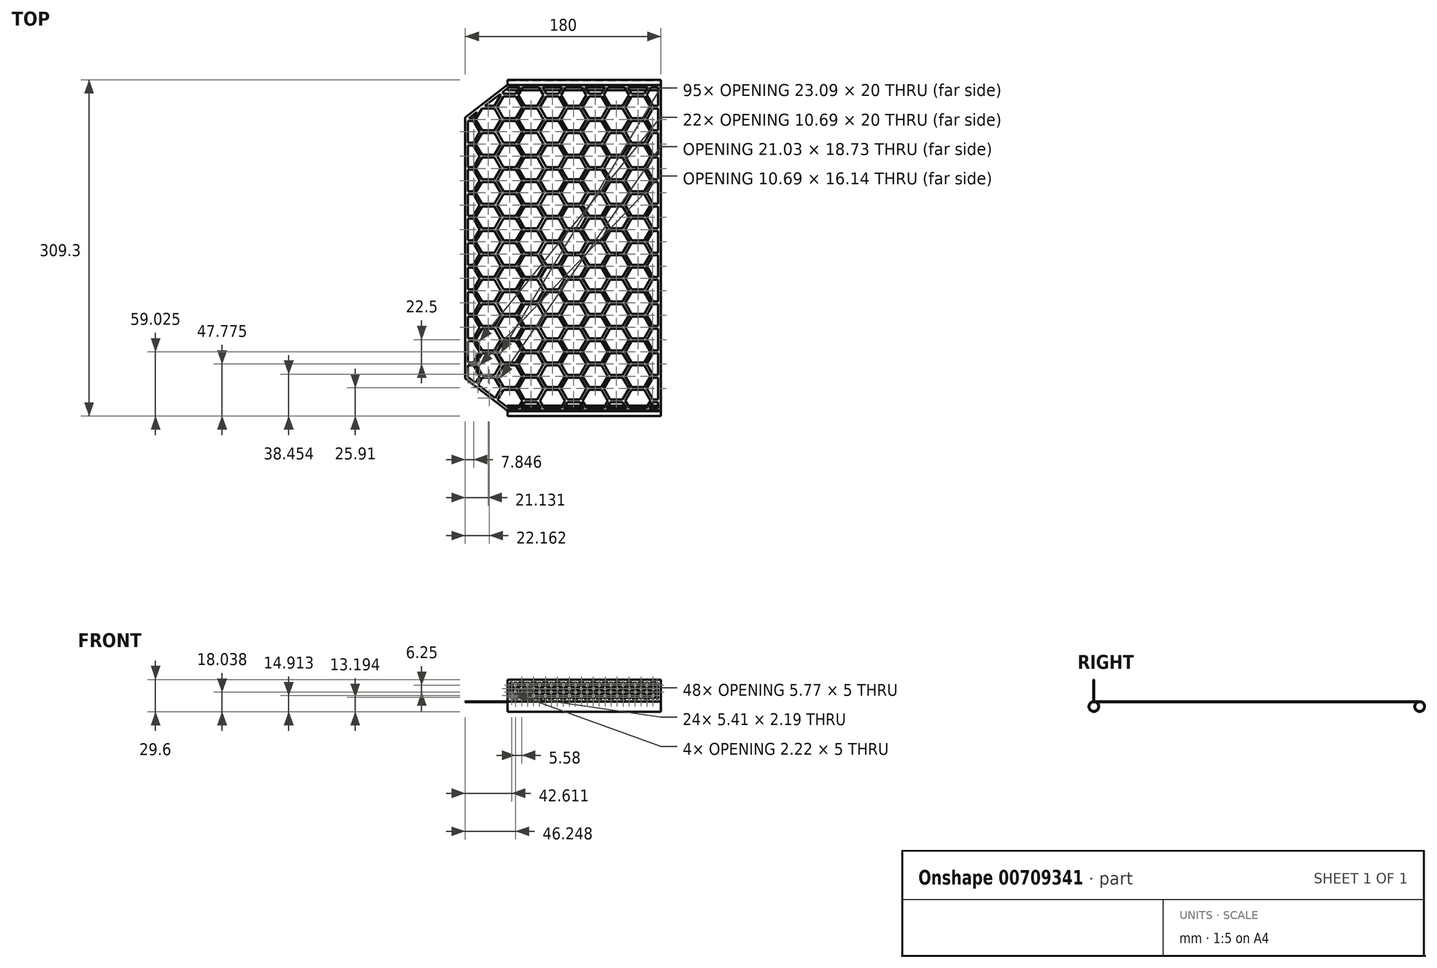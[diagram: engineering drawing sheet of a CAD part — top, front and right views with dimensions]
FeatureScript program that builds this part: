
annotation { "Feature Type Name" : "Feature", "Feature Type Description" : "" }
export const myFeature = defineFeature(function(context is Context, id is Id, definition is map)
    precondition{}
    {
        {
            var Q0;
            Q0=qCreatedBy(makeId("Top.planeOp"),FACE);
            var sketch = newSketch(context, id + "F0", { "sketchPlane" : qUnion([Q0])});
            skLineSegment(sketch, "E0.bottom", {"start": v(90, -150) * mm, "end": v(-90, -150) * mm});
            skLineSegment(sketch, "E0.top", {"start": v(90, 150) * mm, "end": v(-90, 150) * mm});
            skLineSegment(sketch, "E0.left", {"start": v(90, -150) * mm, "end": v(90, 150) * mm});
            skLineSegment(sketch, "E0.right", {"start": v(-90, -150) * mm, "end": v(-90, 150) * mm});
            skPoint(sketch, "E0.middle", {"position": v(0, 0) * mm});
            skLineSegment(sketch, "E1", {"start": v(-51, 150) * mm, "end": v(-90, 120) * mm});
            skLineSegment(sketch, "E2", {"start": v(-90, -120) * mm, "end": v(-51, -150) * mm});
            skSolve(sketch);
        }
        {
            var Q0;
            {var subQ3=sQuery(id+"F0.wireOp",EDGE,"E0.left");Q0=makeQuery(id+"F0.imprint","IMPRINT",FACE,{"disambiguationData":[TD([[makeQuery(id+"F0.imprint","IMPRINT",EDGE,{"derivedFrom":subQ3}),1.0]])]});}
            extrude(context, id + "F1", {"entities" : qUnion([Q0]), "endBound" : BoundingType.SYMMETRIC, "depth" : 0.6 * mm, "offsetDistance" : 25 * mm});
        }
        {
            var Q0;
            Q0=qCreatedBy(makeId("Right.planeOp"),FACE);
            var sketch = newSketch(context, id + "F2", { "sketchPlane" : qUnion([Q0])});
            skCircle(sketch, "E3", {"center": v(-149.85, -4.5) * mm, "radius": 4.2 * mm});
            skCircle(sketch, "E4", {"center": v(-149.85, -4.5) * mm, "radius": 4.8 * mm});
            skCircle(sketch, "E5.MirrorC", {"center": v(149.85, -4.5) * mm, "radius": 4.8 * mm});
            skCircle(sketch, "E6.MirrorC", {"center": v(149.85, -4.5) * mm, "radius": 4.2 * mm});
            skLineSegment(sketch, "E7.bottom", {"start": v(-150.3, 0.3) * mm, "end": v(-149.7, 0.3) * mm});
            skLineSegment(sketch, "E7.top", {"start": v(-150.3, 20.3) * mm, "end": v(-149.7, 20.3) * mm});
            skLineSegment(sketch, "E7.left", {"start": v(-150.3, 0.3) * mm, "end": v(-150.3, 20.3) * mm});
            skLineSegment(sketch, "E7.right", {"start": v(-149.7, 0.3) * mm, "end": v(-149.7, 20.3) * mm});
            skPoint(sketch, "E8", {"position": v(-150, 0.3) * mm});
            skLineSegment(sketch, "E9.0.1", {"start": v(-150, -0.3) * mm, "end": v(-150, 0.3) * mm});
            skLineSegment(sketch, "E9.0.3", {"start": v(-150, 0.3) * mm, "end": v(-150, -0.3) * mm, "construction": true});
            skSolve(sketch);
        }
        {
            var Q0;
            Q0=qSketchRegion(id+"F2",true);
            var Q1;
            Q1=makeQuery(id+"F1.opExtrude","CAP_EDGE",EDGE,{"disambiguationData":[OSD([sQuery(id+"F0.wireOp",EDGE,"E0.bottom")])],"isStart":false});
            sweep(context, id + "F3", {"operationType" : NewBodyOperationType.ADD, "profiles" : qUnion([Q0]), "path" : qUnion([Q1])});
        }
        {
            var Q0;
            Q0=makeQuery(id+"F1.opExtrude","CAP_FACE",FACE,{"disambiguationData":[OSD([sQuery(id+"F0.wireOp",EDGE,"E0.bottom"),sQuery(id+"F0.wireOp",EDGE,"E0.top"),sQuery(id+"F0.wireOp",EDGE,"E0.left"),sQuery(id+"F0.wireOp",EDGE,"E0.right")])],"isStart":false});
            var sketch = newSketch(context, id + "F4", { "sketchPlane" : qUnion([Q0])});
            skCircle(sketch, "E10.cCircle", {"center": v(-68.87, 163.12) * mm, "radius": 10 * mm, "construction": true});
            skLineSegment(sketch, "E10.0", {"start": v(-63.1, 153.12) * mm, "end": v(-74.64, 153.12) * mm});
            skLineSegment(sketch, "E10.1", {"start": v(-74.64, 153.12) * mm, "end": v(-80.42, 163.12) * mm});
            skLineSegment(sketch, "E10.2", {"start": v(-80.42, 163.12) * mm, "end": v(-74.64, 173.12) * mm});
            skLineSegment(sketch, "E10.3", {"start": v(-74.64, 173.12) * mm, "end": v(-63.1, 173.12) * mm});
            skLineSegment(sketch, "E10.4", {"start": v(-63.1, 173.12) * mm, "end": v(-57.32, 163.12) * mm});
            skLineSegment(sketch, "E10.5", {"start": v(-57.32, 163.12) * mm, "end": v(-63.1, 153.12) * mm});
            skPoint(sketch, "E10.0.midPoint", {"position": v(-68.87, 153.12) * mm});
            skCircle(sketch, "E11.cCircle", {"center": v(-88.35, 151.87) * mm, "radius": 10 * mm, "construction": true});
            skLineSegment(sketch, "E11.0", {"start": v(-82.58, 141.87) * mm, "end": v(-94.13, 141.87) * mm});
            skLineSegment(sketch, "E11.1", {"start": v(-94.13, 141.87) * mm, "end": v(-99.9, 151.87) * mm});
            skLineSegment(sketch, "E11.2", {"start": v(-99.9, 151.87) * mm, "end": v(-94.13, 161.87) * mm});
            skLineSegment(sketch, "E11.3", {"start": v(-94.13, 161.87) * mm, "end": v(-82.58, 161.87) * mm});
            skLineSegment(sketch, "E11.4", {"start": v(-82.58, 161.87) * mm, "end": v(-76.8, 151.87) * mm});
            skLineSegment(sketch, "E11.5", {"start": v(-76.8, 151.87) * mm, "end": v(-82.58, 141.87) * mm});
            skPoint(sketch, "E11.0.midPoint", {"position": v(-88.35, 141.87) * mm});
            skLineSegment(sketch, "E12", {"start": v(0, 147.52) * mm, "end": v(0, -147.52) * mm, "construction": true});
            skLineSegment(sketch, "E13", {"start": v(-85.17, 0) * mm, "end": v(85.17, 0) * mm, "construction": true});
            skLineSegment(sketch, "E14.0.1.0", {"start": v(-94.13, 139.37) * mm, "end": v(-82.58, 139.37) * mm});
            skLineSegment(sketch, "E14.0.1.1", {"start": v(-99.9, 129.37) * mm, "end": v(-94.13, 139.37) * mm});
            skLineSegment(sketch, "E14.0.1.2", {"start": v(-94.13, 119.37) * mm, "end": v(-99.9, 129.37) * mm});
            skLineSegment(sketch, "E14.0.1.3", {"start": v(-82.58, 119.37) * mm, "end": v(-94.13, 119.37) * mm});
            skLineSegment(sketch, "E14.0.1.4", {"start": v(-76.8, 129.37) * mm, "end": v(-82.58, 119.37) * mm});
            skLineSegment(sketch, "E14.0.1.5", {"start": v(-82.58, 139.37) * mm, "end": v(-76.8, 129.37) * mm});
            skLineSegment(sketch, "E14.0.1.6", {"start": v(-80.42, 140.62) * mm, "end": v(-74.64, 150.62) * mm});
            skLineSegment(sketch, "E14.0.1.7", {"start": v(-74.64, 130.62) * mm, "end": v(-80.42, 140.62) * mm});
            skLineSegment(sketch, "E14.0.1.8", {"start": v(-74.64, 150.62) * mm, "end": v(-63.1, 150.62) * mm});
            skLineSegment(sketch, "E14.0.1.9", {"start": v(-63.1, 150.62) * mm, "end": v(-57.32, 140.62) * mm});
            skLineSegment(sketch, "E14.0.1.10", {"start": v(-57.32, 140.62) * mm, "end": v(-63.1, 130.62) * mm});
            skLineSegment(sketch, "E14.0.1.11", {"start": v(-63.1, 130.62) * mm, "end": v(-74.64, 130.62) * mm});
            skLineSegment(sketch, "E14.1.0.0", {"start": v(-54.82, 161.87) * mm, "end": v(-43.28, 161.87) * mm});
            skLineSegment(sketch, "E14.1.0.1", {"start": v(-60.6, 151.87) * mm, "end": v(-54.82, 161.87) * mm});
            skLineSegment(sketch, "E14.1.0.2", {"start": v(-54.82, 141.87) * mm, "end": v(-60.6, 151.87) * mm});
            skLineSegment(sketch, "E14.1.0.3", {"start": v(-43.28, 141.87) * mm, "end": v(-54.82, 141.87) * mm});
            skLineSegment(sketch, "E14.1.0.4", {"start": v(-37.5, 151.87) * mm, "end": v(-43.28, 141.87) * mm});
            skLineSegment(sketch, "E14.1.0.5", {"start": v(-43.28, 161.87) * mm, "end": v(-37.5, 151.87) * mm});
            skLineSegment(sketch, "E14.1.0.6", {"start": v(-41.11, 163.12) * mm, "end": v(-35.34, 173.12) * mm});
            skLineSegment(sketch, "E14.1.0.7", {"start": v(-35.34, 153.12) * mm, "end": v(-41.11, 163.12) * mm});
            skLineSegment(sketch, "E14.1.0.8", {"start": v(-35.34, 173.12) * mm, "end": v(-23.79, 173.12) * mm});
            skLineSegment(sketch, "E14.1.0.9", {"start": v(-23.79, 173.12) * mm, "end": v(-18.02, 163.12) * mm});
            skLineSegment(sketch, "E14.1.0.10", {"start": v(-18.02, 163.12) * mm, "end": v(-23.79, 153.12) * mm});
            skLineSegment(sketch, "E14.1.0.11", {"start": v(-23.79, 153.12) * mm, "end": v(-35.34, 153.12) * mm});
            skLineSegment(sketch, "E14.1.1.0", {"start": v(-54.82, 139.37) * mm, "end": v(-43.28, 139.37) * mm});
            skLineSegment(sketch, "E14.1.1.1", {"start": v(-60.6, 129.37) * mm, "end": v(-54.82, 139.37) * mm});
            skLineSegment(sketch, "E14.1.1.2", {"start": v(-54.82, 119.37) * mm, "end": v(-60.6, 129.37) * mm});
            skLineSegment(sketch, "E14.1.1.3", {"start": v(-43.28, 119.37) * mm, "end": v(-54.82, 119.37) * mm});
            skLineSegment(sketch, "E14.1.1.4", {"start": v(-37.5, 129.37) * mm, "end": v(-43.28, 119.37) * mm});
            skLineSegment(sketch, "E14.1.1.5", {"start": v(-43.28, 139.37) * mm, "end": v(-37.5, 129.37) * mm});
            skLineSegment(sketch, "E14.1.1.6", {"start": v(-41.11, 140.62) * mm, "end": v(-35.34, 150.62) * mm});
            skLineSegment(sketch, "E14.1.1.7", {"start": v(-35.34, 130.62) * mm, "end": v(-41.11, 140.62) * mm});
            skLineSegment(sketch, "E14.1.1.8", {"start": v(-35.34, 150.62) * mm, "end": v(-23.79, 150.62) * mm});
            skLineSegment(sketch, "E14.1.1.9", {"start": v(-23.79, 150.62) * mm, "end": v(-18.02, 140.62) * mm});
            skLineSegment(sketch, "E14.1.1.10", {"start": v(-18.02, 140.62) * mm, "end": v(-23.79, 130.62) * mm});
            skLineSegment(sketch, "E14.1.1.11", {"start": v(-23.79, 130.62) * mm, "end": v(-35.34, 130.62) * mm});
            skLineSegment(sketch, "E14.2.0.0", {"start": v(-15.52, 161.87) * mm, "end": v(-3.97, 161.87) * mm});
            skLineSegment(sketch, "E14.2.0.1", {"start": v(-21.29, 151.87) * mm, "end": v(-15.52, 161.87) * mm});
            skLineSegment(sketch, "E14.2.0.2", {"start": v(-15.52, 141.87) * mm, "end": v(-21.29, 151.87) * mm});
            skLineSegment(sketch, "E14.2.0.3", {"start": v(-3.97, 141.87) * mm, "end": v(-15.52, 141.87) * mm});
            skLineSegment(sketch, "E14.2.0.4", {"start": v(1.8, 151.87) * mm, "end": v(-3.97, 141.87) * mm});
            skLineSegment(sketch, "E14.2.0.5", {"start": v(-3.97, 161.87) * mm, "end": v(1.8, 151.87) * mm});
            skLineSegment(sketch, "E14.2.0.6", {"start": v(-1.8, 163.12) * mm, "end": v(3.97, 173.12) * mm});
            skLineSegment(sketch, "E14.2.0.7", {"start": v(3.97, 153.12) * mm, "end": v(-1.8, 163.12) * mm});
            skLineSegment(sketch, "E14.2.0.8", {"start": v(3.97, 173.12) * mm, "end": v(15.52, 173.12) * mm});
            skLineSegment(sketch, "E14.2.0.9", {"start": v(15.52, 173.12) * mm, "end": v(21.29, 163.12) * mm});
            skLineSegment(sketch, "E14.2.0.10", {"start": v(21.29, 163.12) * mm, "end": v(15.52, 153.12) * mm});
            skLineSegment(sketch, "E14.2.0.11", {"start": v(15.52, 153.12) * mm, "end": v(3.97, 153.12) * mm});
            skLineSegment(sketch, "E14.2.1.0", {"start": v(-15.52, 139.37) * mm, "end": v(-3.97, 139.37) * mm});
            skLineSegment(sketch, "E14.2.1.1", {"start": v(-21.29, 129.37) * mm, "end": v(-15.52, 139.37) * mm});
            skLineSegment(sketch, "E14.2.1.2", {"start": v(-15.52, 119.37) * mm, "end": v(-21.29, 129.37) * mm});
            skLineSegment(sketch, "E14.2.1.3", {"start": v(-3.97, 119.37) * mm, "end": v(-15.52, 119.37) * mm});
            skLineSegment(sketch, "E14.2.1.4", {"start": v(1.8, 129.37) * mm, "end": v(-3.97, 119.37) * mm});
            skLineSegment(sketch, "E14.2.1.5", {"start": v(-3.97, 139.37) * mm, "end": v(1.8, 129.37) * mm});
            skLineSegment(sketch, "E14.2.1.6", {"start": v(-1.8, 140.62) * mm, "end": v(3.97, 150.62) * mm});
            skLineSegment(sketch, "E14.2.1.7", {"start": v(3.97, 130.62) * mm, "end": v(-1.8, 140.62) * mm});
            skLineSegment(sketch, "E14.2.1.8", {"start": v(3.97, 150.62) * mm, "end": v(15.52, 150.62) * mm});
            skLineSegment(sketch, "E14.2.1.9", {"start": v(15.52, 150.62) * mm, "end": v(21.29, 140.62) * mm});
            skLineSegment(sketch, "E14.2.1.10", {"start": v(21.29, 140.62) * mm, "end": v(15.52, 130.62) * mm});
            skLineSegment(sketch, "E14.2.1.11", {"start": v(15.52, 130.62) * mm, "end": v(3.97, 130.62) * mm});
            skLineSegment(sketch, "E14.direction1", {"start": v(-94.13, 161.87) * mm, "end": v(-54.82, 161.87) * mm, "construction": true});
            skLineSegment(sketch, "E14.direction2", {"start": v(-94.13, 161.87) * mm, "end": v(-94.13, 139.37) * mm, "construction": true});
            skLineSegment(sketch, "E15.0.3.0", {"start": v(23.79, 161.87) * mm, "end": v(35.34, 161.87) * mm});
            skLineSegment(sketch, "E15.3.3.0", {"start": v(18.02, 151.87) * mm, "end": v(23.79, 161.87) * mm});
            skLineSegment(sketch, "E15.6.3.0", {"start": v(23.79, 141.87) * mm, "end": v(18.02, 151.87) * mm});
            skLineSegment(sketch, "E15.9.3.0", {"start": v(35.34, 141.87) * mm, "end": v(23.79, 141.87) * mm});
            skLineSegment(sketch, "E15.12.3.0", {"start": v(41.11, 151.87) * mm, "end": v(35.34, 141.87) * mm});
            skLineSegment(sketch, "E15.15.3.0", {"start": v(35.34, 161.87) * mm, "end": v(41.11, 151.87) * mm});
            skLineSegment(sketch, "E15.18.3.0", {"start": v(37.5, 163.12) * mm, "end": v(43.28, 173.12) * mm});
            skLineSegment(sketch, "E15.21.3.0", {"start": v(43.28, 153.12) * mm, "end": v(37.5, 163.12) * mm});
            skLineSegment(sketch, "E15.24.3.0", {"start": v(43.28, 173.12) * mm, "end": v(54.82, 173.12) * mm});
            skLineSegment(sketch, "E15.27.3.0", {"start": v(54.82, 173.12) * mm, "end": v(60.6, 163.12) * mm});
            skLineSegment(sketch, "E15.30.3.0", {"start": v(60.6, 163.12) * mm, "end": v(54.82, 153.12) * mm});
            skLineSegment(sketch, "E15.33.3.0", {"start": v(54.82, 153.12) * mm, "end": v(43.28, 153.12) * mm});
            skLineSegment(sketch, "E15.0.3.1", {"start": v(23.79, 139.37) * mm, "end": v(35.34, 139.37) * mm});
            skLineSegment(sketch, "E15.3.3.1", {"start": v(18.02, 129.37) * mm, "end": v(23.79, 139.37) * mm});
            skLineSegment(sketch, "E15.6.3.1", {"start": v(23.79, 119.37) * mm, "end": v(18.02, 129.37) * mm});
            skLineSegment(sketch, "E15.9.3.1", {"start": v(35.34, 119.37) * mm, "end": v(23.79, 119.37) * mm});
            skLineSegment(sketch, "E15.12.3.1", {"start": v(41.11, 129.37) * mm, "end": v(35.34, 119.37) * mm});
            skLineSegment(sketch, "E15.15.3.1", {"start": v(35.34, 139.37) * mm, "end": v(41.11, 129.37) * mm});
            skLineSegment(sketch, "E15.18.3.1", {"start": v(37.5, 140.62) * mm, "end": v(43.28, 150.62) * mm});
            skLineSegment(sketch, "E15.21.3.1", {"start": v(43.28, 130.62) * mm, "end": v(37.5, 140.62) * mm});
            skLineSegment(sketch, "E15.24.3.1", {"start": v(43.28, 150.62) * mm, "end": v(54.82, 150.62) * mm});
            skLineSegment(sketch, "E15.27.3.1", {"start": v(54.82, 150.62) * mm, "end": v(60.6, 140.62) * mm});
            skLineSegment(sketch, "E15.30.3.1", {"start": v(60.6, 140.62) * mm, "end": v(54.82, 130.62) * mm});
            skLineSegment(sketch, "E15.33.3.1", {"start": v(54.82, 130.62) * mm, "end": v(43.28, 130.62) * mm});
            skLineSegment(sketch, "E15.0.4.0", {"start": v(63.1, 161.87) * mm, "end": v(74.64, 161.87) * mm});
            skLineSegment(sketch, "E15.3.4.0", {"start": v(57.32, 151.87) * mm, "end": v(63.1, 161.87) * mm});
            skLineSegment(sketch, "E15.6.4.0", {"start": v(63.1, 141.87) * mm, "end": v(57.32, 151.87) * mm});
            skLineSegment(sketch, "E15.9.4.0", {"start": v(74.64, 141.87) * mm, "end": v(63.1, 141.87) * mm});
            skLineSegment(sketch, "E15.12.4.0", {"start": v(80.42, 151.87) * mm, "end": v(74.64, 141.87) * mm});
            skLineSegment(sketch, "E15.15.4.0", {"start": v(74.64, 161.87) * mm, "end": v(80.42, 151.87) * mm});
            skLineSegment(sketch, "E15.18.4.0", {"start": v(76.8, 163.12) * mm, "end": v(82.58, 173.12) * mm});
            skLineSegment(sketch, "E15.21.4.0", {"start": v(82.58, 153.12) * mm, "end": v(76.8, 163.12) * mm});
            skLineSegment(sketch, "E15.24.4.0", {"start": v(82.58, 173.12) * mm, "end": v(94.13, 173.12) * mm});
            skLineSegment(sketch, "E15.27.4.0", {"start": v(94.13, 173.12) * mm, "end": v(99.9, 163.12) * mm});
            skLineSegment(sketch, "E15.30.4.0", {"start": v(99.9, 163.12) * mm, "end": v(94.13, 153.12) * mm});
            skLineSegment(sketch, "E15.33.4.0", {"start": v(94.13, 153.12) * mm, "end": v(82.58, 153.12) * mm});
            skLineSegment(sketch, "E15.0.4.1", {"start": v(63.1, 139.37) * mm, "end": v(74.64, 139.37) * mm});
            skLineSegment(sketch, "E15.3.4.1", {"start": v(57.32, 129.37) * mm, "end": v(63.1, 139.37) * mm});
            skLineSegment(sketch, "E15.6.4.1", {"start": v(63.1, 119.37) * mm, "end": v(57.32, 129.37) * mm});
            skLineSegment(sketch, "E15.9.4.1", {"start": v(74.64, 119.37) * mm, "end": v(63.1, 119.37) * mm});
            skLineSegment(sketch, "E15.12.4.1", {"start": v(80.42, 129.37) * mm, "end": v(74.64, 119.37) * mm});
            skLineSegment(sketch, "E15.15.4.1", {"start": v(74.64, 139.37) * mm, "end": v(80.42, 129.37) * mm});
            skLineSegment(sketch, "E15.18.4.1", {"start": v(76.8, 140.62) * mm, "end": v(82.58, 150.62) * mm});
            skLineSegment(sketch, "E15.21.4.1", {"start": v(82.58, 130.62) * mm, "end": v(76.8, 140.62) * mm});
            skLineSegment(sketch, "E15.24.4.1", {"start": v(82.58, 150.62) * mm, "end": v(94.13, 150.62) * mm});
            skLineSegment(sketch, "E15.27.4.1", {"start": v(94.13, 150.62) * mm, "end": v(99.9, 140.62) * mm});
            skLineSegment(sketch, "E15.30.4.1", {"start": v(99.9, 140.62) * mm, "end": v(94.13, 130.62) * mm});
            skLineSegment(sketch, "E15.33.4.1", {"start": v(94.13, 130.62) * mm, "end": v(82.58, 130.62) * mm});
            skLineSegment(sketch, "E16.0.0.2", {"start": v(-94.13, 116.87) * mm, "end": v(-82.58, 116.87) * mm});
            skLineSegment(sketch, "E16.3.0.2", {"start": v(-99.9, 106.87) * mm, "end": v(-94.13, 116.87) * mm});
            skLineSegment(sketch, "E16.6.0.2", {"start": v(-94.13, 96.87) * mm, "end": v(-99.9, 106.87) * mm});
            skLineSegment(sketch, "E16.9.0.2", {"start": v(-82.58, 96.87) * mm, "end": v(-94.13, 96.87) * mm});
            skLineSegment(sketch, "E16.12.0.2", {"start": v(-76.8, 106.87) * mm, "end": v(-82.58, 96.87) * mm});
            skLineSegment(sketch, "E16.15.0.2", {"start": v(-82.58, 116.87) * mm, "end": v(-76.8, 106.87) * mm});
            skLineSegment(sketch, "E16.18.0.2", {"start": v(-80.42, 118.12) * mm, "end": v(-74.64, 128.12) * mm});
            skLineSegment(sketch, "E16.21.0.2", {"start": v(-74.64, 108.12) * mm, "end": v(-80.42, 118.12) * mm});
            skLineSegment(sketch, "E16.24.0.2", {"start": v(-74.64, 128.12) * mm, "end": v(-63.1, 128.12) * mm});
            skLineSegment(sketch, "E16.27.0.2", {"start": v(-63.1, 128.12) * mm, "end": v(-57.32, 118.12) * mm});
            skLineSegment(sketch, "E16.30.0.2", {"start": v(-57.32, 118.12) * mm, "end": v(-63.1, 108.12) * mm});
            skLineSegment(sketch, "E16.33.0.2", {"start": v(-63.1, 108.12) * mm, "end": v(-74.64, 108.12) * mm});
            skLineSegment(sketch, "E16.0.0.3", {"start": v(-94.13, 94.37) * mm, "end": v(-82.58, 94.37) * mm});
            skLineSegment(sketch, "E16.3.0.3", {"start": v(-99.9, 84.37) * mm, "end": v(-94.13, 94.37) * mm});
            skLineSegment(sketch, "E16.6.0.3", {"start": v(-94.13, 74.37) * mm, "end": v(-99.9, 84.37) * mm});
            skLineSegment(sketch, "E16.9.0.3", {"start": v(-82.58, 74.37) * mm, "end": v(-94.13, 74.37) * mm});
            skLineSegment(sketch, "E16.12.0.3", {"start": v(-76.8, 84.37) * mm, "end": v(-82.58, 74.37) * mm});
            skLineSegment(sketch, "E16.15.0.3", {"start": v(-82.58, 94.37) * mm, "end": v(-76.8, 84.37) * mm});
            skLineSegment(sketch, "E16.18.0.3", {"start": v(-80.42, 95.62) * mm, "end": v(-74.64, 105.62) * mm});
            skLineSegment(sketch, "E16.21.0.3", {"start": v(-74.64, 85.62) * mm, "end": v(-80.42, 95.62) * mm});
            skLineSegment(sketch, "E16.24.0.3", {"start": v(-74.64, 105.62) * mm, "end": v(-63.1, 105.62) * mm});
            skLineSegment(sketch, "E16.27.0.3", {"start": v(-63.1, 105.62) * mm, "end": v(-57.32, 95.62) * mm});
            skLineSegment(sketch, "E16.30.0.3", {"start": v(-57.32, 95.62) * mm, "end": v(-63.1, 85.62) * mm});
            skLineSegment(sketch, "E16.33.0.3", {"start": v(-63.1, 85.62) * mm, "end": v(-74.64, 85.62) * mm});
            skLineSegment(sketch, "E16.0.0.4", {"start": v(-94.13, 71.87) * mm, "end": v(-82.58, 71.87) * mm});
            skLineSegment(sketch, "E16.3.0.4", {"start": v(-99.9, 61.87) * mm, "end": v(-94.13, 71.87) * mm});
            skLineSegment(sketch, "E16.6.0.4", {"start": v(-94.13, 51.87) * mm, "end": v(-99.9, 61.87) * mm});
            skLineSegment(sketch, "E16.9.0.4", {"start": v(-82.58, 51.87) * mm, "end": v(-94.13, 51.87) * mm});
            skLineSegment(sketch, "E16.12.0.4", {"start": v(-76.8, 61.87) * mm, "end": v(-82.58, 51.87) * mm});
            skLineSegment(sketch, "E16.15.0.4", {"start": v(-82.58, 71.87) * mm, "end": v(-76.8, 61.87) * mm});
            skLineSegment(sketch, "E16.18.0.4", {"start": v(-80.42, 73.12) * mm, "end": v(-74.64, 83.12) * mm});
            skLineSegment(sketch, "E16.21.0.4", {"start": v(-74.64, 63.12) * mm, "end": v(-80.42, 73.12) * mm});
            skLineSegment(sketch, "E16.24.0.4", {"start": v(-74.64, 83.12) * mm, "end": v(-63.1, 83.12) * mm});
            skLineSegment(sketch, "E16.27.0.4", {"start": v(-63.1, 83.12) * mm, "end": v(-57.32, 73.12) * mm});
            skLineSegment(sketch, "E16.30.0.4", {"start": v(-57.32, 73.12) * mm, "end": v(-63.1, 63.12) * mm});
            skLineSegment(sketch, "E16.33.0.4", {"start": v(-63.1, 63.12) * mm, "end": v(-74.64, 63.12) * mm});
            skLineSegment(sketch, "E16.0.0.5", {"start": v(-94.13, 49.37) * mm, "end": v(-82.58, 49.37) * mm});
            skLineSegment(sketch, "E16.3.0.5", {"start": v(-99.9, 39.37) * mm, "end": v(-94.13, 49.37) * mm});
            skLineSegment(sketch, "E16.6.0.5", {"start": v(-94.13, 29.37) * mm, "end": v(-99.9, 39.37) * mm});
            skLineSegment(sketch, "E16.9.0.5", {"start": v(-82.58, 29.37) * mm, "end": v(-94.13, 29.37) * mm});
            skLineSegment(sketch, "E16.12.0.5", {"start": v(-76.8, 39.37) * mm, "end": v(-82.58, 29.37) * mm});
            skLineSegment(sketch, "E16.15.0.5", {"start": v(-82.58, 49.37) * mm, "end": v(-76.8, 39.37) * mm});
            skLineSegment(sketch, "E16.18.0.5", {"start": v(-80.42, 50.62) * mm, "end": v(-74.64, 60.62) * mm});
            skLineSegment(sketch, "E16.21.0.5", {"start": v(-74.64, 40.62) * mm, "end": v(-80.42, 50.62) * mm});
            skLineSegment(sketch, "E16.24.0.5", {"start": v(-74.64, 60.62) * mm, "end": v(-63.1, 60.62) * mm});
            skLineSegment(sketch, "E16.27.0.5", {"start": v(-63.1, 60.62) * mm, "end": v(-57.32, 50.62) * mm});
            skLineSegment(sketch, "E16.30.0.5", {"start": v(-57.32, 50.62) * mm, "end": v(-63.1, 40.62) * mm});
            skLineSegment(sketch, "E16.33.0.5", {"start": v(-63.1, 40.62) * mm, "end": v(-74.64, 40.62) * mm});
            skLineSegment(sketch, "E16.0.0.6", {"start": v(-94.13, 26.87) * mm, "end": v(-82.58, 26.87) * mm});
            skLineSegment(sketch, "E16.3.0.6", {"start": v(-99.9, 16.87) * mm, "end": v(-94.13, 26.87) * mm});
            skLineSegment(sketch, "E16.6.0.6", {"start": v(-94.13, 6.87) * mm, "end": v(-99.9, 16.87) * mm});
            skLineSegment(sketch, "E16.9.0.6", {"start": v(-82.58, 6.87) * mm, "end": v(-94.13, 6.87) * mm});
            skLineSegment(sketch, "E16.12.0.6", {"start": v(-76.8, 16.87) * mm, "end": v(-82.58, 6.87) * mm});
            skLineSegment(sketch, "E16.15.0.6", {"start": v(-82.58, 26.87) * mm, "end": v(-76.8, 16.87) * mm});
            skLineSegment(sketch, "E16.18.0.6", {"start": v(-80.42, 28.12) * mm, "end": v(-74.64, 38.12) * mm});
            skLineSegment(sketch, "E16.21.0.6", {"start": v(-74.64, 18.12) * mm, "end": v(-80.42, 28.12) * mm});
            skLineSegment(sketch, "E16.24.0.6", {"start": v(-74.64, 38.12) * mm, "end": v(-63.1, 38.12) * mm});
            skLineSegment(sketch, "E16.27.0.6", {"start": v(-63.1, 38.12) * mm, "end": v(-57.32, 28.12) * mm});
            skLineSegment(sketch, "E16.30.0.6", {"start": v(-57.32, 28.12) * mm, "end": v(-63.1, 18.12) * mm});
            skLineSegment(sketch, "E16.33.0.6", {"start": v(-63.1, 18.12) * mm, "end": v(-74.64, 18.12) * mm});
            skLineSegment(sketch, "E16.0.0.7", {"start": v(-94.13, 4.37) * mm, "end": v(-82.58, 4.37) * mm});
            skLineSegment(sketch, "E16.3.0.7", {"start": v(-99.9, -5.63) * mm, "end": v(-94.13, 4.37) * mm});
            skLineSegment(sketch, "E16.6.0.7", {"start": v(-94.13, -15.63) * mm, "end": v(-99.9, -5.63) * mm});
            skLineSegment(sketch, "E16.9.0.7", {"start": v(-82.58, -15.63) * mm, "end": v(-94.13, -15.63) * mm});
            skLineSegment(sketch, "E16.12.0.7", {"start": v(-76.8, -5.63) * mm, "end": v(-82.58, -15.63) * mm});
            skLineSegment(sketch, "E16.15.0.7", {"start": v(-82.58, 4.37) * mm, "end": v(-76.8, -5.63) * mm});
            skLineSegment(sketch, "E16.18.0.7", {"start": v(-80.42, 5.62) * mm, "end": v(-74.64, 15.62) * mm});
            skLineSegment(sketch, "E16.21.0.7", {"start": v(-74.64, -4.38) * mm, "end": v(-80.42, 5.62) * mm});
            skLineSegment(sketch, "E16.24.0.7", {"start": v(-74.64, 15.62) * mm, "end": v(-63.1, 15.62) * mm});
            skLineSegment(sketch, "E16.27.0.7", {"start": v(-63.1, 15.62) * mm, "end": v(-57.32, 5.62) * mm});
            skLineSegment(sketch, "E16.30.0.7", {"start": v(-57.32, 5.62) * mm, "end": v(-63.1, -4.38) * mm});
            skLineSegment(sketch, "E16.33.0.7", {"start": v(-63.1, -4.38) * mm, "end": v(-74.64, -4.38) * mm});
            skLineSegment(sketch, "E16.0.0.8", {"start": v(-94.13, -18.13) * mm, "end": v(-82.58, -18.13) * mm});
            skLineSegment(sketch, "E16.3.0.8", {"start": v(-99.9, -28.13) * mm, "end": v(-94.13, -18.13) * mm});
            skLineSegment(sketch, "E16.6.0.8", {"start": v(-94.13, -38.13) * mm, "end": v(-99.9, -28.13) * mm});
            skLineSegment(sketch, "E16.9.0.8", {"start": v(-82.58, -38.13) * mm, "end": v(-94.13, -38.13) * mm});
            skLineSegment(sketch, "E16.12.0.8", {"start": v(-76.8, -28.13) * mm, "end": v(-82.58, -38.13) * mm});
            skLineSegment(sketch, "E16.15.0.8", {"start": v(-82.58, -18.13) * mm, "end": v(-76.8, -28.13) * mm});
            skLineSegment(sketch, "E16.18.0.8", {"start": v(-80.42, -16.88) * mm, "end": v(-74.64, -6.88) * mm});
            skLineSegment(sketch, "E16.21.0.8", {"start": v(-74.64, -26.88) * mm, "end": v(-80.42, -16.88) * mm});
            skLineSegment(sketch, "E16.24.0.8", {"start": v(-74.64, -6.88) * mm, "end": v(-63.1, -6.88) * mm});
            skLineSegment(sketch, "E16.27.0.8", {"start": v(-63.1, -6.88) * mm, "end": v(-57.32, -16.88) * mm});
            skLineSegment(sketch, "E16.30.0.8", {"start": v(-57.32, -16.88) * mm, "end": v(-63.1, -26.88) * mm});
            skLineSegment(sketch, "E16.33.0.8", {"start": v(-63.1, -26.88) * mm, "end": v(-74.64, -26.88) * mm});
            skLineSegment(sketch, "E16.0.0.9", {"start": v(-94.13, -40.63) * mm, "end": v(-82.58, -40.63) * mm});
            skLineSegment(sketch, "E16.3.0.9", {"start": v(-99.9, -50.63) * mm, "end": v(-94.13, -40.63) * mm});
            skLineSegment(sketch, "E16.6.0.9", {"start": v(-94.13, -60.63) * mm, "end": v(-99.9, -50.63) * mm});
            skLineSegment(sketch, "E16.9.0.9", {"start": v(-82.58, -60.63) * mm, "end": v(-94.13, -60.63) * mm});
            skLineSegment(sketch, "E16.12.0.9", {"start": v(-76.8, -50.63) * mm, "end": v(-82.58, -60.63) * mm});
            skLineSegment(sketch, "E16.15.0.9", {"start": v(-82.58, -40.63) * mm, "end": v(-76.8, -50.63) * mm});
            skLineSegment(sketch, "E16.18.0.9", {"start": v(-80.42, -39.38) * mm, "end": v(-74.64, -29.38) * mm});
            skLineSegment(sketch, "E16.21.0.9", {"start": v(-74.64, -49.38) * mm, "end": v(-80.42, -39.38) * mm});
            skLineSegment(sketch, "E16.24.0.9", {"start": v(-74.64, -29.38) * mm, "end": v(-63.1, -29.38) * mm});
            skLineSegment(sketch, "E16.27.0.9", {"start": v(-63.1, -29.38) * mm, "end": v(-57.32, -39.38) * mm});
            skLineSegment(sketch, "E16.30.0.9", {"start": v(-57.32, -39.38) * mm, "end": v(-63.1, -49.38) * mm});
            skLineSegment(sketch, "E16.33.0.9", {"start": v(-63.1, -49.38) * mm, "end": v(-74.64, -49.38) * mm});
            skLineSegment(sketch, "E16.0.0.10", {"start": v(-94.13, -63.13) * mm, "end": v(-82.58, -63.13) * mm});
            skLineSegment(sketch, "E16.3.0.10", {"start": v(-99.9, -73.13) * mm, "end": v(-94.13, -63.13) * mm});
            skLineSegment(sketch, "E16.6.0.10", {"start": v(-94.13, -83.13) * mm, "end": v(-99.9, -73.13) * mm});
            skLineSegment(sketch, "E16.9.0.10", {"start": v(-82.58, -83.13) * mm, "end": v(-94.13, -83.13) * mm});
            skLineSegment(sketch, "E16.12.0.10", {"start": v(-76.8, -73.13) * mm, "end": v(-82.58, -83.13) * mm});
            skLineSegment(sketch, "E16.15.0.10", {"start": v(-82.58, -63.13) * mm, "end": v(-76.8, -73.13) * mm});
            skLineSegment(sketch, "E16.18.0.10", {"start": v(-80.42, -61.88) * mm, "end": v(-74.64, -51.88) * mm});
            skLineSegment(sketch, "E16.21.0.10", {"start": v(-74.64, -71.88) * mm, "end": v(-80.42, -61.88) * mm});
            skLineSegment(sketch, "E16.24.0.10", {"start": v(-74.64, -51.88) * mm, "end": v(-63.1, -51.88) * mm});
            skLineSegment(sketch, "E16.27.0.10", {"start": v(-63.1, -51.88) * mm, "end": v(-57.32, -61.88) * mm});
            skLineSegment(sketch, "E16.30.0.10", {"start": v(-57.32, -61.88) * mm, "end": v(-63.1, -71.88) * mm});
            skLineSegment(sketch, "E16.33.0.10", {"start": v(-63.1, -71.88) * mm, "end": v(-74.64, -71.88) * mm});
            skLineSegment(sketch, "E16.0.0.11", {"start": v(-94.13, -85.63) * mm, "end": v(-82.58, -85.63) * mm});
            skLineSegment(sketch, "E16.3.0.11", {"start": v(-99.9, -95.63) * mm, "end": v(-94.13, -85.63) * mm});
            skLineSegment(sketch, "E16.6.0.11", {"start": v(-94.13, -105.63) * mm, "end": v(-99.9, -95.63) * mm});
            skLineSegment(sketch, "E16.9.0.11", {"start": v(-82.58, -105.63) * mm, "end": v(-94.13, -105.63) * mm});
            skLineSegment(sketch, "E16.12.0.11", {"start": v(-76.8, -95.63) * mm, "end": v(-82.58, -105.63) * mm});
            skLineSegment(sketch, "E16.15.0.11", {"start": v(-82.58, -85.62) * mm, "end": v(-76.8, -95.63) * mm});
            skLineSegment(sketch, "E16.18.0.11", {"start": v(-80.42, -84.38) * mm, "end": v(-74.64, -74.38) * mm});
            skLineSegment(sketch, "E16.21.0.11", {"start": v(-74.64, -94.38) * mm, "end": v(-80.42, -84.38) * mm});
            skLineSegment(sketch, "E16.24.0.11", {"start": v(-74.64, -74.38) * mm, "end": v(-63.1, -74.38) * mm});
            skLineSegment(sketch, "E16.27.0.11", {"start": v(-63.1, -74.38) * mm, "end": v(-57.32, -84.38) * mm});
            skLineSegment(sketch, "E16.30.0.11", {"start": v(-57.32, -84.38) * mm, "end": v(-63.1, -94.38) * mm});
            skLineSegment(sketch, "E16.33.0.11", {"start": v(-63.1, -94.38) * mm, "end": v(-74.64, -94.38) * mm});
            skLineSegment(sketch, "E16.0.0.12", {"start": v(-94.13, -108.13) * mm, "end": v(-82.58, -108.13) * mm});
            skLineSegment(sketch, "E16.3.0.12", {"start": v(-99.9, -118.13) * mm, "end": v(-94.13, -108.13) * mm});
            skLineSegment(sketch, "E16.6.0.12", {"start": v(-94.13, -128.13) * mm, "end": v(-99.9, -118.13) * mm});
            skLineSegment(sketch, "E16.9.0.12", {"start": v(-82.58, -128.13) * mm, "end": v(-94.13, -128.13) * mm});
            skLineSegment(sketch, "E16.12.0.12", {"start": v(-76.8, -118.13) * mm, "end": v(-82.58, -128.13) * mm});
            skLineSegment(sketch, "E16.15.0.12", {"start": v(-82.58, -108.13) * mm, "end": v(-76.8, -118.13) * mm});
            skLineSegment(sketch, "E16.18.0.12", {"start": v(-80.42, -106.88) * mm, "end": v(-74.64, -96.88) * mm});
            skLineSegment(sketch, "E16.21.0.12", {"start": v(-74.64, -116.87) * mm, "end": v(-80.42, -106.88) * mm});
            skLineSegment(sketch, "E16.24.0.12", {"start": v(-74.64, -96.88) * mm, "end": v(-63.1, -96.88) * mm});
            skLineSegment(sketch, "E16.27.0.12", {"start": v(-63.1, -96.88) * mm, "end": v(-57.32, -106.88) * mm});
            skLineSegment(sketch, "E16.30.0.12", {"start": v(-57.32, -106.88) * mm, "end": v(-63.1, -116.88) * mm});
            skLineSegment(sketch, "E16.33.0.12", {"start": v(-63.1, -116.88) * mm, "end": v(-74.64, -116.88) * mm});
            skLineSegment(sketch, "E16.0.0.13", {"start": v(-94.13, -130.62) * mm, "end": v(-82.58, -130.62) * mm});
            skLineSegment(sketch, "E16.3.0.13", {"start": v(-99.9, -140.63) * mm, "end": v(-94.13, -130.63) * mm});
            skLineSegment(sketch, "E16.6.0.13", {"start": v(-94.13, -150.63) * mm, "end": v(-99.9, -140.63) * mm});
            skLineSegment(sketch, "E16.9.0.13", {"start": v(-82.58, -150.62) * mm, "end": v(-94.13, -150.62) * mm});
            skLineSegment(sketch, "E16.12.0.13", {"start": v(-76.8, -140.62) * mm, "end": v(-82.58, -150.62) * mm});
            skLineSegment(sketch, "E16.15.0.13", {"start": v(-82.58, -130.62) * mm, "end": v(-76.8, -140.62) * mm});
            skLineSegment(sketch, "E16.18.0.13", {"start": v(-80.42, -129.38) * mm, "end": v(-74.64, -119.38) * mm});
            skLineSegment(sketch, "E16.21.0.13", {"start": v(-74.64, -139.37) * mm, "end": v(-80.42, -129.38) * mm});
            skLineSegment(sketch, "E16.24.0.13", {"start": v(-74.64, -119.37) * mm, "end": v(-63.1, -119.37) * mm});
            skLineSegment(sketch, "E16.27.0.13", {"start": v(-63.1, -119.38) * mm, "end": v(-57.32, -129.37) * mm});
            skLineSegment(sketch, "E16.30.0.13", {"start": v(-57.32, -129.38) * mm, "end": v(-63.1, -139.38) * mm});
            skLineSegment(sketch, "E16.33.0.13", {"start": v(-63.1, -139.38) * mm, "end": v(-74.64, -139.38) * mm});
            skLineSegment(sketch, "E16.0.0.14", {"start": v(-94.13, -153.12) * mm, "end": v(-82.58, -153.12) * mm});
            skLineSegment(sketch, "E16.3.0.14", {"start": v(-99.9, -163.13) * mm, "end": v(-94.13, -153.13) * mm});
            skLineSegment(sketch, "E16.6.0.14", {"start": v(-94.13, -173.13) * mm, "end": v(-99.9, -163.13) * mm});
            skLineSegment(sketch, "E16.9.0.14", {"start": v(-82.58, -173.12) * mm, "end": v(-94.13, -173.12) * mm});
            skLineSegment(sketch, "E16.12.0.14", {"start": v(-76.8, -163.13) * mm, "end": v(-82.58, -173.12) * mm});
            skLineSegment(sketch, "E16.15.0.14", {"start": v(-82.58, -153.12) * mm, "end": v(-76.8, -163.12) * mm});
            skLineSegment(sketch, "E16.18.0.14", {"start": v(-80.42, -151.88) * mm, "end": v(-74.64, -141.88) * mm});
            skLineSegment(sketch, "E16.21.0.14", {"start": v(-74.64, -161.87) * mm, "end": v(-80.42, -151.88) * mm});
            skLineSegment(sketch, "E16.24.0.14", {"start": v(-74.64, -141.88) * mm, "end": v(-63.1, -141.88) * mm});
            skLineSegment(sketch, "E16.27.0.14", {"start": v(-63.1, -141.88) * mm, "end": v(-57.32, -151.87) * mm});
            skLineSegment(sketch, "E16.30.0.14", {"start": v(-57.32, -151.88) * mm, "end": v(-63.1, -161.88) * mm});
            skLineSegment(sketch, "E16.33.0.14", {"start": v(-63.1, -161.88) * mm, "end": v(-74.64, -161.88) * mm});
            skLineSegment(sketch, "E16.0.1.2", {"start": v(-54.82, 116.87) * mm, "end": v(-43.28, 116.87) * mm});
            skLineSegment(sketch, "E16.3.1.2", {"start": v(-60.6, 106.87) * mm, "end": v(-54.82, 116.87) * mm});
            skLineSegment(sketch, "E16.6.1.2", {"start": v(-54.82, 96.87) * mm, "end": v(-60.6, 106.87) * mm});
            skLineSegment(sketch, "E16.9.1.2", {"start": v(-43.28, 96.87) * mm, "end": v(-54.82, 96.87) * mm});
            skLineSegment(sketch, "E16.12.1.2", {"start": v(-37.5, 106.87) * mm, "end": v(-43.28, 96.87) * mm});
            skLineSegment(sketch, "E16.15.1.2", {"start": v(-43.28, 116.87) * mm, "end": v(-37.5, 106.87) * mm});
            skLineSegment(sketch, "E16.18.1.2", {"start": v(-41.11, 118.12) * mm, "end": v(-35.34, 128.12) * mm});
            skLineSegment(sketch, "E16.21.1.2", {"start": v(-35.34, 108.12) * mm, "end": v(-41.11, 118.12) * mm});
            skLineSegment(sketch, "E16.24.1.2", {"start": v(-35.34, 128.12) * mm, "end": v(-23.79, 128.12) * mm});
            skLineSegment(sketch, "E16.27.1.2", {"start": v(-23.79, 128.12) * mm, "end": v(-18.02, 118.12) * mm});
            skLineSegment(sketch, "E16.30.1.2", {"start": v(-18.02, 118.12) * mm, "end": v(-23.79, 108.12) * mm});
            skLineSegment(sketch, "E16.33.1.2", {"start": v(-23.79, 108.12) * mm, "end": v(-35.34, 108.12) * mm});
            skLineSegment(sketch, "E16.0.1.3", {"start": v(-54.82, 94.37) * mm, "end": v(-43.28, 94.37) * mm});
            skLineSegment(sketch, "E16.3.1.3", {"start": v(-60.6, 84.37) * mm, "end": v(-54.82, 94.37) * mm});
            skLineSegment(sketch, "E16.6.1.3", {"start": v(-54.82, 74.37) * mm, "end": v(-60.6, 84.37) * mm});
            skLineSegment(sketch, "E16.9.1.3", {"start": v(-43.28, 74.37) * mm, "end": v(-54.82, 74.37) * mm});
            skLineSegment(sketch, "E16.12.1.3", {"start": v(-37.5, 84.37) * mm, "end": v(-43.28, 74.37) * mm});
            skLineSegment(sketch, "E16.15.1.3", {"start": v(-43.28, 94.37) * mm, "end": v(-37.5, 84.37) * mm});
            skLineSegment(sketch, "E16.18.1.3", {"start": v(-41.11, 95.62) * mm, "end": v(-35.34, 105.62) * mm});
            skLineSegment(sketch, "E16.21.1.3", {"start": v(-35.34, 85.62) * mm, "end": v(-41.11, 95.62) * mm});
            skLineSegment(sketch, "E16.24.1.3", {"start": v(-35.34, 105.62) * mm, "end": v(-23.79, 105.62) * mm});
            skLineSegment(sketch, "E16.27.1.3", {"start": v(-23.79, 105.62) * mm, "end": v(-18.02, 95.62) * mm});
            skLineSegment(sketch, "E16.30.1.3", {"start": v(-18.02, 95.62) * mm, "end": v(-23.79, 85.62) * mm});
            skLineSegment(sketch, "E16.33.1.3", {"start": v(-23.79, 85.62) * mm, "end": v(-35.34, 85.62) * mm});
            skLineSegment(sketch, "E16.0.1.4", {"start": v(-54.82, 71.87) * mm, "end": v(-43.28, 71.87) * mm});
            skLineSegment(sketch, "E16.3.1.4", {"start": v(-60.6, 61.87) * mm, "end": v(-54.82, 71.87) * mm});
            skLineSegment(sketch, "E16.6.1.4", {"start": v(-54.82, 51.87) * mm, "end": v(-60.6, 61.87) * mm});
            skLineSegment(sketch, "E16.9.1.4", {"start": v(-43.28, 51.87) * mm, "end": v(-54.82, 51.87) * mm});
            skLineSegment(sketch, "E16.12.1.4", {"start": v(-37.5, 61.87) * mm, "end": v(-43.28, 51.87) * mm});
            skLineSegment(sketch, "E16.15.1.4", {"start": v(-43.28, 71.87) * mm, "end": v(-37.5, 61.87) * mm});
            skLineSegment(sketch, "E16.18.1.4", {"start": v(-41.11, 73.12) * mm, "end": v(-35.34, 83.12) * mm});
            skLineSegment(sketch, "E16.21.1.4", {"start": v(-35.34, 63.12) * mm, "end": v(-41.11, 73.12) * mm});
            skLineSegment(sketch, "E16.24.1.4", {"start": v(-35.34, 83.12) * mm, "end": v(-23.79, 83.12) * mm});
            skLineSegment(sketch, "E16.27.1.4", {"start": v(-23.79, 83.12) * mm, "end": v(-18.02, 73.12) * mm});
            skLineSegment(sketch, "E16.30.1.4", {"start": v(-18.02, 73.12) * mm, "end": v(-23.79, 63.12) * mm});
            skLineSegment(sketch, "E16.33.1.4", {"start": v(-23.79, 63.12) * mm, "end": v(-35.34, 63.12) * mm});
            skLineSegment(sketch, "E16.0.1.5", {"start": v(-54.82, 49.37) * mm, "end": v(-43.28, 49.37) * mm});
            skLineSegment(sketch, "E16.3.1.5", {"start": v(-60.6, 39.37) * mm, "end": v(-54.82, 49.37) * mm});
            skLineSegment(sketch, "E16.6.1.5", {"start": v(-54.82, 29.37) * mm, "end": v(-60.6, 39.37) * mm});
            skLineSegment(sketch, "E16.9.1.5", {"start": v(-43.28, 29.37) * mm, "end": v(-54.82, 29.37) * mm});
            skLineSegment(sketch, "E16.12.1.5", {"start": v(-37.5, 39.37) * mm, "end": v(-43.28, 29.37) * mm});
            skLineSegment(sketch, "E16.15.1.5", {"start": v(-43.28, 49.37) * mm, "end": v(-37.5, 39.37) * mm});
            skLineSegment(sketch, "E16.18.1.5", {"start": v(-41.11, 50.62) * mm, "end": v(-35.34, 60.62) * mm});
            skLineSegment(sketch, "E16.21.1.5", {"start": v(-35.34, 40.62) * mm, "end": v(-41.11, 50.62) * mm});
            skLineSegment(sketch, "E16.24.1.5", {"start": v(-35.34, 60.62) * mm, "end": v(-23.79, 60.62) * mm});
            skLineSegment(sketch, "E16.27.1.5", {"start": v(-23.79, 60.62) * mm, "end": v(-18.02, 50.62) * mm});
            skLineSegment(sketch, "E16.30.1.5", {"start": v(-18.02, 50.62) * mm, "end": v(-23.79, 40.62) * mm});
            skLineSegment(sketch, "E16.33.1.5", {"start": v(-23.79, 40.62) * mm, "end": v(-35.34, 40.62) * mm});
            skLineSegment(sketch, "E16.0.1.6", {"start": v(-54.82, 26.87) * mm, "end": v(-43.28, 26.87) * mm});
            skLineSegment(sketch, "E16.3.1.6", {"start": v(-60.6, 16.87) * mm, "end": v(-54.82, 26.87) * mm});
            skLineSegment(sketch, "E16.6.1.6", {"start": v(-54.82, 6.87) * mm, "end": v(-60.6, 16.87) * mm});
            skLineSegment(sketch, "E16.9.1.6", {"start": v(-43.28, 6.87) * mm, "end": v(-54.82, 6.87) * mm});
            skLineSegment(sketch, "E16.12.1.6", {"start": v(-37.5, 16.87) * mm, "end": v(-43.28, 6.87) * mm});
            skLineSegment(sketch, "E16.15.1.6", {"start": v(-43.28, 26.87) * mm, "end": v(-37.5, 16.87) * mm});
            skLineSegment(sketch, "E16.18.1.6", {"start": v(-41.11, 28.12) * mm, "end": v(-35.34, 38.12) * mm});
            skLineSegment(sketch, "E16.21.1.6", {"start": v(-35.34, 18.12) * mm, "end": v(-41.11, 28.12) * mm});
            skLineSegment(sketch, "E16.24.1.6", {"start": v(-35.34, 38.12) * mm, "end": v(-23.79, 38.12) * mm});
            skLineSegment(sketch, "E16.27.1.6", {"start": v(-23.79, 38.12) * mm, "end": v(-18.02, 28.12) * mm});
            skLineSegment(sketch, "E16.30.1.6", {"start": v(-18.02, 28.12) * mm, "end": v(-23.79, 18.12) * mm});
            skLineSegment(sketch, "E16.33.1.6", {"start": v(-23.79, 18.12) * mm, "end": v(-35.34, 18.12) * mm});
            skLineSegment(sketch, "E16.0.1.7", {"start": v(-54.82, 4.37) * mm, "end": v(-43.28, 4.37) * mm});
            skLineSegment(sketch, "E16.3.1.7", {"start": v(-60.6, -5.63) * mm, "end": v(-54.82, 4.37) * mm});
            skLineSegment(sketch, "E16.6.1.7", {"start": v(-54.82, -15.63) * mm, "end": v(-60.6, -5.63) * mm});
            skLineSegment(sketch, "E16.9.1.7", {"start": v(-43.28, -15.63) * mm, "end": v(-54.82, -15.63) * mm});
            skLineSegment(sketch, "E16.12.1.7", {"start": v(-37.5, -5.63) * mm, "end": v(-43.28, -15.63) * mm});
            skLineSegment(sketch, "E16.15.1.7", {"start": v(-43.28, 4.37) * mm, "end": v(-37.5, -5.63) * mm});
            skLineSegment(sketch, "E16.18.1.7", {"start": v(-41.11, 5.62) * mm, "end": v(-35.34, 15.62) * mm});
            skLineSegment(sketch, "E16.21.1.7", {"start": v(-35.34, -4.38) * mm, "end": v(-41.11, 5.62) * mm});
            skLineSegment(sketch, "E16.24.1.7", {"start": v(-35.34, 15.62) * mm, "end": v(-23.79, 15.62) * mm});
            skLineSegment(sketch, "E16.27.1.7", {"start": v(-23.79, 15.62) * mm, "end": v(-18.02, 5.62) * mm});
            skLineSegment(sketch, "E16.30.1.7", {"start": v(-18.02, 5.62) * mm, "end": v(-23.79, -4.38) * mm});
            skLineSegment(sketch, "E16.33.1.7", {"start": v(-23.79, -4.38) * mm, "end": v(-35.34, -4.38) * mm});
            skLineSegment(sketch, "E16.0.1.8", {"start": v(-54.82, -18.13) * mm, "end": v(-43.28, -18.13) * mm});
            skLineSegment(sketch, "E16.3.1.8", {"start": v(-60.6, -28.13) * mm, "end": v(-54.82, -18.13) * mm});
            skLineSegment(sketch, "E16.6.1.8", {"start": v(-54.82, -38.13) * mm, "end": v(-60.6, -28.13) * mm});
            skLineSegment(sketch, "E16.9.1.8", {"start": v(-43.28, -38.13) * mm, "end": v(-54.82, -38.13) * mm});
            skLineSegment(sketch, "E16.12.1.8", {"start": v(-37.5, -28.13) * mm, "end": v(-43.28, -38.13) * mm});
            skLineSegment(sketch, "E16.15.1.8", {"start": v(-43.28, -18.13) * mm, "end": v(-37.5, -28.13) * mm});
            skLineSegment(sketch, "E16.18.1.8", {"start": v(-41.11, -16.88) * mm, "end": v(-35.34, -6.88) * mm});
            skLineSegment(sketch, "E16.21.1.8", {"start": v(-35.34, -26.88) * mm, "end": v(-41.11, -16.88) * mm});
            skLineSegment(sketch, "E16.24.1.8", {"start": v(-35.34, -6.88) * mm, "end": v(-23.79, -6.88) * mm});
            skLineSegment(sketch, "E16.27.1.8", {"start": v(-23.79, -6.88) * mm, "end": v(-18.02, -16.88) * mm});
            skLineSegment(sketch, "E16.30.1.8", {"start": v(-18.02, -16.88) * mm, "end": v(-23.79, -26.88) * mm});
            skLineSegment(sketch, "E16.33.1.8", {"start": v(-23.79, -26.88) * mm, "end": v(-35.34, -26.88) * mm});
            skLineSegment(sketch, "E16.0.1.9", {"start": v(-54.82, -40.63) * mm, "end": v(-43.28, -40.63) * mm});
            skLineSegment(sketch, "E16.3.1.9", {"start": v(-60.6, -50.63) * mm, "end": v(-54.82, -40.63) * mm});
            skLineSegment(sketch, "E16.6.1.9", {"start": v(-54.82, -60.63) * mm, "end": v(-60.6, -50.63) * mm});
            skLineSegment(sketch, "E16.9.1.9", {"start": v(-43.28, -60.63) * mm, "end": v(-54.82, -60.63) * mm});
            skLineSegment(sketch, "E16.12.1.9", {"start": v(-37.5, -50.63) * mm, "end": v(-43.28, -60.63) * mm});
            skLineSegment(sketch, "E16.15.1.9", {"start": v(-43.28, -40.63) * mm, "end": v(-37.5, -50.63) * mm});
            skLineSegment(sketch, "E16.18.1.9", {"start": v(-41.11, -39.38) * mm, "end": v(-35.34, -29.38) * mm});
            skLineSegment(sketch, "E16.21.1.9", {"start": v(-35.34, -49.38) * mm, "end": v(-41.11, -39.38) * mm});
            skLineSegment(sketch, "E16.24.1.9", {"start": v(-35.34, -29.38) * mm, "end": v(-23.79, -29.38) * mm});
            skLineSegment(sketch, "E16.27.1.9", {"start": v(-23.79, -29.38) * mm, "end": v(-18.02, -39.38) * mm});
            skLineSegment(sketch, "E16.30.1.9", {"start": v(-18.02, -39.38) * mm, "end": v(-23.79, -49.38) * mm});
            skLineSegment(sketch, "E16.33.1.9", {"start": v(-23.79, -49.38) * mm, "end": v(-35.34, -49.38) * mm});
            skLineSegment(sketch, "E16.0.1.10", {"start": v(-54.82, -63.13) * mm, "end": v(-43.28, -63.13) * mm});
            skLineSegment(sketch, "E16.3.1.10", {"start": v(-60.6, -73.13) * mm, "end": v(-54.82, -63.13) * mm});
            skLineSegment(sketch, "E16.6.1.10", {"start": v(-54.82, -83.13) * mm, "end": v(-60.6, -73.13) * mm});
            skLineSegment(sketch, "E16.9.1.10", {"start": v(-43.28, -83.13) * mm, "end": v(-54.82, -83.13) * mm});
            skLineSegment(sketch, "E16.12.1.10", {"start": v(-37.5, -73.13) * mm, "end": v(-43.28, -83.13) * mm});
            skLineSegment(sketch, "E16.15.1.10", {"start": v(-43.28, -63.13) * mm, "end": v(-37.5, -73.13) * mm});
            skLineSegment(sketch, "E16.18.1.10", {"start": v(-41.11, -61.88) * mm, "end": v(-35.34, -51.88) * mm});
            skLineSegment(sketch, "E16.21.1.10", {"start": v(-35.34, -71.88) * mm, "end": v(-41.11, -61.88) * mm});
            skLineSegment(sketch, "E16.24.1.10", {"start": v(-35.34, -51.88) * mm, "end": v(-23.79, -51.88) * mm});
            skLineSegment(sketch, "E16.27.1.10", {"start": v(-23.79, -51.88) * mm, "end": v(-18.02, -61.88) * mm});
            skLineSegment(sketch, "E16.30.1.10", {"start": v(-18.02, -61.88) * mm, "end": v(-23.79, -71.88) * mm});
            skLineSegment(sketch, "E16.33.1.10", {"start": v(-23.79, -71.88) * mm, "end": v(-35.34, -71.88) * mm});
            skLineSegment(sketch, "E16.0.1.11", {"start": v(-54.82, -85.63) * mm, "end": v(-43.28, -85.63) * mm});
            skLineSegment(sketch, "E16.3.1.11", {"start": v(-60.6, -95.63) * mm, "end": v(-54.82, -85.63) * mm});
            skLineSegment(sketch, "E16.6.1.11", {"start": v(-54.82, -105.63) * mm, "end": v(-60.6, -95.63) * mm});
            skLineSegment(sketch, "E16.9.1.11", {"start": v(-43.28, -105.63) * mm, "end": v(-54.82, -105.63) * mm});
            skLineSegment(sketch, "E16.12.1.11", {"start": v(-37.5, -95.63) * mm, "end": v(-43.28, -105.63) * mm});
            skLineSegment(sketch, "E16.15.1.11", {"start": v(-43.28, -85.62) * mm, "end": v(-37.5, -95.63) * mm});
            skLineSegment(sketch, "E16.18.1.11", {"start": v(-41.11, -84.38) * mm, "end": v(-35.34, -74.38) * mm});
            skLineSegment(sketch, "E16.21.1.11", {"start": v(-35.34, -94.38) * mm, "end": v(-41.11, -84.38) * mm});
            skLineSegment(sketch, "E16.24.1.11", {"start": v(-35.34, -74.38) * mm, "end": v(-23.79, -74.38) * mm});
            skLineSegment(sketch, "E16.27.1.11", {"start": v(-23.79, -74.38) * mm, "end": v(-18.02, -84.38) * mm});
            skLineSegment(sketch, "E16.30.1.11", {"start": v(-18.02, -84.38) * mm, "end": v(-23.79, -94.38) * mm});
            skLineSegment(sketch, "E16.33.1.11", {"start": v(-23.79, -94.38) * mm, "end": v(-35.34, -94.38) * mm});
            skLineSegment(sketch, "E16.0.1.12", {"start": v(-54.82, -108.13) * mm, "end": v(-43.28, -108.13) * mm});
            skLineSegment(sketch, "E16.3.1.12", {"start": v(-60.6, -118.13) * mm, "end": v(-54.82, -108.13) * mm});
            skLineSegment(sketch, "E16.6.1.12", {"start": v(-54.82, -128.13) * mm, "end": v(-60.6, -118.13) * mm});
            skLineSegment(sketch, "E16.9.1.12", {"start": v(-43.28, -128.13) * mm, "end": v(-54.82, -128.13) * mm});
            skLineSegment(sketch, "E16.12.1.12", {"start": v(-37.5, -118.13) * mm, "end": v(-43.28, -128.13) * mm});
            skLineSegment(sketch, "E16.15.1.12", {"start": v(-43.28, -108.12) * mm, "end": v(-37.5, -118.13) * mm});
            skLineSegment(sketch, "E16.18.1.12", {"start": v(-41.11, -106.88) * mm, "end": v(-35.34, -96.88) * mm});
            skLineSegment(sketch, "E16.21.1.12", {"start": v(-35.34, -116.87) * mm, "end": v(-41.11, -106.88) * mm});
            skLineSegment(sketch, "E16.24.1.12", {"start": v(-35.34, -96.88) * mm, "end": v(-23.79, -96.88) * mm});
            skLineSegment(sketch, "E16.27.1.12", {"start": v(-23.79, -96.88) * mm, "end": v(-18.02, -106.88) * mm});
            skLineSegment(sketch, "E16.30.1.12", {"start": v(-18.02, -106.88) * mm, "end": v(-23.79, -116.88) * mm});
            skLineSegment(sketch, "E16.33.1.12", {"start": v(-23.79, -116.88) * mm, "end": v(-35.34, -116.88) * mm});
            skLineSegment(sketch, "E16.0.1.13", {"start": v(-54.82, -130.62) * mm, "end": v(-43.28, -130.62) * mm});
            skLineSegment(sketch, "E16.3.1.13", {"start": v(-60.6, -140.63) * mm, "end": v(-54.82, -130.63) * mm});
            skLineSegment(sketch, "E16.6.1.13", {"start": v(-54.82, -150.63) * mm, "end": v(-60.6, -140.62) * mm});
            skLineSegment(sketch, "E16.9.1.13", {"start": v(-43.28, -150.62) * mm, "end": v(-54.82, -150.62) * mm});
            skLineSegment(sketch, "E16.12.1.13", {"start": v(-37.5, -140.62) * mm, "end": v(-43.28, -150.62) * mm});
            skLineSegment(sketch, "E16.15.1.13", {"start": v(-43.28, -130.62) * mm, "end": v(-37.5, -140.62) * mm});
            skLineSegment(sketch, "E16.18.1.13", {"start": v(-41.11, -129.38) * mm, "end": v(-35.34, -119.38) * mm});
            skLineSegment(sketch, "E16.21.1.13", {"start": v(-35.34, -139.37) * mm, "end": v(-41.11, -129.38) * mm});
            skLineSegment(sketch, "E16.24.1.13", {"start": v(-35.34, -119.37) * mm, "end": v(-23.79, -119.37) * mm});
            skLineSegment(sketch, "E16.27.1.13", {"start": v(-23.79, -119.38) * mm, "end": v(-18.02, -129.37) * mm});
            skLineSegment(sketch, "E16.30.1.13", {"start": v(-18.02, -129.38) * mm, "end": v(-23.79, -139.38) * mm});
            skLineSegment(sketch, "E16.33.1.13", {"start": v(-23.79, -139.38) * mm, "end": v(-35.34, -139.38) * mm});
            skLineSegment(sketch, "E16.0.1.14", {"start": v(-54.82, -153.12) * mm, "end": v(-43.28, -153.12) * mm});
            skLineSegment(sketch, "E16.3.1.14", {"start": v(-60.6, -163.13) * mm, "end": v(-54.82, -153.13) * mm});
            skLineSegment(sketch, "E16.6.1.14", {"start": v(-54.82, -173.13) * mm, "end": v(-60.6, -163.13) * mm});
            skLineSegment(sketch, "E16.9.1.14", {"start": v(-43.28, -173.12) * mm, "end": v(-54.82, -173.12) * mm});
            skLineSegment(sketch, "E16.12.1.14", {"start": v(-37.5, -163.13) * mm, "end": v(-43.28, -173.12) * mm});
            skLineSegment(sketch, "E16.15.1.14", {"start": v(-43.28, -153.12) * mm, "end": v(-37.5, -163.12) * mm});
            skLineSegment(sketch, "E16.18.1.14", {"start": v(-41.11, -151.88) * mm, "end": v(-35.34, -141.88) * mm});
            skLineSegment(sketch, "E16.21.1.14", {"start": v(-35.34, -161.87) * mm, "end": v(-41.11, -151.88) * mm});
            skLineSegment(sketch, "E16.24.1.14", {"start": v(-35.34, -141.88) * mm, "end": v(-23.79, -141.88) * mm});
            skLineSegment(sketch, "E16.27.1.14", {"start": v(-23.79, -141.88) * mm, "end": v(-18.02, -151.87) * mm});
            skLineSegment(sketch, "E16.30.1.14", {"start": v(-18.02, -151.88) * mm, "end": v(-23.79, -161.88) * mm});
            skLineSegment(sketch, "E16.33.1.14", {"start": v(-23.79, -161.88) * mm, "end": v(-35.34, -161.88) * mm});
            skLineSegment(sketch, "E16.0.2.2", {"start": v(-15.52, 116.87) * mm, "end": v(-3.97, 116.87) * mm});
            skLineSegment(sketch, "E16.3.2.2", {"start": v(-21.29, 106.87) * mm, "end": v(-15.52, 116.87) * mm});
            skLineSegment(sketch, "E16.6.2.2", {"start": v(-15.52, 96.87) * mm, "end": v(-21.29, 106.87) * mm});
            skLineSegment(sketch, "E16.9.2.2", {"start": v(-3.97, 96.87) * mm, "end": v(-15.52, 96.87) * mm});
            skLineSegment(sketch, "E16.12.2.2", {"start": v(1.8, 106.87) * mm, "end": v(-3.97, 96.87) * mm});
            skLineSegment(sketch, "E16.15.2.2", {"start": v(-3.97, 116.87) * mm, "end": v(1.8, 106.87) * mm});
            skLineSegment(sketch, "E16.18.2.2", {"start": v(-1.8, 118.12) * mm, "end": v(3.97, 128.12) * mm});
            skLineSegment(sketch, "E16.21.2.2", {"start": v(3.97, 108.12) * mm, "end": v(-1.8, 118.12) * mm});
            skLineSegment(sketch, "E16.24.2.2", {"start": v(3.97, 128.12) * mm, "end": v(15.52, 128.12) * mm});
            skLineSegment(sketch, "E16.27.2.2", {"start": v(15.52, 128.12) * mm, "end": v(21.29, 118.12) * mm});
            skLineSegment(sketch, "E16.30.2.2", {"start": v(21.29, 118.12) * mm, "end": v(15.52, 108.12) * mm});
            skLineSegment(sketch, "E16.33.2.2", {"start": v(15.52, 108.12) * mm, "end": v(3.97, 108.12) * mm});
            skLineSegment(sketch, "E16.0.2.3", {"start": v(-15.52, 94.37) * mm, "end": v(-3.97, 94.37) * mm});
            skLineSegment(sketch, "E16.3.2.3", {"start": v(-21.29, 84.37) * mm, "end": v(-15.52, 94.37) * mm});
            skLineSegment(sketch, "E16.6.2.3", {"start": v(-15.52, 74.37) * mm, "end": v(-21.29, 84.37) * mm});
            skLineSegment(sketch, "E16.9.2.3", {"start": v(-3.97, 74.37) * mm, "end": v(-15.52, 74.37) * mm});
            skLineSegment(sketch, "E16.12.2.3", {"start": v(1.8, 84.37) * mm, "end": v(-3.97, 74.37) * mm});
            skLineSegment(sketch, "E16.15.2.3", {"start": v(-3.97, 94.37) * mm, "end": v(1.8, 84.37) * mm});
            skLineSegment(sketch, "E16.18.2.3", {"start": v(-1.8, 95.62) * mm, "end": v(3.97, 105.62) * mm});
            skLineSegment(sketch, "E16.21.2.3", {"start": v(3.97, 85.62) * mm, "end": v(-1.8, 95.62) * mm});
            skLineSegment(sketch, "E16.24.2.3", {"start": v(3.97, 105.62) * mm, "end": v(15.52, 105.62) * mm});
            skLineSegment(sketch, "E16.27.2.3", {"start": v(15.52, 105.62) * mm, "end": v(21.29, 95.62) * mm});
            skLineSegment(sketch, "E16.30.2.3", {"start": v(21.29, 95.62) * mm, "end": v(15.52, 85.62) * mm});
            skLineSegment(sketch, "E16.33.2.3", {"start": v(15.52, 85.62) * mm, "end": v(3.97, 85.62) * mm});
            skLineSegment(sketch, "E16.0.2.4", {"start": v(-15.52, 71.87) * mm, "end": v(-3.97, 71.87) * mm});
            skLineSegment(sketch, "E16.3.2.4", {"start": v(-21.29, 61.87) * mm, "end": v(-15.52, 71.87) * mm});
            skLineSegment(sketch, "E16.6.2.4", {"start": v(-15.52, 51.87) * mm, "end": v(-21.29, 61.87) * mm});
            skLineSegment(sketch, "E16.9.2.4", {"start": v(-3.97, 51.87) * mm, "end": v(-15.52, 51.87) * mm});
            skLineSegment(sketch, "E16.12.2.4", {"start": v(1.8, 61.87) * mm, "end": v(-3.97, 51.87) * mm});
            skLineSegment(sketch, "E16.15.2.4", {"start": v(-3.97, 71.87) * mm, "end": v(1.8, 61.87) * mm});
            skLineSegment(sketch, "E16.18.2.4", {"start": v(-1.8, 73.12) * mm, "end": v(3.97, 83.12) * mm});
            skLineSegment(sketch, "E16.21.2.4", {"start": v(3.97, 63.12) * mm, "end": v(-1.8, 73.12) * mm});
            skLineSegment(sketch, "E16.24.2.4", {"start": v(3.97, 83.12) * mm, "end": v(15.52, 83.12) * mm});
            skLineSegment(sketch, "E16.27.2.4", {"start": v(15.52, 83.12) * mm, "end": v(21.29, 73.12) * mm});
            skLineSegment(sketch, "E16.30.2.4", {"start": v(21.29, 73.12) * mm, "end": v(15.52, 63.12) * mm});
            skLineSegment(sketch, "E16.33.2.4", {"start": v(15.52, 63.12) * mm, "end": v(3.97, 63.12) * mm});
            skLineSegment(sketch, "E16.0.2.5", {"start": v(-15.52, 49.37) * mm, "end": v(-3.97, 49.37) * mm});
            skLineSegment(sketch, "E16.3.2.5", {"start": v(-21.29, 39.37) * mm, "end": v(-15.52, 49.37) * mm});
            skLineSegment(sketch, "E16.6.2.5", {"start": v(-15.52, 29.37) * mm, "end": v(-21.29, 39.37) * mm});
            skLineSegment(sketch, "E16.9.2.5", {"start": v(-3.97, 29.37) * mm, "end": v(-15.52, 29.37) * mm});
            skLineSegment(sketch, "E16.12.2.5", {"start": v(1.8, 39.37) * mm, "end": v(-3.97, 29.37) * mm});
            skLineSegment(sketch, "E16.15.2.5", {"start": v(-3.97, 49.37) * mm, "end": v(1.8, 39.37) * mm});
            skLineSegment(sketch, "E16.18.2.5", {"start": v(-1.8, 50.62) * mm, "end": v(3.97, 60.62) * mm});
            skLineSegment(sketch, "E16.21.2.5", {"start": v(3.97, 40.62) * mm, "end": v(-1.8, 50.62) * mm});
            skLineSegment(sketch, "E16.24.2.5", {"start": v(3.97, 60.62) * mm, "end": v(15.52, 60.62) * mm});
            skLineSegment(sketch, "E16.27.2.5", {"start": v(15.52, 60.62) * mm, "end": v(21.29, 50.62) * mm});
            skLineSegment(sketch, "E16.30.2.5", {"start": v(21.29, 50.62) * mm, "end": v(15.52, 40.62) * mm});
            skLineSegment(sketch, "E16.33.2.5", {"start": v(15.52, 40.62) * mm, "end": v(3.97, 40.62) * mm});
            skLineSegment(sketch, "E16.0.2.6", {"start": v(-15.52, 26.87) * mm, "end": v(-3.97, 26.87) * mm});
            skLineSegment(sketch, "E16.3.2.6", {"start": v(-21.29, 16.87) * mm, "end": v(-15.52, 26.87) * mm});
            skLineSegment(sketch, "E16.6.2.6", {"start": v(-15.52, 6.87) * mm, "end": v(-21.29, 16.87) * mm});
            skLineSegment(sketch, "E16.9.2.6", {"start": v(-3.97, 6.87) * mm, "end": v(-15.52, 6.87) * mm});
            skLineSegment(sketch, "E16.12.2.6", {"start": v(1.8, 16.87) * mm, "end": v(-3.97, 6.87) * mm});
            skLineSegment(sketch, "E16.15.2.6", {"start": v(-3.97, 26.87) * mm, "end": v(1.8, 16.87) * mm});
            skLineSegment(sketch, "E16.18.2.6", {"start": v(-1.8, 28.12) * mm, "end": v(3.97, 38.12) * mm});
            skLineSegment(sketch, "E16.21.2.6", {"start": v(3.97, 18.12) * mm, "end": v(-1.8, 28.12) * mm});
            skLineSegment(sketch, "E16.24.2.6", {"start": v(3.97, 38.12) * mm, "end": v(15.52, 38.12) * mm});
            skLineSegment(sketch, "E16.27.2.6", {"start": v(15.52, 38.12) * mm, "end": v(21.29, 28.12) * mm});
            skLineSegment(sketch, "E16.30.2.6", {"start": v(21.29, 28.12) * mm, "end": v(15.52, 18.12) * mm});
            skLineSegment(sketch, "E16.33.2.6", {"start": v(15.52, 18.12) * mm, "end": v(3.97, 18.12) * mm});
            skLineSegment(sketch, "E16.0.2.7", {"start": v(-15.52, 4.37) * mm, "end": v(-3.97, 4.37) * mm});
            skLineSegment(sketch, "E16.3.2.7", {"start": v(-21.29, -5.63) * mm, "end": v(-15.52, 4.37) * mm});
            skLineSegment(sketch, "E16.6.2.7", {"start": v(-15.52, -15.63) * mm, "end": v(-21.29, -5.63) * mm});
            skLineSegment(sketch, "E16.9.2.7", {"start": v(-3.97, -15.63) * mm, "end": v(-15.52, -15.63) * mm});
            skLineSegment(sketch, "E16.12.2.7", {"start": v(1.8, -5.63) * mm, "end": v(-3.97, -15.63) * mm});
            skLineSegment(sketch, "E16.15.2.7", {"start": v(-3.97, 4.37) * mm, "end": v(1.8, -5.63) * mm});
            skLineSegment(sketch, "E16.18.2.7", {"start": v(-1.8, 5.62) * mm, "end": v(3.97, 15.62) * mm});
            skLineSegment(sketch, "E16.21.2.7", {"start": v(3.97, -4.38) * mm, "end": v(-1.8, 5.62) * mm});
            skLineSegment(sketch, "E16.24.2.7", {"start": v(3.97, 15.62) * mm, "end": v(15.52, 15.62) * mm});
            skLineSegment(sketch, "E16.27.2.7", {"start": v(15.52, 15.62) * mm, "end": v(21.29, 5.62) * mm});
            skLineSegment(sketch, "E16.30.2.7", {"start": v(21.29, 5.62) * mm, "end": v(15.52, -4.38) * mm});
            skLineSegment(sketch, "E16.33.2.7", {"start": v(15.52, -4.38) * mm, "end": v(3.97, -4.38) * mm});
            skLineSegment(sketch, "E16.0.2.8", {"start": v(-15.52, -18.13) * mm, "end": v(-3.97, -18.13) * mm});
            skLineSegment(sketch, "E16.3.2.8", {"start": v(-21.29, -28.13) * mm, "end": v(-15.52, -18.13) * mm});
            skLineSegment(sketch, "E16.6.2.8", {"start": v(-15.52, -38.13) * mm, "end": v(-21.29, -28.13) * mm});
            skLineSegment(sketch, "E16.9.2.8", {"start": v(-3.97, -38.13) * mm, "end": v(-15.52, -38.13) * mm});
            skLineSegment(sketch, "E16.12.2.8", {"start": v(1.8, -28.13) * mm, "end": v(-3.97, -38.13) * mm});
            skLineSegment(sketch, "E16.15.2.8", {"start": v(-3.97, -18.13) * mm, "end": v(1.8, -28.13) * mm});
            skLineSegment(sketch, "E16.18.2.8", {"start": v(-1.8, -16.88) * mm, "end": v(3.97, -6.88) * mm});
            skLineSegment(sketch, "E16.21.2.8", {"start": v(3.97, -26.88) * mm, "end": v(-1.8, -16.88) * mm});
            skLineSegment(sketch, "E16.24.2.8", {"start": v(3.97, -6.88) * mm, "end": v(15.52, -6.88) * mm});
            skLineSegment(sketch, "E16.27.2.8", {"start": v(15.52, -6.88) * mm, "end": v(21.29, -16.88) * mm});
            skLineSegment(sketch, "E16.30.2.8", {"start": v(21.29, -16.88) * mm, "end": v(15.52, -26.88) * mm});
            skLineSegment(sketch, "E16.33.2.8", {"start": v(15.52, -26.88) * mm, "end": v(3.97, -26.88) * mm});
            skLineSegment(sketch, "E16.0.2.9", {"start": v(-15.52, -40.63) * mm, "end": v(-3.97, -40.63) * mm});
            skLineSegment(sketch, "E16.3.2.9", {"start": v(-21.29, -50.63) * mm, "end": v(-15.52, -40.63) * mm});
            skLineSegment(sketch, "E16.6.2.9", {"start": v(-15.52, -60.63) * mm, "end": v(-21.29, -50.63) * mm});
            skLineSegment(sketch, "E16.9.2.9", {"start": v(-3.97, -60.63) * mm, "end": v(-15.52, -60.63) * mm});
            skLineSegment(sketch, "E16.12.2.9", {"start": v(1.8, -50.63) * mm, "end": v(-3.97, -60.63) * mm});
            skLineSegment(sketch, "E16.15.2.9", {"start": v(-3.97, -40.63) * mm, "end": v(1.8, -50.63) * mm});
            skLineSegment(sketch, "E16.18.2.9", {"start": v(-1.8, -39.38) * mm, "end": v(3.97, -29.38) * mm});
            skLineSegment(sketch, "E16.21.2.9", {"start": v(3.97, -49.38) * mm, "end": v(-1.8, -39.38) * mm});
            skLineSegment(sketch, "E16.24.2.9", {"start": v(3.97, -29.38) * mm, "end": v(15.52, -29.38) * mm});
            skLineSegment(sketch, "E16.27.2.9", {"start": v(15.52, -29.38) * mm, "end": v(21.29, -39.38) * mm});
            skLineSegment(sketch, "E16.30.2.9", {"start": v(21.29, -39.38) * mm, "end": v(15.52, -49.38) * mm});
            skLineSegment(sketch, "E16.33.2.9", {"start": v(15.52, -49.38) * mm, "end": v(3.97, -49.38) * mm});
            skLineSegment(sketch, "E16.0.2.10", {"start": v(-15.52, -63.13) * mm, "end": v(-3.97, -63.13) * mm});
            skLineSegment(sketch, "E16.3.2.10", {"start": v(-21.29, -73.13) * mm, "end": v(-15.52, -63.13) * mm});
            skLineSegment(sketch, "E16.6.2.10", {"start": v(-15.52, -83.13) * mm, "end": v(-21.29, -73.13) * mm});
            skLineSegment(sketch, "E16.9.2.10", {"start": v(-3.97, -83.13) * mm, "end": v(-15.52, -83.13) * mm});
            skLineSegment(sketch, "E16.12.2.10", {"start": v(1.8, -73.13) * mm, "end": v(-3.97, -83.13) * mm});
            skLineSegment(sketch, "E16.15.2.10", {"start": v(-3.97, -63.13) * mm, "end": v(1.8, -73.13) * mm});
            skLineSegment(sketch, "E16.18.2.10", {"start": v(-1.8, -61.88) * mm, "end": v(3.97, -51.88) * mm});
            skLineSegment(sketch, "E16.21.2.10", {"start": v(3.97, -71.88) * mm, "end": v(-1.8, -61.88) * mm});
            skLineSegment(sketch, "E16.24.2.10", {"start": v(3.97, -51.88) * mm, "end": v(15.52, -51.88) * mm});
            skLineSegment(sketch, "E16.27.2.10", {"start": v(15.52, -51.88) * mm, "end": v(21.29, -61.88) * mm});
            skLineSegment(sketch, "E16.30.2.10", {"start": v(21.29, -61.88) * mm, "end": v(15.52, -71.88) * mm});
            skLineSegment(sketch, "E16.33.2.10", {"start": v(15.52, -71.88) * mm, "end": v(3.97, -71.88) * mm});
            skLineSegment(sketch, "E16.0.2.11", {"start": v(-15.52, -85.63) * mm, "end": v(-3.97, -85.63) * mm});
            skLineSegment(sketch, "E16.3.2.11", {"start": v(-21.29, -95.63) * mm, "end": v(-15.52, -85.63) * mm});
            skLineSegment(sketch, "E16.6.2.11", {"start": v(-15.52, -105.63) * mm, "end": v(-21.29, -95.63) * mm});
            skLineSegment(sketch, "E16.9.2.11", {"start": v(-3.97, -105.63) * mm, "end": v(-15.52, -105.63) * mm});
            skLineSegment(sketch, "E16.12.2.11", {"start": v(1.8, -95.63) * mm, "end": v(-3.97, -105.63) * mm});
            skLineSegment(sketch, "E16.15.2.11", {"start": v(-3.97, -85.62) * mm, "end": v(1.8, -95.63) * mm});
            skLineSegment(sketch, "E16.18.2.11", {"start": v(-1.8, -84.38) * mm, "end": v(3.97, -74.38) * mm});
            skLineSegment(sketch, "E16.21.2.11", {"start": v(3.97, -94.38) * mm, "end": v(-1.8, -84.38) * mm});
            skLineSegment(sketch, "E16.24.2.11", {"start": v(3.97, -74.38) * mm, "end": v(15.52, -74.38) * mm});
            skLineSegment(sketch, "E16.27.2.11", {"start": v(15.52, -74.38) * mm, "end": v(21.29, -84.38) * mm});
            skLineSegment(sketch, "E16.30.2.11", {"start": v(21.29, -84.38) * mm, "end": v(15.52, -94.38) * mm});
            skLineSegment(sketch, "E16.33.2.11", {"start": v(15.52, -94.38) * mm, "end": v(3.97, -94.38) * mm});
            skLineSegment(sketch, "E16.0.2.12", {"start": v(-15.52, -108.13) * mm, "end": v(-3.97, -108.13) * mm});
            skLineSegment(sketch, "E16.3.2.12", {"start": v(-21.29, -118.13) * mm, "end": v(-15.52, -108.13) * mm});
            skLineSegment(sketch, "E16.6.2.12", {"start": v(-15.52, -128.13) * mm, "end": v(-21.29, -118.13) * mm});
            skLineSegment(sketch, "E16.9.2.12", {"start": v(-3.97, -128.13) * mm, "end": v(-15.52, -128.13) * mm});
            skLineSegment(sketch, "E16.12.2.12", {"start": v(1.8, -118.13) * mm, "end": v(-3.97, -128.13) * mm});
            skLineSegment(sketch, "E16.15.2.12", {"start": v(-3.97, -108.12) * mm, "end": v(1.8, -118.13) * mm});
            skLineSegment(sketch, "E16.18.2.12", {"start": v(-1.8, -106.88) * mm, "end": v(3.97, -96.88) * mm});
            skLineSegment(sketch, "E16.21.2.12", {"start": v(3.97, -116.87) * mm, "end": v(-1.8, -106.88) * mm});
            skLineSegment(sketch, "E16.24.2.12", {"start": v(3.97, -96.88) * mm, "end": v(15.52, -96.88) * mm});
            skLineSegment(sketch, "E16.27.2.12", {"start": v(15.52, -96.88) * mm, "end": v(21.29, -106.88) * mm});
            skLineSegment(sketch, "E16.30.2.12", {"start": v(21.29, -106.88) * mm, "end": v(15.52, -116.88) * mm});
            skLineSegment(sketch, "E16.33.2.12", {"start": v(15.52, -116.88) * mm, "end": v(3.97, -116.88) * mm});
            skLineSegment(sketch, "E16.0.2.13", {"start": v(-15.52, -130.62) * mm, "end": v(-3.97, -130.62) * mm});
            skLineSegment(sketch, "E16.3.2.13", {"start": v(-21.29, -140.63) * mm, "end": v(-15.52, -130.63) * mm});
            skLineSegment(sketch, "E16.6.2.13", {"start": v(-15.52, -150.63) * mm, "end": v(-21.29, -140.63) * mm});
            skLineSegment(sketch, "E16.9.2.13", {"start": v(-3.97, -150.62) * mm, "end": v(-15.52, -150.62) * mm});
            skLineSegment(sketch, "E16.12.2.13", {"start": v(1.8, -140.62) * mm, "end": v(-3.97, -150.62) * mm});
            skLineSegment(sketch, "E16.15.2.13", {"start": v(-3.97, -130.62) * mm, "end": v(1.8, -140.62) * mm});
            skLineSegment(sketch, "E16.18.2.13", {"start": v(-1.8, -129.38) * mm, "end": v(3.97, -119.38) * mm});
            skLineSegment(sketch, "E16.21.2.13", {"start": v(3.97, -139.37) * mm, "end": v(-1.8, -129.38) * mm});
            skLineSegment(sketch, "E16.24.2.13", {"start": v(3.97, -119.37) * mm, "end": v(15.52, -119.37) * mm});
            skLineSegment(sketch, "E16.27.2.13", {"start": v(15.52, -119.38) * mm, "end": v(21.29, -129.37) * mm});
            skLineSegment(sketch, "E16.30.2.13", {"start": v(21.29, -129.38) * mm, "end": v(15.52, -139.38) * mm});
            skLineSegment(sketch, "E16.33.2.13", {"start": v(15.52, -139.38) * mm, "end": v(3.97, -139.38) * mm});
            skLineSegment(sketch, "E16.0.2.14", {"start": v(-15.52, -153.12) * mm, "end": v(-3.97, -153.12) * mm});
            skLineSegment(sketch, "E16.3.2.14", {"start": v(-21.29, -163.13) * mm, "end": v(-15.52, -153.13) * mm});
            skLineSegment(sketch, "E16.6.2.14", {"start": v(-15.52, -173.13) * mm, "end": v(-21.29, -163.13) * mm});
            skLineSegment(sketch, "E16.9.2.14", {"start": v(-3.97, -173.12) * mm, "end": v(-15.52, -173.12) * mm});
            skLineSegment(sketch, "E16.12.2.14", {"start": v(1.8, -163.13) * mm, "end": v(-3.97, -173.12) * mm});
            skLineSegment(sketch, "E16.15.2.14", {"start": v(-3.97, -153.12) * mm, "end": v(1.8, -163.12) * mm});
            skLineSegment(sketch, "E16.18.2.14", {"start": v(-1.8, -151.88) * mm, "end": v(3.97, -141.88) * mm});
            skLineSegment(sketch, "E16.21.2.14", {"start": v(3.97, -161.87) * mm, "end": v(-1.8, -151.88) * mm});
            skLineSegment(sketch, "E16.24.2.14", {"start": v(3.97, -141.88) * mm, "end": v(15.52, -141.88) * mm});
            skLineSegment(sketch, "E16.27.2.14", {"start": v(15.52, -141.88) * mm, "end": v(21.29, -151.87) * mm});
            skLineSegment(sketch, "E16.30.2.14", {"start": v(21.29, -151.88) * mm, "end": v(15.52, -161.88) * mm});
            skLineSegment(sketch, "E16.33.2.14", {"start": v(15.52, -161.88) * mm, "end": v(3.97, -161.88) * mm});
            skLineSegment(sketch, "E16.0.3.2", {"start": v(23.79, 116.87) * mm, "end": v(35.34, 116.87) * mm});
            skLineSegment(sketch, "E16.3.3.2", {"start": v(18.02, 106.87) * mm, "end": v(23.79, 116.87) * mm});
            skLineSegment(sketch, "E16.6.3.2", {"start": v(23.79, 96.87) * mm, "end": v(18.02, 106.87) * mm});
            skLineSegment(sketch, "E16.9.3.2", {"start": v(35.34, 96.87) * mm, "end": v(23.79, 96.87) * mm});
            skLineSegment(sketch, "E16.12.3.2", {"start": v(41.11, 106.87) * mm, "end": v(35.34, 96.87) * mm});
            skLineSegment(sketch, "E16.15.3.2", {"start": v(35.34, 116.87) * mm, "end": v(41.11, 106.87) * mm});
            skLineSegment(sketch, "E16.18.3.2", {"start": v(37.5, 118.12) * mm, "end": v(43.28, 128.12) * mm});
            skLineSegment(sketch, "E16.21.3.2", {"start": v(43.28, 108.12) * mm, "end": v(37.5, 118.12) * mm});
            skLineSegment(sketch, "E16.24.3.2", {"start": v(43.28, 128.12) * mm, "end": v(54.82, 128.12) * mm});
            skLineSegment(sketch, "E16.27.3.2", {"start": v(54.82, 128.12) * mm, "end": v(60.6, 118.12) * mm});
            skLineSegment(sketch, "E16.30.3.2", {"start": v(60.6, 118.12) * mm, "end": v(54.82, 108.12) * mm});
            skLineSegment(sketch, "E16.33.3.2", {"start": v(54.82, 108.12) * mm, "end": v(43.28, 108.12) * mm});
            skLineSegment(sketch, "E16.0.3.3", {"start": v(23.79, 94.37) * mm, "end": v(35.34, 94.37) * mm});
            skLineSegment(sketch, "E16.3.3.3", {"start": v(18.02, 84.37) * mm, "end": v(23.79, 94.37) * mm});
            skLineSegment(sketch, "E16.6.3.3", {"start": v(23.79, 74.37) * mm, "end": v(18.02, 84.37) * mm});
            skLineSegment(sketch, "E16.9.3.3", {"start": v(35.34, 74.37) * mm, "end": v(23.79, 74.37) * mm});
            skLineSegment(sketch, "E16.12.3.3", {"start": v(41.11, 84.37) * mm, "end": v(35.34, 74.37) * mm});
            skLineSegment(sketch, "E16.15.3.3", {"start": v(35.34, 94.37) * mm, "end": v(41.11, 84.37) * mm});
            skLineSegment(sketch, "E16.18.3.3", {"start": v(37.5, 95.62) * mm, "end": v(43.28, 105.62) * mm});
            skLineSegment(sketch, "E16.21.3.3", {"start": v(43.28, 85.62) * mm, "end": v(37.5, 95.62) * mm});
            skLineSegment(sketch, "E16.24.3.3", {"start": v(43.28, 105.62) * mm, "end": v(54.82, 105.62) * mm});
            skLineSegment(sketch, "E16.27.3.3", {"start": v(54.82, 105.62) * mm, "end": v(60.6, 95.62) * mm});
            skLineSegment(sketch, "E16.30.3.3", {"start": v(60.6, 95.62) * mm, "end": v(54.82, 85.62) * mm});
            skLineSegment(sketch, "E16.33.3.3", {"start": v(54.82, 85.62) * mm, "end": v(43.28, 85.62) * mm});
            skLineSegment(sketch, "E16.0.3.4", {"start": v(23.79, 71.87) * mm, "end": v(35.34, 71.87) * mm});
            skLineSegment(sketch, "E16.3.3.4", {"start": v(18.02, 61.87) * mm, "end": v(23.79, 71.87) * mm});
            skLineSegment(sketch, "E16.6.3.4", {"start": v(23.79, 51.87) * mm, "end": v(18.02, 61.87) * mm});
            skLineSegment(sketch, "E16.9.3.4", {"start": v(35.34, 51.87) * mm, "end": v(23.79, 51.87) * mm});
            skLineSegment(sketch, "E16.12.3.4", {"start": v(41.11, 61.87) * mm, "end": v(35.34, 51.87) * mm});
            skLineSegment(sketch, "E16.15.3.4", {"start": v(35.34, 71.87) * mm, "end": v(41.11, 61.87) * mm});
            skLineSegment(sketch, "E16.18.3.4", {"start": v(37.5, 73.12) * mm, "end": v(43.28, 83.12) * mm});
            skLineSegment(sketch, "E16.21.3.4", {"start": v(43.28, 63.12) * mm, "end": v(37.5, 73.12) * mm});
            skLineSegment(sketch, "E16.24.3.4", {"start": v(43.28, 83.12) * mm, "end": v(54.82, 83.12) * mm});
            skLineSegment(sketch, "E16.27.3.4", {"start": v(54.82, 83.12) * mm, "end": v(60.6, 73.12) * mm});
            skLineSegment(sketch, "E16.30.3.4", {"start": v(60.6, 73.12) * mm, "end": v(54.82, 63.12) * mm});
            skLineSegment(sketch, "E16.33.3.4", {"start": v(54.82, 63.12) * mm, "end": v(43.28, 63.12) * mm});
            skLineSegment(sketch, "E16.0.3.5", {"start": v(23.79, 49.37) * mm, "end": v(35.34, 49.37) * mm});
            skLineSegment(sketch, "E16.3.3.5", {"start": v(18.02, 39.37) * mm, "end": v(23.79, 49.37) * mm});
            skLineSegment(sketch, "E16.6.3.5", {"start": v(23.79, 29.37) * mm, "end": v(18.02, 39.37) * mm});
            skLineSegment(sketch, "E16.9.3.5", {"start": v(35.34, 29.37) * mm, "end": v(23.79, 29.37) * mm});
            skLineSegment(sketch, "E16.12.3.5", {"start": v(41.11, 39.37) * mm, "end": v(35.34, 29.37) * mm});
            skLineSegment(sketch, "E16.15.3.5", {"start": v(35.34, 49.37) * mm, "end": v(41.11, 39.37) * mm});
            skLineSegment(sketch, "E16.18.3.5", {"start": v(37.5, 50.62) * mm, "end": v(43.28, 60.62) * mm});
            skLineSegment(sketch, "E16.21.3.5", {"start": v(43.28, 40.62) * mm, "end": v(37.5, 50.62) * mm});
            skLineSegment(sketch, "E16.24.3.5", {"start": v(43.28, 60.62) * mm, "end": v(54.82, 60.62) * mm});
            skLineSegment(sketch, "E16.27.3.5", {"start": v(54.82, 60.62) * mm, "end": v(60.6, 50.62) * mm});
            skLineSegment(sketch, "E16.30.3.5", {"start": v(60.6, 50.62) * mm, "end": v(54.82, 40.62) * mm});
            skLineSegment(sketch, "E16.33.3.5", {"start": v(54.82, 40.62) * mm, "end": v(43.28, 40.62) * mm});
            skLineSegment(sketch, "E16.0.3.6", {"start": v(23.79, 26.87) * mm, "end": v(35.34, 26.87) * mm});
            skLineSegment(sketch, "E16.3.3.6", {"start": v(18.02, 16.87) * mm, "end": v(23.79, 26.87) * mm});
            skLineSegment(sketch, "E16.6.3.6", {"start": v(23.79, 6.87) * mm, "end": v(18.02, 16.87) * mm});
            skLineSegment(sketch, "E16.9.3.6", {"start": v(35.34, 6.87) * mm, "end": v(23.79, 6.87) * mm});
            skLineSegment(sketch, "E16.12.3.6", {"start": v(41.11, 16.87) * mm, "end": v(35.34, 6.87) * mm});
            skLineSegment(sketch, "E16.15.3.6", {"start": v(35.34, 26.87) * mm, "end": v(41.11, 16.87) * mm});
            skLineSegment(sketch, "E16.18.3.6", {"start": v(37.5, 28.12) * mm, "end": v(43.28, 38.12) * mm});
            skLineSegment(sketch, "E16.21.3.6", {"start": v(43.28, 18.12) * mm, "end": v(37.5, 28.12) * mm});
            skLineSegment(sketch, "E16.24.3.6", {"start": v(43.28, 38.12) * mm, "end": v(54.82, 38.12) * mm});
            skLineSegment(sketch, "E16.27.3.6", {"start": v(54.82, 38.12) * mm, "end": v(60.6, 28.12) * mm});
            skLineSegment(sketch, "E16.30.3.6", {"start": v(60.6, 28.12) * mm, "end": v(54.82, 18.12) * mm});
            skLineSegment(sketch, "E16.33.3.6", {"start": v(54.82, 18.12) * mm, "end": v(43.28, 18.12) * mm});
            skLineSegment(sketch, "E16.0.3.7", {"start": v(23.79, 4.37) * mm, "end": v(35.34, 4.37) * mm});
            skLineSegment(sketch, "E16.3.3.7", {"start": v(18.02, -5.63) * mm, "end": v(23.79, 4.37) * mm});
            skLineSegment(sketch, "E16.6.3.7", {"start": v(23.79, -15.63) * mm, "end": v(18.02, -5.63) * mm});
            skLineSegment(sketch, "E16.9.3.7", {"start": v(35.34, -15.63) * mm, "end": v(23.79, -15.63) * mm});
            skLineSegment(sketch, "E16.12.3.7", {"start": v(41.11, -5.63) * mm, "end": v(35.34, -15.63) * mm});
            skLineSegment(sketch, "E16.15.3.7", {"start": v(35.34, 4.37) * mm, "end": v(41.11, -5.63) * mm});
            skLineSegment(sketch, "E16.18.3.7", {"start": v(37.5, 5.62) * mm, "end": v(43.28, 15.62) * mm});
            skLineSegment(sketch, "E16.21.3.7", {"start": v(43.28, -4.38) * mm, "end": v(37.5, 5.62) * mm});
            skLineSegment(sketch, "E16.24.3.7", {"start": v(43.28, 15.62) * mm, "end": v(54.82, 15.62) * mm});
            skLineSegment(sketch, "E16.27.3.7", {"start": v(54.82, 15.62) * mm, "end": v(60.6, 5.62) * mm});
            skLineSegment(sketch, "E16.30.3.7", {"start": v(60.6, 5.62) * mm, "end": v(54.82, -4.38) * mm});
            skLineSegment(sketch, "E16.33.3.7", {"start": v(54.82, -4.38) * mm, "end": v(43.28, -4.38) * mm});
            skLineSegment(sketch, "E16.0.3.8", {"start": v(23.79, -18.13) * mm, "end": v(35.34, -18.13) * mm});
            skLineSegment(sketch, "E16.3.3.8", {"start": v(18.02, -28.13) * mm, "end": v(23.79, -18.13) * mm});
            skLineSegment(sketch, "E16.6.3.8", {"start": v(23.79, -38.13) * mm, "end": v(18.02, -28.13) * mm});
            skLineSegment(sketch, "E16.9.3.8", {"start": v(35.34, -38.13) * mm, "end": v(23.79, -38.13) * mm});
            skLineSegment(sketch, "E16.12.3.8", {"start": v(41.11, -28.13) * mm, "end": v(35.34, -38.13) * mm});
            skLineSegment(sketch, "E16.15.3.8", {"start": v(35.34, -18.13) * mm, "end": v(41.11, -28.13) * mm});
            skLineSegment(sketch, "E16.18.3.8", {"start": v(37.5, -16.88) * mm, "end": v(43.28, -6.88) * mm});
            skLineSegment(sketch, "E16.21.3.8", {"start": v(43.28, -26.88) * mm, "end": v(37.5, -16.88) * mm});
            skLineSegment(sketch, "E16.24.3.8", {"start": v(43.28, -6.88) * mm, "end": v(54.82, -6.88) * mm});
            skLineSegment(sketch, "E16.27.3.8", {"start": v(54.82, -6.88) * mm, "end": v(60.6, -16.88) * mm});
            skLineSegment(sketch, "E16.30.3.8", {"start": v(60.6, -16.88) * mm, "end": v(54.82, -26.88) * mm});
            skLineSegment(sketch, "E16.33.3.8", {"start": v(54.82, -26.88) * mm, "end": v(43.28, -26.88) * mm});
            skLineSegment(sketch, "E16.0.3.9", {"start": v(23.79, -40.63) * mm, "end": v(35.34, -40.63) * mm});
            skLineSegment(sketch, "E16.3.3.9", {"start": v(18.02, -50.63) * mm, "end": v(23.79, -40.63) * mm});
            skLineSegment(sketch, "E16.6.3.9", {"start": v(23.79, -60.63) * mm, "end": v(18.02, -50.63) * mm});
            skLineSegment(sketch, "E16.9.3.9", {"start": v(35.34, -60.63) * mm, "end": v(23.79, -60.63) * mm});
            skLineSegment(sketch, "E16.12.3.9", {"start": v(41.11, -50.63) * mm, "end": v(35.34, -60.63) * mm});
            skLineSegment(sketch, "E16.15.3.9", {"start": v(35.34, -40.63) * mm, "end": v(41.11, -50.63) * mm});
            skLineSegment(sketch, "E16.18.3.9", {"start": v(37.5, -39.38) * mm, "end": v(43.28, -29.38) * mm});
            skLineSegment(sketch, "E16.21.3.9", {"start": v(43.28, -49.38) * mm, "end": v(37.5, -39.38) * mm});
            skLineSegment(sketch, "E16.24.3.9", {"start": v(43.28, -29.38) * mm, "end": v(54.82, -29.38) * mm});
            skLineSegment(sketch, "E16.27.3.9", {"start": v(54.82, -29.38) * mm, "end": v(60.6, -39.38) * mm});
            skLineSegment(sketch, "E16.30.3.9", {"start": v(60.6, -39.38) * mm, "end": v(54.82, -49.38) * mm});
            skLineSegment(sketch, "E16.33.3.9", {"start": v(54.82, -49.38) * mm, "end": v(43.28, -49.38) * mm});
            skLineSegment(sketch, "E16.0.3.10", {"start": v(23.79, -63.13) * mm, "end": v(35.34, -63.13) * mm});
            skLineSegment(sketch, "E16.3.3.10", {"start": v(18.02, -73.13) * mm, "end": v(23.79, -63.13) * mm});
            skLineSegment(sketch, "E16.6.3.10", {"start": v(23.79, -83.13) * mm, "end": v(18.02, -73.13) * mm});
            skLineSegment(sketch, "E16.9.3.10", {"start": v(35.34, -83.13) * mm, "end": v(23.79, -83.13) * mm});
            skLineSegment(sketch, "E16.12.3.10", {"start": v(41.11, -73.13) * mm, "end": v(35.34, -83.13) * mm});
            skLineSegment(sketch, "E16.15.3.10", {"start": v(35.34, -63.13) * mm, "end": v(41.11, -73.13) * mm});
            skLineSegment(sketch, "E16.18.3.10", {"start": v(37.5, -61.88) * mm, "end": v(43.28, -51.88) * mm});
            skLineSegment(sketch, "E16.21.3.10", {"start": v(43.28, -71.88) * mm, "end": v(37.5, -61.88) * mm});
            skLineSegment(sketch, "E16.24.3.10", {"start": v(43.28, -51.88) * mm, "end": v(54.82, -51.88) * mm});
            skLineSegment(sketch, "E16.27.3.10", {"start": v(54.82, -51.88) * mm, "end": v(60.6, -61.88) * mm});
            skLineSegment(sketch, "E16.30.3.10", {"start": v(60.6, -61.88) * mm, "end": v(54.82, -71.88) * mm});
            skLineSegment(sketch, "E16.33.3.10", {"start": v(54.82, -71.88) * mm, "end": v(43.28, -71.88) * mm});
            skLineSegment(sketch, "E16.0.3.11", {"start": v(23.79, -85.63) * mm, "end": v(35.34, -85.63) * mm});
            skLineSegment(sketch, "E16.3.3.11", {"start": v(18.02, -95.63) * mm, "end": v(23.79, -85.63) * mm});
            skLineSegment(sketch, "E16.6.3.11", {"start": v(23.79, -105.63) * mm, "end": v(18.02, -95.63) * mm});
            skLineSegment(sketch, "E16.9.3.11", {"start": v(35.34, -105.63) * mm, "end": v(23.79, -105.63) * mm});
            skLineSegment(sketch, "E16.12.3.11", {"start": v(41.11, -95.63) * mm, "end": v(35.34, -105.63) * mm});
            skLineSegment(sketch, "E16.15.3.11", {"start": v(35.34, -85.62) * mm, "end": v(41.11, -95.63) * mm});
            skLineSegment(sketch, "E16.18.3.11", {"start": v(37.5, -84.38) * mm, "end": v(43.28, -74.38) * mm});
            skLineSegment(sketch, "E16.21.3.11", {"start": v(43.28, -94.37) * mm, "end": v(37.5, -84.38) * mm});
            skLineSegment(sketch, "E16.24.3.11", {"start": v(43.28, -74.38) * mm, "end": v(54.82, -74.38) * mm});
            skLineSegment(sketch, "E16.27.3.11", {"start": v(54.82, -74.38) * mm, "end": v(60.6, -84.38) * mm});
            skLineSegment(sketch, "E16.30.3.11", {"start": v(60.6, -84.38) * mm, "end": v(54.82, -94.38) * mm});
            skLineSegment(sketch, "E16.33.3.11", {"start": v(54.82, -94.38) * mm, "end": v(43.28, -94.38) * mm});
            skLineSegment(sketch, "E16.0.3.12", {"start": v(23.79, -108.13) * mm, "end": v(35.34, -108.13) * mm});
            skLineSegment(sketch, "E16.3.3.12", {"start": v(18.02, -118.13) * mm, "end": v(23.79, -108.13) * mm});
            skLineSegment(sketch, "E16.6.3.12", {"start": v(23.79, -128.13) * mm, "end": v(18.02, -118.13) * mm});
            skLineSegment(sketch, "E16.9.3.12", {"start": v(35.34, -128.13) * mm, "end": v(23.79, -128.13) * mm});
            skLineSegment(sketch, "E16.12.3.12", {"start": v(41.11, -118.13) * mm, "end": v(35.34, -128.13) * mm});
            skLineSegment(sketch, "E16.15.3.12", {"start": v(35.34, -108.12) * mm, "end": v(41.11, -118.13) * mm});
            skLineSegment(sketch, "E16.18.3.12", {"start": v(37.5, -106.88) * mm, "end": v(43.28, -96.88) * mm});
            skLineSegment(sketch, "E16.21.3.12", {"start": v(43.28, -116.87) * mm, "end": v(37.5, -106.88) * mm});
            skLineSegment(sketch, "E16.24.3.12", {"start": v(43.28, -96.88) * mm, "end": v(54.82, -96.88) * mm});
            skLineSegment(sketch, "E16.27.3.12", {"start": v(54.82, -96.88) * mm, "end": v(60.6, -106.88) * mm});
            skLineSegment(sketch, "E16.30.3.12", {"start": v(60.6, -106.88) * mm, "end": v(54.82, -116.88) * mm});
            skLineSegment(sketch, "E16.33.3.12", {"start": v(54.82, -116.88) * mm, "end": v(43.28, -116.88) * mm});
            skLineSegment(sketch, "E16.0.3.13", {"start": v(23.79, -130.62) * mm, "end": v(35.34, -130.62) * mm});
            skLineSegment(sketch, "E16.3.3.13", {"start": v(18.02, -140.63) * mm, "end": v(23.79, -130.63) * mm});
            skLineSegment(sketch, "E16.6.3.13", {"start": v(23.79, -150.63) * mm, "end": v(18.02, -140.63) * mm});
            skLineSegment(sketch, "E16.9.3.13", {"start": v(35.34, -150.62) * mm, "end": v(23.79, -150.62) * mm});
            skLineSegment(sketch, "E16.12.3.13", {"start": v(41.11, -140.62) * mm, "end": v(35.34, -150.62) * mm});
            skLineSegment(sketch, "E16.15.3.13", {"start": v(35.34, -130.62) * mm, "end": v(41.11, -140.62) * mm});
            skLineSegment(sketch, "E16.18.3.13", {"start": v(37.5, -129.38) * mm, "end": v(43.28, -119.38) * mm});
            skLineSegment(sketch, "E16.21.3.13", {"start": v(43.28, -139.37) * mm, "end": v(37.5, -129.38) * mm});
            skLineSegment(sketch, "E16.24.3.13", {"start": v(43.28, -119.37) * mm, "end": v(54.82, -119.37) * mm});
            skLineSegment(sketch, "E16.27.3.13", {"start": v(54.82, -119.37) * mm, "end": v(60.6, -129.37) * mm});
            skLineSegment(sketch, "E16.30.3.13", {"start": v(60.6, -129.38) * mm, "end": v(54.82, -139.38) * mm});
            skLineSegment(sketch, "E16.33.3.13", {"start": v(54.82, -139.38) * mm, "end": v(43.28, -139.38) * mm});
            skLineSegment(sketch, "E16.0.3.14", {"start": v(23.79, -153.12) * mm, "end": v(35.34, -153.12) * mm});
            skLineSegment(sketch, "E16.3.3.14", {"start": v(18.02, -163.13) * mm, "end": v(23.79, -153.13) * mm});
            skLineSegment(sketch, "E16.6.3.14", {"start": v(23.79, -173.13) * mm, "end": v(18.02, -163.13) * mm});
            skLineSegment(sketch, "E16.9.3.14", {"start": v(35.34, -173.12) * mm, "end": v(23.79, -173.12) * mm});
            skLineSegment(sketch, "E16.12.3.14", {"start": v(41.11, -163.13) * mm, "end": v(35.34, -173.13) * mm});
            skLineSegment(sketch, "E16.15.3.14", {"start": v(35.34, -153.12) * mm, "end": v(41.11, -163.12) * mm});
            skLineSegment(sketch, "E16.18.3.14", {"start": v(37.5, -151.88) * mm, "end": v(43.28, -141.88) * mm});
            skLineSegment(sketch, "E16.21.3.14", {"start": v(43.28, -161.87) * mm, "end": v(37.5, -151.88) * mm});
            skLineSegment(sketch, "E16.24.3.14", {"start": v(43.28, -141.88) * mm, "end": v(54.82, -141.88) * mm});
            skLineSegment(sketch, "E16.27.3.14", {"start": v(54.82, -141.88) * mm, "end": v(60.6, -151.87) * mm});
            skLineSegment(sketch, "E16.30.3.14", {"start": v(60.6, -151.88) * mm, "end": v(54.82, -161.88) * mm});
            skLineSegment(sketch, "E16.33.3.14", {"start": v(54.82, -161.88) * mm, "end": v(43.28, -161.88) * mm});
            skLineSegment(sketch, "E16.0.4.2", {"start": v(63.1, 116.87) * mm, "end": v(74.64, 116.87) * mm});
            skLineSegment(sketch, "E16.3.4.2", {"start": v(57.32, 106.87) * mm, "end": v(63.1, 116.87) * mm});
            skLineSegment(sketch, "E16.6.4.2", {"start": v(63.1, 96.87) * mm, "end": v(57.32, 106.87) * mm});
            skLineSegment(sketch, "E16.9.4.2", {"start": v(74.64, 96.87) * mm, "end": v(63.1, 96.87) * mm});
            skLineSegment(sketch, "E16.12.4.2", {"start": v(80.42, 106.87) * mm, "end": v(74.64, 96.87) * mm});
            skLineSegment(sketch, "E16.15.4.2", {"start": v(74.64, 116.87) * mm, "end": v(80.42, 106.87) * mm});
            skLineSegment(sketch, "E16.18.4.2", {"start": v(76.8, 118.12) * mm, "end": v(82.58, 128.12) * mm});
            skLineSegment(sketch, "E16.21.4.2", {"start": v(82.58, 108.12) * mm, "end": v(76.8, 118.12) * mm});
            skLineSegment(sketch, "E16.24.4.2", {"start": v(82.58, 128.12) * mm, "end": v(94.13, 128.12) * mm});
            skLineSegment(sketch, "E16.27.4.2", {"start": v(94.13, 128.12) * mm, "end": v(99.9, 118.12) * mm});
            skLineSegment(sketch, "E16.30.4.2", {"start": v(99.9, 118.12) * mm, "end": v(94.13, 108.12) * mm});
            skLineSegment(sketch, "E16.33.4.2", {"start": v(94.13, 108.12) * mm, "end": v(82.58, 108.12) * mm});
            skLineSegment(sketch, "E16.0.4.3", {"start": v(63.1, 94.37) * mm, "end": v(74.64, 94.37) * mm});
            skLineSegment(sketch, "E16.3.4.3", {"start": v(57.32, 84.37) * mm, "end": v(63.1, 94.37) * mm});
            skLineSegment(sketch, "E16.6.4.3", {"start": v(63.1, 74.37) * mm, "end": v(57.32, 84.37) * mm});
            skLineSegment(sketch, "E16.9.4.3", {"start": v(74.64, 74.37) * mm, "end": v(63.1, 74.37) * mm});
            skLineSegment(sketch, "E16.12.4.3", {"start": v(80.42, 84.37) * mm, "end": v(74.64, 74.37) * mm});
            skLineSegment(sketch, "E16.15.4.3", {"start": v(74.64, 94.37) * mm, "end": v(80.42, 84.37) * mm});
            skLineSegment(sketch, "E16.18.4.3", {"start": v(76.8, 95.62) * mm, "end": v(82.58, 105.62) * mm});
            skLineSegment(sketch, "E16.21.4.3", {"start": v(82.58, 85.62) * mm, "end": v(76.8, 95.62) * mm});
            skLineSegment(sketch, "E16.24.4.3", {"start": v(82.58, 105.62) * mm, "end": v(94.13, 105.62) * mm});
            skLineSegment(sketch, "E16.27.4.3", {"start": v(94.13, 105.62) * mm, "end": v(99.9, 95.62) * mm});
            skLineSegment(sketch, "E16.30.4.3", {"start": v(99.9, 95.62) * mm, "end": v(94.13, 85.62) * mm});
            skLineSegment(sketch, "E16.33.4.3", {"start": v(94.13, 85.62) * mm, "end": v(82.58, 85.62) * mm});
            skLineSegment(sketch, "E16.0.4.4", {"start": v(63.1, 71.87) * mm, "end": v(74.64, 71.87) * mm});
            skLineSegment(sketch, "E16.3.4.4", {"start": v(57.32, 61.87) * mm, "end": v(63.1, 71.87) * mm});
            skLineSegment(sketch, "E16.6.4.4", {"start": v(63.1, 51.87) * mm, "end": v(57.32, 61.87) * mm});
            skLineSegment(sketch, "E16.9.4.4", {"start": v(74.64, 51.87) * mm, "end": v(63.1, 51.87) * mm});
            skLineSegment(sketch, "E16.12.4.4", {"start": v(80.42, 61.87) * mm, "end": v(74.64, 51.87) * mm});
            skLineSegment(sketch, "E16.15.4.4", {"start": v(74.64, 71.87) * mm, "end": v(80.42, 61.87) * mm});
            skLineSegment(sketch, "E16.18.4.4", {"start": v(76.8, 73.12) * mm, "end": v(82.58, 83.12) * mm});
            skLineSegment(sketch, "E16.21.4.4", {"start": v(82.58, 63.12) * mm, "end": v(76.8, 73.12) * mm});
            skLineSegment(sketch, "E16.24.4.4", {"start": v(82.58, 83.12) * mm, "end": v(94.13, 83.12) * mm});
            skLineSegment(sketch, "E16.27.4.4", {"start": v(94.13, 83.12) * mm, "end": v(99.9, 73.12) * mm});
            skLineSegment(sketch, "E16.30.4.4", {"start": v(99.9, 73.12) * mm, "end": v(94.13, 63.12) * mm});
            skLineSegment(sketch, "E16.33.4.4", {"start": v(94.13, 63.12) * mm, "end": v(82.58, 63.12) * mm});
            skLineSegment(sketch, "E16.0.4.5", {"start": v(63.1, 49.37) * mm, "end": v(74.64, 49.37) * mm});
            skLineSegment(sketch, "E16.3.4.5", {"start": v(57.32, 39.37) * mm, "end": v(63.1, 49.37) * mm});
            skLineSegment(sketch, "E16.6.4.5", {"start": v(63.1, 29.37) * mm, "end": v(57.32, 39.37) * mm});
            skLineSegment(sketch, "E16.9.4.5", {"start": v(74.64, 29.37) * mm, "end": v(63.1, 29.37) * mm});
            skLineSegment(sketch, "E16.12.4.5", {"start": v(80.42, 39.37) * mm, "end": v(74.64, 29.37) * mm});
            skLineSegment(sketch, "E16.15.4.5", {"start": v(74.64, 49.37) * mm, "end": v(80.42, 39.37) * mm});
            skLineSegment(sketch, "E16.18.4.5", {"start": v(76.8, 50.62) * mm, "end": v(82.58, 60.62) * mm});
            skLineSegment(sketch, "E16.21.4.5", {"start": v(82.58, 40.62) * mm, "end": v(76.8, 50.62) * mm});
            skLineSegment(sketch, "E16.24.4.5", {"start": v(82.58, 60.62) * mm, "end": v(94.13, 60.62) * mm});
            skLineSegment(sketch, "E16.27.4.5", {"start": v(94.13, 60.62) * mm, "end": v(99.9, 50.62) * mm});
            skLineSegment(sketch, "E16.30.4.5", {"start": v(99.9, 50.62) * mm, "end": v(94.13, 40.62) * mm});
            skLineSegment(sketch, "E16.33.4.5", {"start": v(94.13, 40.62) * mm, "end": v(82.58, 40.62) * mm});
            skLineSegment(sketch, "E16.0.4.6", {"start": v(63.1, 26.87) * mm, "end": v(74.64, 26.87) * mm});
            skLineSegment(sketch, "E16.3.4.6", {"start": v(57.32, 16.87) * mm, "end": v(63.1, 26.87) * mm});
            skLineSegment(sketch, "E16.6.4.6", {"start": v(63.1, 6.87) * mm, "end": v(57.32, 16.87) * mm});
            skLineSegment(sketch, "E16.9.4.6", {"start": v(74.64, 6.87) * mm, "end": v(63.1, 6.87) * mm});
            skLineSegment(sketch, "E16.12.4.6", {"start": v(80.42, 16.87) * mm, "end": v(74.64, 6.87) * mm});
            skLineSegment(sketch, "E16.15.4.6", {"start": v(74.64, 26.87) * mm, "end": v(80.42, 16.87) * mm});
            skLineSegment(sketch, "E16.18.4.6", {"start": v(76.8, 28.12) * mm, "end": v(82.58, 38.12) * mm});
            skLineSegment(sketch, "E16.21.4.6", {"start": v(82.58, 18.12) * mm, "end": v(76.8, 28.12) * mm});
            skLineSegment(sketch, "E16.24.4.6", {"start": v(82.58, 38.12) * mm, "end": v(94.13, 38.12) * mm});
            skLineSegment(sketch, "E16.27.4.6", {"start": v(94.13, 38.12) * mm, "end": v(99.9, 28.12) * mm});
            skLineSegment(sketch, "E16.30.4.6", {"start": v(99.9, 28.12) * mm, "end": v(94.13, 18.12) * mm});
            skLineSegment(sketch, "E16.33.4.6", {"start": v(94.13, 18.12) * mm, "end": v(82.58, 18.12) * mm});
            skLineSegment(sketch, "E16.0.4.7", {"start": v(63.1, 4.37) * mm, "end": v(74.64, 4.37) * mm});
            skLineSegment(sketch, "E16.3.4.7", {"start": v(57.32, -5.63) * mm, "end": v(63.1, 4.37) * mm});
            skLineSegment(sketch, "E16.6.4.7", {"start": v(63.1, -15.63) * mm, "end": v(57.32, -5.63) * mm});
            skLineSegment(sketch, "E16.9.4.7", {"start": v(74.64, -15.63) * mm, "end": v(63.1, -15.63) * mm});
            skLineSegment(sketch, "E16.12.4.7", {"start": v(80.42, -5.63) * mm, "end": v(74.64, -15.63) * mm});
            skLineSegment(sketch, "E16.15.4.7", {"start": v(74.64, 4.37) * mm, "end": v(80.42, -5.63) * mm});
            skLineSegment(sketch, "E16.18.4.7", {"start": v(76.8, 5.62) * mm, "end": v(82.58, 15.62) * mm});
            skLineSegment(sketch, "E16.21.4.7", {"start": v(82.58, -4.38) * mm, "end": v(76.8, 5.62) * mm});
            skLineSegment(sketch, "E16.24.4.7", {"start": v(82.58, 15.62) * mm, "end": v(94.13, 15.62) * mm});
            skLineSegment(sketch, "E16.27.4.7", {"start": v(94.13, 15.62) * mm, "end": v(99.9, 5.62) * mm});
            skLineSegment(sketch, "E16.30.4.7", {"start": v(99.9, 5.62) * mm, "end": v(94.13, -4.38) * mm});
            skLineSegment(sketch, "E16.33.4.7", {"start": v(94.13, -4.38) * mm, "end": v(82.58, -4.38) * mm});
            skLineSegment(sketch, "E16.0.4.8", {"start": v(63.1, -18.13) * mm, "end": v(74.64, -18.13) * mm});
            skLineSegment(sketch, "E16.3.4.8", {"start": v(57.32, -28.13) * mm, "end": v(63.1, -18.13) * mm});
            skLineSegment(sketch, "E16.6.4.8", {"start": v(63.1, -38.13) * mm, "end": v(57.32, -28.13) * mm});
            skLineSegment(sketch, "E16.9.4.8", {"start": v(74.64, -38.13) * mm, "end": v(63.1, -38.13) * mm});
            skLineSegment(sketch, "E16.12.4.8", {"start": v(80.42, -28.13) * mm, "end": v(74.64, -38.13) * mm});
            skLineSegment(sketch, "E16.15.4.8", {"start": v(74.64, -18.13) * mm, "end": v(80.42, -28.13) * mm});
            skLineSegment(sketch, "E16.18.4.8", {"start": v(76.8, -16.88) * mm, "end": v(82.58, -6.88) * mm});
            skLineSegment(sketch, "E16.21.4.8", {"start": v(82.58, -26.88) * mm, "end": v(76.8, -16.88) * mm});
            skLineSegment(sketch, "E16.24.4.8", {"start": v(82.58, -6.88) * mm, "end": v(94.13, -6.88) * mm});
            skLineSegment(sketch, "E16.27.4.8", {"start": v(94.13, -6.88) * mm, "end": v(99.9, -16.88) * mm});
            skLineSegment(sketch, "E16.30.4.8", {"start": v(99.9, -16.88) * mm, "end": v(94.13, -26.88) * mm});
            skLineSegment(sketch, "E16.33.4.8", {"start": v(94.13, -26.88) * mm, "end": v(82.58, -26.88) * mm});
            skLineSegment(sketch, "E16.0.4.9", {"start": v(63.1, -40.63) * mm, "end": v(74.64, -40.63) * mm});
            skLineSegment(sketch, "E16.3.4.9", {"start": v(57.32, -50.63) * mm, "end": v(63.1, -40.63) * mm});
            skLineSegment(sketch, "E16.6.4.9", {"start": v(63.1, -60.63) * mm, "end": v(57.32, -50.63) * mm});
            skLineSegment(sketch, "E16.9.4.9", {"start": v(74.64, -60.63) * mm, "end": v(63.1, -60.63) * mm});
            skLineSegment(sketch, "E16.12.4.9", {"start": v(80.42, -50.63) * mm, "end": v(74.64, -60.63) * mm});
            skLineSegment(sketch, "E16.15.4.9", {"start": v(74.64, -40.63) * mm, "end": v(80.42, -50.63) * mm});
            skLineSegment(sketch, "E16.18.4.9", {"start": v(76.8, -39.38) * mm, "end": v(82.58, -29.38) * mm});
            skLineSegment(sketch, "E16.21.4.9", {"start": v(82.58, -49.38) * mm, "end": v(76.8, -39.38) * mm});
            skLineSegment(sketch, "E16.24.4.9", {"start": v(82.58, -29.38) * mm, "end": v(94.13, -29.38) * mm});
            skLineSegment(sketch, "E16.27.4.9", {"start": v(94.13, -29.38) * mm, "end": v(99.9, -39.38) * mm});
            skLineSegment(sketch, "E16.30.4.9", {"start": v(99.9, -39.38) * mm, "end": v(94.13, -49.38) * mm});
            skLineSegment(sketch, "E16.33.4.9", {"start": v(94.13, -49.38) * mm, "end": v(82.58, -49.38) * mm});
            skLineSegment(sketch, "E16.0.4.10", {"start": v(63.1, -63.13) * mm, "end": v(74.64, -63.13) * mm});
            skLineSegment(sketch, "E16.3.4.10", {"start": v(57.32, -73.13) * mm, "end": v(63.1, -63.13) * mm});
            skLineSegment(sketch, "E16.6.4.10", {"start": v(63.1, -83.13) * mm, "end": v(57.32, -73.13) * mm});
            skLineSegment(sketch, "E16.9.4.10", {"start": v(74.64, -83.13) * mm, "end": v(63.1, -83.13) * mm});
            skLineSegment(sketch, "E16.12.4.10", {"start": v(80.42, -73.13) * mm, "end": v(74.64, -83.13) * mm});
            skLineSegment(sketch, "E16.15.4.10", {"start": v(74.64, -63.13) * mm, "end": v(80.42, -73.13) * mm});
            skLineSegment(sketch, "E16.18.4.10", {"start": v(76.8, -61.88) * mm, "end": v(82.58, -51.88) * mm});
            skLineSegment(sketch, "E16.21.4.10", {"start": v(82.58, -71.88) * mm, "end": v(76.8, -61.88) * mm});
            skLineSegment(sketch, "E16.24.4.10", {"start": v(82.58, -51.88) * mm, "end": v(94.13, -51.88) * mm});
            skLineSegment(sketch, "E16.27.4.10", {"start": v(94.13, -51.88) * mm, "end": v(99.9, -61.88) * mm});
            skLineSegment(sketch, "E16.30.4.10", {"start": v(99.9, -61.88) * mm, "end": v(94.13, -71.88) * mm});
            skLineSegment(sketch, "E16.33.4.10", {"start": v(94.13, -71.88) * mm, "end": v(82.58, -71.88) * mm});
            skLineSegment(sketch, "E16.0.4.11", {"start": v(63.1, -85.63) * mm, "end": v(74.64, -85.63) * mm});
            skLineSegment(sketch, "E16.3.4.11", {"start": v(57.32, -95.63) * mm, "end": v(63.1, -85.63) * mm});
            skLineSegment(sketch, "E16.6.4.11", {"start": v(63.1, -105.63) * mm, "end": v(57.32, -95.63) * mm});
            skLineSegment(sketch, "E16.9.4.11", {"start": v(74.64, -105.63) * mm, "end": v(63.1, -105.63) * mm});
            skLineSegment(sketch, "E16.12.4.11", {"start": v(80.42, -95.63) * mm, "end": v(74.64, -105.63) * mm});
            skLineSegment(sketch, "E16.15.4.11", {"start": v(74.64, -85.62) * mm, "end": v(80.42, -95.63) * mm});
            skLineSegment(sketch, "E16.18.4.11", {"start": v(76.8, -84.38) * mm, "end": v(82.58, -74.38) * mm});
            skLineSegment(sketch, "E16.21.4.11", {"start": v(82.58, -94.37) * mm, "end": v(76.8, -84.38) * mm});
            skLineSegment(sketch, "E16.24.4.11", {"start": v(82.58, -74.38) * mm, "end": v(94.13, -74.38) * mm});
            skLineSegment(sketch, "E16.27.4.11", {"start": v(94.13, -74.38) * mm, "end": v(99.9, -84.38) * mm});
            skLineSegment(sketch, "E16.30.4.11", {"start": v(99.9, -84.38) * mm, "end": v(94.13, -94.38) * mm});
            skLineSegment(sketch, "E16.33.4.11", {"start": v(94.13, -94.38) * mm, "end": v(82.58, -94.38) * mm});
            skLineSegment(sketch, "E16.0.4.12", {"start": v(63.1, -108.13) * mm, "end": v(74.64, -108.13) * mm});
            skLineSegment(sketch, "E16.3.4.12", {"start": v(57.32, -118.13) * mm, "end": v(63.1, -108.13) * mm});
            skLineSegment(sketch, "E16.6.4.12", {"start": v(63.1, -128.13) * mm, "end": v(57.32, -118.13) * mm});
            skLineSegment(sketch, "E16.9.4.12", {"start": v(74.64, -128.13) * mm, "end": v(63.1, -128.13) * mm});
            skLineSegment(sketch, "E16.12.4.12", {"start": v(80.42, -118.13) * mm, "end": v(74.64, -128.13) * mm});
            skLineSegment(sketch, "E16.15.4.12", {"start": v(74.64, -108.12) * mm, "end": v(80.42, -118.13) * mm});
            skLineSegment(sketch, "E16.18.4.12", {"start": v(76.8, -106.88) * mm, "end": v(82.58, -96.88) * mm});
            skLineSegment(sketch, "E16.21.4.12", {"start": v(82.58, -116.87) * mm, "end": v(76.8, -106.88) * mm});
            skLineSegment(sketch, "E16.24.4.12", {"start": v(82.58, -96.88) * mm, "end": v(94.13, -96.88) * mm});
            skLineSegment(sketch, "E16.27.4.12", {"start": v(94.13, -96.88) * mm, "end": v(99.9, -106.88) * mm});
            skLineSegment(sketch, "E16.30.4.12", {"start": v(99.9, -106.88) * mm, "end": v(94.13, -116.88) * mm});
            skLineSegment(sketch, "E16.33.4.12", {"start": v(94.13, -116.88) * mm, "end": v(82.58, -116.88) * mm});
            skLineSegment(sketch, "E16.0.4.13", {"start": v(63.1, -130.62) * mm, "end": v(74.64, -130.62) * mm});
            skLineSegment(sketch, "E16.3.4.13", {"start": v(57.32, -140.63) * mm, "end": v(63.1, -130.63) * mm});
            skLineSegment(sketch, "E16.6.4.13", {"start": v(63.1, -150.63) * mm, "end": v(57.32, -140.63) * mm});
            skLineSegment(sketch, "E16.9.4.13", {"start": v(74.64, -150.62) * mm, "end": v(63.1, -150.62) * mm});
            skLineSegment(sketch, "E16.12.4.13", {"start": v(80.42, -140.62) * mm, "end": v(74.64, -150.62) * mm});
            skLineSegment(sketch, "E16.15.4.13", {"start": v(74.64, -130.62) * mm, "end": v(80.42, -140.62) * mm});
            skLineSegment(sketch, "E16.18.4.13", {"start": v(76.8, -129.38) * mm, "end": v(82.58, -119.38) * mm});
            skLineSegment(sketch, "E16.21.4.13", {"start": v(82.58, -139.37) * mm, "end": v(76.8, -129.38) * mm});
            skLineSegment(sketch, "E16.24.4.13", {"start": v(82.58, -119.37) * mm, "end": v(94.13, -119.37) * mm});
            skLineSegment(sketch, "E16.27.4.13", {"start": v(94.13, -119.38) * mm, "end": v(99.9, -129.37) * mm});
            skLineSegment(sketch, "E16.30.4.13", {"start": v(99.9, -129.38) * mm, "end": v(94.13, -139.38) * mm});
            skLineSegment(sketch, "E16.33.4.13", {"start": v(94.13, -139.38) * mm, "end": v(82.58, -139.38) * mm});
            skLineSegment(sketch, "E16.0.4.14", {"start": v(63.1, -153.12) * mm, "end": v(74.64, -153.12) * mm});
            skLineSegment(sketch, "E16.3.4.14", {"start": v(57.32, -163.13) * mm, "end": v(63.1, -153.13) * mm});
            skLineSegment(sketch, "E16.6.4.14", {"start": v(63.1, -173.13) * mm, "end": v(57.32, -163.13) * mm});
            skLineSegment(sketch, "E16.9.4.14", {"start": v(74.64, -173.13) * mm, "end": v(63.1, -173.13) * mm});
            skLineSegment(sketch, "E16.12.4.14", {"start": v(80.42, -163.13) * mm, "end": v(74.64, -173.13) * mm});
            skLineSegment(sketch, "E16.15.4.14", {"start": v(74.64, -153.12) * mm, "end": v(80.42, -163.12) * mm});
            skLineSegment(sketch, "E16.18.4.14", {"start": v(76.8, -151.88) * mm, "end": v(82.58, -141.88) * mm});
            skLineSegment(sketch, "E16.21.4.14", {"start": v(82.58, -161.87) * mm, "end": v(76.8, -151.88) * mm});
            skLineSegment(sketch, "E16.24.4.14", {"start": v(82.58, -141.88) * mm, "end": v(94.13, -141.88) * mm});
            skLineSegment(sketch, "E16.27.4.14", {"start": v(94.13, -141.88) * mm, "end": v(99.9, -151.87) * mm});
            skLineSegment(sketch, "E16.30.4.14", {"start": v(99.9, -151.88) * mm, "end": v(94.13, -161.88) * mm});
            skLineSegment(sketch, "E16.33.4.14", {"start": v(94.13, -161.88) * mm, "end": v(82.58, -161.88) * mm});
            skPoint(sketch, "E17.0", {"position": v(90, -147.52) * mm});
            skLineSegment(sketch, "E18", {"start": v(90, -147.52) * mm, "end": v(-50.12, -147.52) * mm});
            skLineSegment(sketch, "E19.0", {"start": v(-87.5, -118.77) * mm, "end": v(-50.12, -147.52) * mm});
            skPoint(sketch, "E20.0", {"position": v(90, 147.52) * mm});
            skLineSegment(sketch, "E21", {"start": v(90, 147.52) * mm, "end": v(-50.12, 147.52) * mm});
            skLineSegment(sketch, "E22.0", {"start": v(-50.12, 147.52) * mm, "end": v(-87.5, 118.77) * mm});
            skLineSegment(sketch, "E23.0", {"start": v(87.5, -149.7) * mm, "end": v(87.5, 149.7) * mm});
            skLineSegment(sketch, "E24.0", {"start": v(-87.5, -118.77) * mm, "end": v(-87.5, 118.77) * mm});
            skSolve(sketch);
        }
        {
            var Q0;
            {var subQ1=sQuery(id+"F4.wireOp",EDGE,"E14.1.0.3");Q0=makeQuery(id+"F4.imprint","IMPRINT",FACE,{"disambiguationData":[TD([[makeQuery(id+"F4.imprint","IMPRINT",EDGE,{"derivedFrom":subQ1}),-1.0]])]});}
            var Q1;
            {var subQ4=sQuery(id+"F4.wireOp",EDGE,"E14.1.1.7");Q1=makeQuery(id+"F4.imprint","IMPRINT",FACE,{"disambiguationData":[TD([[makeQuery(id+"F4.imprint","IMPRINT",EDGE,{"derivedFrom":subQ4}),-1.0]])]});}
            var Q2;
            {var subQ0=sQuery(id+"F4.wireOp",EDGE,"E14.2.0.3");Q2=makeQuery(id+"F4.imprint","IMPRINT",FACE,{"disambiguationData":[TD([[makeQuery(id+"F4.imprint","IMPRINT",EDGE,{"derivedFrom":subQ0}),-1.0]])]});}
            var Q3;
            {var subQ4=sQuery(id+"F4.wireOp",EDGE,"E14.2.1.7");Q3=makeQuery(id+"F4.imprint","IMPRINT",FACE,{"disambiguationData":[TD([[makeQuery(id+"F4.imprint","IMPRINT",EDGE,{"derivedFrom":subQ4}),-1.0]])]});}
            var Q4;
            {var subQ0=sQuery(id+"F4.wireOp",EDGE,"E15.9.3.0");Q4=makeQuery(id+"F4.imprint","IMPRINT",FACE,{"disambiguationData":[TD([[makeQuery(id+"F4.imprint","IMPRINT",EDGE,{"derivedFrom":subQ0}),-1.0]])]});}
            var Q5;
            {var subQ6=sQuery(id+"F4.wireOp",EDGE,"E15.21.3.1");Q5=makeQuery(id+"F4.imprint","IMPRINT",FACE,{"disambiguationData":[TD([[makeQuery(id+"F4.imprint","IMPRINT",EDGE,{"derivedFrom":subQ6}),-1.0]])]});}
            var Q6;
            {var subQ0=sQuery(id+"F4.wireOp",EDGE,"E14.0.1.4");var subQ1=sQuery(id+"F4.wireOp",EDGE,"E14.0.1.3");var subQ2=makeQuery(id+"F4.imprint","INTERSECT",VERTEX,{"derivedFrom":[subQ1,subQ0]});Q6=makeQuery(id+"F4.imprint","IMPRINT",FACE,{"disambiguationData":[TD([[makeQuery(id+"F4.imprint","IMPRINT",EDGE,{"disambiguationData":[TD([[subQ2,-1.0]])],"derivedFrom":subQ1}),-1.0]])]});}
            var Q7;
            Q7=makeQuery(id+"F4.imprint","IMPRINT",FACE,{"disambiguationData":[TD([[makeQuery(id+"F4.imprint","IMPRINT",EDGE,{"derivedFrom":sQuery(id+"F4.wireOp",EDGE,"E14.1.1.0")}),-1.0]])]});
            var Q8;
            Q8=makeQuery(id+"F4.imprint","IMPRINT",FACE,{"disambiguationData":[TD([[makeQuery(id+"F4.imprint","IMPRINT",EDGE,{"derivedFrom":sQuery(id+"F4.wireOp",EDGE,"E14.2.1.0")}),-1.0]])]});
            var Q9;
            Q9=makeQuery(id+"F4.imprint","IMPRINT",FACE,{"disambiguationData":[TD([[makeQuery(id+"F4.imprint","IMPRINT",EDGE,{"derivedFrom":sQuery(id+"F4.wireOp",EDGE,"E15.0.3.1")}),-1.0]])]});
            var Q10;
            Q10=makeQuery(id+"F4.imprint","IMPRINT",FACE,{"disambiguationData":[TD([[makeQuery(id+"F4.imprint","IMPRINT",EDGE,{"derivedFrom":sQuery(id+"F4.wireOp",EDGE,"E16.18.0.2")}),-1.0]])]});
            var Q11;
            Q11=makeQuery(id+"F4.imprint","IMPRINT",FACE,{"disambiguationData":[TD([[makeQuery(id+"F4.imprint","IMPRINT",EDGE,{"derivedFrom":sQuery(id+"F4.wireOp",EDGE,"E16.18.1.2")}),-1.0]])]});
            var Q12;
            Q12=makeQuery(id+"F4.imprint","IMPRINT",FACE,{"disambiguationData":[TD([[makeQuery(id+"F4.imprint","IMPRINT",EDGE,{"derivedFrom":sQuery(id+"F4.wireOp",EDGE,"E16.18.2.2")}),-1.0]])]});
            var Q13;
            Q13=makeQuery(id+"F4.imprint","IMPRINT",FACE,{"disambiguationData":[TD([[makeQuery(id+"F4.imprint","IMPRINT",EDGE,{"derivedFrom":sQuery(id+"F4.wireOp",EDGE,"E16.18.3.2")}),-1.0]])]});
            var Q14;
            {var subQ1=sQuery(id+"F4.wireOp",EDGE,"E16.12.0.2");Q14=makeQuery(id+"F4.imprint","IMPRINT",FACE,{"disambiguationData":[TD([[makeQuery(id+"F4.imprint","IMPRINT",EDGE,{"derivedFrom":subQ1}),-1.0]])]});}
            var Q15;
            Q15=makeQuery(id+"F4.imprint","IMPRINT",FACE,{"disambiguationData":[TD([[makeQuery(id+"F4.imprint","IMPRINT",EDGE,{"derivedFrom":sQuery(id+"F4.wireOp",EDGE,"E16.0.1.2")}),-1.0]])]});
            var Q16;
            Q16=makeQuery(id+"F4.imprint","IMPRINT",FACE,{"disambiguationData":[TD([[makeQuery(id+"F4.imprint","IMPRINT",EDGE,{"derivedFrom":sQuery(id+"F4.wireOp",EDGE,"E16.0.2.2")}),-1.0]])]});
            var Q17;
            Q17=makeQuery(id+"F4.imprint","IMPRINT",FACE,{"disambiguationData":[TD([[makeQuery(id+"F4.imprint","IMPRINT",EDGE,{"derivedFrom":sQuery(id+"F4.wireOp",EDGE,"E16.0.3.2")}),-1.0]])]});
            var Q18;
            Q18=makeQuery(id+"F4.imprint","IMPRINT",FACE,{"disambiguationData":[TD([[makeQuery(id+"F4.imprint","IMPRINT",EDGE,{"derivedFrom":sQuery(id+"F4.wireOp",EDGE,"E16.0.4.2")}),-1.0]])]});
            var Q19;
            Q19=makeQuery(id+"F4.imprint","IMPRINT",FACE,{"disambiguationData":[TD([[makeQuery(id+"F4.imprint","IMPRINT",EDGE,{"derivedFrom":sQuery(id+"F4.wireOp",EDGE,"E16.18.0.3")}),-1.0]])]});
            var Q20;
            Q20=makeQuery(id+"F4.imprint","IMPRINT",FACE,{"disambiguationData":[TD([[makeQuery(id+"F4.imprint","IMPRINT",EDGE,{"derivedFrom":sQuery(id+"F4.wireOp",EDGE,"E16.18.1.3")}),-1.0]])]});
            var Q21;
            Q21=makeQuery(id+"F4.imprint","IMPRINT",FACE,{"disambiguationData":[TD([[makeQuery(id+"F4.imprint","IMPRINT",EDGE,{"derivedFrom":sQuery(id+"F4.wireOp",EDGE,"E16.18.2.3")}),-1.0]])]});
            var Q22;
            Q22=makeQuery(id+"F4.imprint","IMPRINT",FACE,{"disambiguationData":[TD([[makeQuery(id+"F4.imprint","IMPRINT",EDGE,{"derivedFrom":sQuery(id+"F4.wireOp",EDGE,"E16.18.3.3")}),-1.0]])]});
            var Q23;
            {var subQ5=sQuery(id+"F4.wireOp",EDGE,"E16.18.4.3");Q23=makeQuery(id+"F4.imprint","IMPRINT",FACE,{"disambiguationData":[TD([[makeQuery(id+"F4.imprint","IMPRINT",EDGE,{"derivedFrom":subQ5}),-1.0]])]});}
            var Q24;
            {var subQ1=sQuery(id+"F4.wireOp",EDGE,"E16.12.0.3");Q24=makeQuery(id+"F4.imprint","IMPRINT",FACE,{"disambiguationData":[TD([[makeQuery(id+"F4.imprint","IMPRINT",EDGE,{"derivedFrom":subQ1}),-1.0]])]});}
            var Q25;
            Q25=makeQuery(id+"F4.imprint","IMPRINT",FACE,{"disambiguationData":[TD([[makeQuery(id+"F4.imprint","IMPRINT",EDGE,{"derivedFrom":sQuery(id+"F4.wireOp",EDGE,"E16.0.1.3")}),-1.0]])]});
            var Q26;
            Q26=makeQuery(id+"F4.imprint","IMPRINT",FACE,{"disambiguationData":[TD([[makeQuery(id+"F4.imprint","IMPRINT",EDGE,{"derivedFrom":sQuery(id+"F4.wireOp",EDGE,"E16.0.2.3")}),-1.0]])]});
            var Q27;
            Q27=makeQuery(id+"F4.imprint","IMPRINT",FACE,{"disambiguationData":[TD([[makeQuery(id+"F4.imprint","IMPRINT",EDGE,{"derivedFrom":sQuery(id+"F4.wireOp",EDGE,"E16.0.3.3")}),-1.0]])]});
            var Q28;
            Q28=makeQuery(id+"F4.imprint","IMPRINT",FACE,{"disambiguationData":[TD([[makeQuery(id+"F4.imprint","IMPRINT",EDGE,{"derivedFrom":sQuery(id+"F4.wireOp",EDGE,"E16.0.4.3")}),-1.0]])]});
            var Q29;
            Q29=makeQuery(id+"F4.imprint","IMPRINT",FACE,{"disambiguationData":[TD([[makeQuery(id+"F4.imprint","IMPRINT",EDGE,{"derivedFrom":sQuery(id+"F4.wireOp",EDGE,"E16.18.0.4")}),-1.0]])]});
            var Q30;
            Q30=makeQuery(id+"F4.imprint","IMPRINT",FACE,{"disambiguationData":[TD([[makeQuery(id+"F4.imprint","IMPRINT",EDGE,{"derivedFrom":sQuery(id+"F4.wireOp",EDGE,"E16.18.1.4")}),-1.0]])]});
            var Q31;
            Q31=makeQuery(id+"F4.imprint","IMPRINT",FACE,{"disambiguationData":[TD([[makeQuery(id+"F4.imprint","IMPRINT",EDGE,{"derivedFrom":sQuery(id+"F4.wireOp",EDGE,"E16.18.2.4")}),-1.0]])]});
            var Q32;
            Q32=makeQuery(id+"F4.imprint","IMPRINT",FACE,{"disambiguationData":[TD([[makeQuery(id+"F4.imprint","IMPRINT",EDGE,{"derivedFrom":sQuery(id+"F4.wireOp",EDGE,"E16.18.3.4")}),-1.0]])]});
            var Q33;
            {var subQ5=sQuery(id+"F4.wireOp",EDGE,"E16.18.4.4");Q33=makeQuery(id+"F4.imprint","IMPRINT",FACE,{"disambiguationData":[TD([[makeQuery(id+"F4.imprint","IMPRINT",EDGE,{"derivedFrom":subQ5}),-1.0]])]});}
            var Q34;
            {var subQ1=sQuery(id+"F4.wireOp",EDGE,"E16.12.0.4");Q34=makeQuery(id+"F4.imprint","IMPRINT",FACE,{"disambiguationData":[TD([[makeQuery(id+"F4.imprint","IMPRINT",EDGE,{"derivedFrom":subQ1}),-1.0]])]});}
            var Q35;
            Q35=makeQuery(id+"F4.imprint","IMPRINT",FACE,{"disambiguationData":[TD([[makeQuery(id+"F4.imprint","IMPRINT",EDGE,{"derivedFrom":sQuery(id+"F4.wireOp",EDGE,"E16.0.1.4")}),-1.0]])]});
            var Q36;
            Q36=makeQuery(id+"F4.imprint","IMPRINT",FACE,{"disambiguationData":[TD([[makeQuery(id+"F4.imprint","IMPRINT",EDGE,{"derivedFrom":sQuery(id+"F4.wireOp",EDGE,"E16.0.2.4")}),-1.0]])]});
            var Q37;
            Q37=makeQuery(id+"F4.imprint","IMPRINT",FACE,{"disambiguationData":[TD([[makeQuery(id+"F4.imprint","IMPRINT",EDGE,{"derivedFrom":sQuery(id+"F4.wireOp",EDGE,"E16.0.3.4")}),-1.0]])]});
            var Q38;
            Q38=makeQuery(id+"F4.imprint","IMPRINT",FACE,{"disambiguationData":[TD([[makeQuery(id+"F4.imprint","IMPRINT",EDGE,{"derivedFrom":sQuery(id+"F4.wireOp",EDGE,"E16.0.4.4")}),-1.0]])]});
            var Q39;
            Q39=makeQuery(id+"F4.imprint","IMPRINT",FACE,{"disambiguationData":[TD([[makeQuery(id+"F4.imprint","IMPRINT",EDGE,{"derivedFrom":sQuery(id+"F4.wireOp",EDGE,"E16.18.0.5")}),-1.0]])]});
            var Q40;
            Q40=makeQuery(id+"F4.imprint","IMPRINT",FACE,{"disambiguationData":[TD([[makeQuery(id+"F4.imprint","IMPRINT",EDGE,{"derivedFrom":sQuery(id+"F4.wireOp",EDGE,"E16.18.1.5")}),-1.0]])]});
            var Q41;
            Q41=makeQuery(id+"F4.imprint","IMPRINT",FACE,{"disambiguationData":[TD([[makeQuery(id+"F4.imprint","IMPRINT",EDGE,{"derivedFrom":sQuery(id+"F4.wireOp",EDGE,"E16.18.2.5")}),-1.0]])]});
            var Q42;
            Q42=makeQuery(id+"F4.imprint","IMPRINT",FACE,{"disambiguationData":[TD([[makeQuery(id+"F4.imprint","IMPRINT",EDGE,{"derivedFrom":sQuery(id+"F4.wireOp",EDGE,"E16.18.3.5")}),-1.0]])]});
            var Q43;
            {var subQ5=sQuery(id+"F4.wireOp",EDGE,"E16.18.4.5");Q43=makeQuery(id+"F4.imprint","IMPRINT",FACE,{"disambiguationData":[TD([[makeQuery(id+"F4.imprint","IMPRINT",EDGE,{"derivedFrom":subQ5}),-1.0]])]});}
            var Q44;
            {var subQ1=sQuery(id+"F4.wireOp",EDGE,"E16.12.0.5");Q44=makeQuery(id+"F4.imprint","IMPRINT",FACE,{"disambiguationData":[TD([[makeQuery(id+"F4.imprint","IMPRINT",EDGE,{"derivedFrom":subQ1}),-1.0]])]});}
            var Q45;
            Q45=makeQuery(id+"F4.imprint","IMPRINT",FACE,{"disambiguationData":[TD([[makeQuery(id+"F4.imprint","IMPRINT",EDGE,{"derivedFrom":sQuery(id+"F4.wireOp",EDGE,"E16.0.1.5")}),-1.0]])]});
            var Q46;
            Q46=makeQuery(id+"F4.imprint","IMPRINT",FACE,{"disambiguationData":[TD([[makeQuery(id+"F4.imprint","IMPRINT",EDGE,{"derivedFrom":sQuery(id+"F4.wireOp",EDGE,"E16.0.2.5")}),-1.0]])]});
            var Q47;
            Q47=makeQuery(id+"F4.imprint","IMPRINT",FACE,{"disambiguationData":[TD([[makeQuery(id+"F4.imprint","IMPRINT",EDGE,{"derivedFrom":sQuery(id+"F4.wireOp",EDGE,"E16.0.3.5")}),-1.0]])]});
            var Q48;
            Q48=makeQuery(id+"F4.imprint","IMPRINT",FACE,{"disambiguationData":[TD([[makeQuery(id+"F4.imprint","IMPRINT",EDGE,{"derivedFrom":sQuery(id+"F4.wireOp",EDGE,"E16.0.4.5")}),-1.0]])]});
            var Q49;
            Q49=makeQuery(id+"F4.imprint","IMPRINT",FACE,{"disambiguationData":[TD([[makeQuery(id+"F4.imprint","IMPRINT",EDGE,{"derivedFrom":sQuery(id+"F4.wireOp",EDGE,"E16.18.0.6")}),-1.0]])]});
            var Q50;
            Q50=makeQuery(id+"F4.imprint","IMPRINT",FACE,{"disambiguationData":[TD([[makeQuery(id+"F4.imprint","IMPRINT",EDGE,{"derivedFrom":sQuery(id+"F4.wireOp",EDGE,"E16.18.1.6")}),-1.0]])]});
            var Q51;
            Q51=makeQuery(id+"F4.imprint","IMPRINT",FACE,{"disambiguationData":[TD([[makeQuery(id+"F4.imprint","IMPRINT",EDGE,{"derivedFrom":sQuery(id+"F4.wireOp",EDGE,"E16.18.2.6")}),-1.0]])]});
            var Q52;
            Q52=makeQuery(id+"F4.imprint","IMPRINT",FACE,{"disambiguationData":[TD([[makeQuery(id+"F4.imprint","IMPRINT",EDGE,{"derivedFrom":sQuery(id+"F4.wireOp",EDGE,"E16.18.3.6")}),-1.0]])]});
            var Q53;
            {var subQ5=sQuery(id+"F4.wireOp",EDGE,"E16.18.4.6");Q53=makeQuery(id+"F4.imprint","IMPRINT",FACE,{"disambiguationData":[TD([[makeQuery(id+"F4.imprint","IMPRINT",EDGE,{"derivedFrom":subQ5}),-1.0]])]});}
            var Q54;
            {var subQ1=sQuery(id+"F4.wireOp",EDGE,"E16.12.0.6");Q54=makeQuery(id+"F4.imprint","IMPRINT",FACE,{"disambiguationData":[TD([[makeQuery(id+"F4.imprint","IMPRINT",EDGE,{"derivedFrom":subQ1}),-1.0]])]});}
            var Q55;
            Q55=makeQuery(id+"F4.imprint","IMPRINT",FACE,{"disambiguationData":[TD([[makeQuery(id+"F4.imprint","IMPRINT",EDGE,{"derivedFrom":sQuery(id+"F4.wireOp",EDGE,"E16.0.1.6")}),-1.0]])]});
            var Q56;
            Q56=makeQuery(id+"F4.imprint","IMPRINT",FACE,{"disambiguationData":[TD([[makeQuery(id+"F4.imprint","IMPRINT",EDGE,{"derivedFrom":sQuery(id+"F4.wireOp",EDGE,"E16.0.2.6")}),-1.0]])]});
            var Q57;
            Q57=makeQuery(id+"F4.imprint","IMPRINT",FACE,{"disambiguationData":[TD([[makeQuery(id+"F4.imprint","IMPRINT",EDGE,{"derivedFrom":sQuery(id+"F4.wireOp",EDGE,"E16.0.3.6")}),-1.0]])]});
            var Q58;
            Q58=makeQuery(id+"F4.imprint","IMPRINT",FACE,{"disambiguationData":[TD([[makeQuery(id+"F4.imprint","IMPRINT",EDGE,{"derivedFrom":sQuery(id+"F4.wireOp",EDGE,"E16.0.4.6")}),-1.0]])]});
            var Q59;
            Q59=makeQuery(id+"F4.imprint","IMPRINT",FACE,{"disambiguationData":[TD([[makeQuery(id+"F4.imprint","IMPRINT",EDGE,{"derivedFrom":sQuery(id+"F4.wireOp",EDGE,"E16.18.0.7")}),-1.0]])]});
            var Q60;
            Q60=makeQuery(id+"F4.imprint","IMPRINT",FACE,{"disambiguationData":[TD([[makeQuery(id+"F4.imprint","IMPRINT",EDGE,{"derivedFrom":sQuery(id+"F4.wireOp",EDGE,"E16.18.1.7")}),-1.0]])]});
            var Q61;
            Q61=makeQuery(id+"F4.imprint","IMPRINT",FACE,{"disambiguationData":[TD([[makeQuery(id+"F4.imprint","IMPRINT",EDGE,{"derivedFrom":sQuery(id+"F4.wireOp",EDGE,"E16.18.2.7")}),-1.0]])]});
            var Q62;
            Q62=makeQuery(id+"F4.imprint","IMPRINT",FACE,{"disambiguationData":[TD([[makeQuery(id+"F4.imprint","IMPRINT",EDGE,{"derivedFrom":sQuery(id+"F4.wireOp",EDGE,"E16.18.3.7")}),-1.0]])]});
            var Q63;
            {var subQ5=sQuery(id+"F4.wireOp",EDGE,"E16.18.4.7");Q63=makeQuery(id+"F4.imprint","IMPRINT",FACE,{"disambiguationData":[TD([[makeQuery(id+"F4.imprint","IMPRINT",EDGE,{"derivedFrom":subQ5}),-1.0]])]});}
            var Q64;
            {var subQ1=sQuery(id+"F4.wireOp",EDGE,"E16.12.0.7");Q64=makeQuery(id+"F4.imprint","IMPRINT",FACE,{"disambiguationData":[TD([[makeQuery(id+"F4.imprint","IMPRINT",EDGE,{"derivedFrom":subQ1}),-1.0]])]});}
            var Q65;
            Q65=makeQuery(id+"F4.imprint","IMPRINT",FACE,{"disambiguationData":[TD([[makeQuery(id+"F4.imprint","IMPRINT",EDGE,{"derivedFrom":sQuery(id+"F4.wireOp",EDGE,"E16.0.1.7")}),-1.0]])]});
            var Q66;
            Q66=makeQuery(id+"F4.imprint","IMPRINT",FACE,{"disambiguationData":[TD([[makeQuery(id+"F4.imprint","IMPRINT",EDGE,{"derivedFrom":sQuery(id+"F4.wireOp",EDGE,"E16.0.2.7")}),-1.0]])]});
            var Q67;
            Q67=makeQuery(id+"F4.imprint","IMPRINT",FACE,{"disambiguationData":[TD([[makeQuery(id+"F4.imprint","IMPRINT",EDGE,{"derivedFrom":sQuery(id+"F4.wireOp",EDGE,"E16.0.3.7")}),-1.0]])]});
            var Q68;
            Q68=makeQuery(id+"F4.imprint","IMPRINT",FACE,{"disambiguationData":[TD([[makeQuery(id+"F4.imprint","IMPRINT",EDGE,{"derivedFrom":sQuery(id+"F4.wireOp",EDGE,"E16.0.4.7")}),-1.0]])]});
            var Q69;
            Q69=makeQuery(id+"F4.imprint","IMPRINT",FACE,{"disambiguationData":[TD([[makeQuery(id+"F4.imprint","IMPRINT",EDGE,{"derivedFrom":sQuery(id+"F4.wireOp",EDGE,"E16.18.0.8")}),-1.0]])]});
            var Q70;
            Q70=makeQuery(id+"F4.imprint","IMPRINT",FACE,{"disambiguationData":[TD([[makeQuery(id+"F4.imprint","IMPRINT",EDGE,{"derivedFrom":sQuery(id+"F4.wireOp",EDGE,"E16.18.1.8")}),-1.0]])]});
            var Q71;
            Q71=makeQuery(id+"F4.imprint","IMPRINT",FACE,{"disambiguationData":[TD([[makeQuery(id+"F4.imprint","IMPRINT",EDGE,{"derivedFrom":sQuery(id+"F4.wireOp",EDGE,"E16.18.2.8")}),-1.0]])]});
            var Q72;
            Q72=makeQuery(id+"F4.imprint","IMPRINT",FACE,{"disambiguationData":[TD([[makeQuery(id+"F4.imprint","IMPRINT",EDGE,{"derivedFrom":sQuery(id+"F4.wireOp",EDGE,"E16.18.3.8")}),-1.0]])]});
            var Q73;
            {var subQ5=sQuery(id+"F4.wireOp",EDGE,"E16.18.4.8");Q73=makeQuery(id+"F4.imprint","IMPRINT",FACE,{"disambiguationData":[TD([[makeQuery(id+"F4.imprint","IMPRINT",EDGE,{"derivedFrom":subQ5}),-1.0]])]});}
            var Q74;
            {var subQ1=sQuery(id+"F4.wireOp",EDGE,"E16.12.0.8");Q74=makeQuery(id+"F4.imprint","IMPRINT",FACE,{"disambiguationData":[TD([[makeQuery(id+"F4.imprint","IMPRINT",EDGE,{"derivedFrom":subQ1}),-1.0]])]});}
            var Q75;
            Q75=makeQuery(id+"F4.imprint","IMPRINT",FACE,{"disambiguationData":[TD([[makeQuery(id+"F4.imprint","IMPRINT",EDGE,{"derivedFrom":sQuery(id+"F4.wireOp",EDGE,"E16.0.1.8")}),-1.0]])]});
            var Q76;
            Q76=makeQuery(id+"F4.imprint","IMPRINT",FACE,{"disambiguationData":[TD([[makeQuery(id+"F4.imprint","IMPRINT",EDGE,{"derivedFrom":sQuery(id+"F4.wireOp",EDGE,"E16.0.2.8")}),-1.0]])]});
            var Q77;
            Q77=makeQuery(id+"F4.imprint","IMPRINT",FACE,{"disambiguationData":[TD([[makeQuery(id+"F4.imprint","IMPRINT",EDGE,{"derivedFrom":sQuery(id+"F4.wireOp",EDGE,"E16.0.3.8")}),-1.0]])]});
            var Q78;
            Q78=makeQuery(id+"F4.imprint","IMPRINT",FACE,{"disambiguationData":[TD([[makeQuery(id+"F4.imprint","IMPRINT",EDGE,{"derivedFrom":sQuery(id+"F4.wireOp",EDGE,"E16.0.4.8")}),-1.0]])]});
            var Q79;
            Q79=makeQuery(id+"F4.imprint","IMPRINT",FACE,{"disambiguationData":[TD([[makeQuery(id+"F4.imprint","IMPRINT",EDGE,{"derivedFrom":sQuery(id+"F4.wireOp",EDGE,"E16.18.0.9")}),-1.0]])]});
            var Q80;
            Q80=makeQuery(id+"F4.imprint","IMPRINT",FACE,{"disambiguationData":[TD([[makeQuery(id+"F4.imprint","IMPRINT",EDGE,{"derivedFrom":sQuery(id+"F4.wireOp",EDGE,"E16.18.1.9")}),-1.0]])]});
            var Q81;
            Q81=makeQuery(id+"F4.imprint","IMPRINT",FACE,{"disambiguationData":[TD([[makeQuery(id+"F4.imprint","IMPRINT",EDGE,{"derivedFrom":sQuery(id+"F4.wireOp",EDGE,"E16.18.2.9")}),-1.0]])]});
            var Q82;
            Q82=makeQuery(id+"F4.imprint","IMPRINT",FACE,{"disambiguationData":[TD([[makeQuery(id+"F4.imprint","IMPRINT",EDGE,{"derivedFrom":sQuery(id+"F4.wireOp",EDGE,"E16.18.3.9")}),-1.0]])]});
            var Q83;
            {var subQ5=sQuery(id+"F4.wireOp",EDGE,"E16.18.4.9");Q83=makeQuery(id+"F4.imprint","IMPRINT",FACE,{"disambiguationData":[TD([[makeQuery(id+"F4.imprint","IMPRINT",EDGE,{"derivedFrom":subQ5}),-1.0]])]});}
            var Q84;
            {var subQ1=sQuery(id+"F4.wireOp",EDGE,"E16.12.0.9");Q84=makeQuery(id+"F4.imprint","IMPRINT",FACE,{"disambiguationData":[TD([[makeQuery(id+"F4.imprint","IMPRINT",EDGE,{"derivedFrom":subQ1}),-1.0]])]});}
            var Q85;
            Q85=makeQuery(id+"F4.imprint","IMPRINT",FACE,{"disambiguationData":[TD([[makeQuery(id+"F4.imprint","IMPRINT",EDGE,{"derivedFrom":sQuery(id+"F4.wireOp",EDGE,"E16.0.1.9")}),-1.0]])]});
            var Q86;
            Q86=makeQuery(id+"F4.imprint","IMPRINT",FACE,{"disambiguationData":[TD([[makeQuery(id+"F4.imprint","IMPRINT",EDGE,{"derivedFrom":sQuery(id+"F4.wireOp",EDGE,"E16.0.2.9")}),-1.0]])]});
            var Q87;
            Q87=makeQuery(id+"F4.imprint","IMPRINT",FACE,{"disambiguationData":[TD([[makeQuery(id+"F4.imprint","IMPRINT",EDGE,{"derivedFrom":sQuery(id+"F4.wireOp",EDGE,"E16.0.3.9")}),-1.0]])]});
            var Q88;
            Q88=makeQuery(id+"F4.imprint","IMPRINT",FACE,{"disambiguationData":[TD([[makeQuery(id+"F4.imprint","IMPRINT",EDGE,{"derivedFrom":sQuery(id+"F4.wireOp",EDGE,"E16.0.4.9")}),-1.0]])]});
            var Q89;
            Q89=makeQuery(id+"F4.imprint","IMPRINT",FACE,{"disambiguationData":[TD([[makeQuery(id+"F4.imprint","IMPRINT",EDGE,{"derivedFrom":sQuery(id+"F4.wireOp",EDGE,"E16.18.0.10")}),-1.0]])]});
            var Q90;
            Q90=makeQuery(id+"F4.imprint","IMPRINT",FACE,{"disambiguationData":[TD([[makeQuery(id+"F4.imprint","IMPRINT",EDGE,{"derivedFrom":sQuery(id+"F4.wireOp",EDGE,"E16.18.1.10")}),-1.0]])]});
            var Q91;
            Q91=makeQuery(id+"F4.imprint","IMPRINT",FACE,{"disambiguationData":[TD([[makeQuery(id+"F4.imprint","IMPRINT",EDGE,{"derivedFrom":sQuery(id+"F4.wireOp",EDGE,"E16.18.2.10")}),-1.0]])]});
            var Q92;
            Q92=makeQuery(id+"F4.imprint","IMPRINT",FACE,{"disambiguationData":[TD([[makeQuery(id+"F4.imprint","IMPRINT",EDGE,{"derivedFrom":sQuery(id+"F4.wireOp",EDGE,"E16.18.3.10")}),-1.0]])]});
            var Q93;
            {var subQ6=sQuery(id+"F4.wireOp",EDGE,"E16.18.4.10");Q93=makeQuery(id+"F4.imprint","IMPRINT",FACE,{"disambiguationData":[TD([[makeQuery(id+"F4.imprint","IMPRINT",EDGE,{"derivedFrom":subQ6}),-1.0]])]});}
            var Q94;
            {var subQ6=sQuery(id+"F4.wireOp",EDGE,"E16.12.0.10");Q94=makeQuery(id+"F4.imprint","IMPRINT",FACE,{"disambiguationData":[TD([[makeQuery(id+"F4.imprint","IMPRINT",EDGE,{"derivedFrom":subQ6}),-1.0]])]});}
            var Q95;
            Q95=makeQuery(id+"F4.imprint","IMPRINT",FACE,{"disambiguationData":[TD([[makeQuery(id+"F4.imprint","IMPRINT",EDGE,{"derivedFrom":sQuery(id+"F4.wireOp",EDGE,"E16.0.1.10")}),-1.0]])]});
            var Q96;
            Q96=makeQuery(id+"F4.imprint","IMPRINT",FACE,{"disambiguationData":[TD([[makeQuery(id+"F4.imprint","IMPRINT",EDGE,{"derivedFrom":sQuery(id+"F4.wireOp",EDGE,"E16.0.2.10")}),-1.0]])]});
            var Q97;
            Q97=makeQuery(id+"F4.imprint","IMPRINT",FACE,{"disambiguationData":[TD([[makeQuery(id+"F4.imprint","IMPRINT",EDGE,{"derivedFrom":sQuery(id+"F4.wireOp",EDGE,"E16.0.3.10")}),-1.0]])]});
            var Q98;
            Q98=makeQuery(id+"F4.imprint","IMPRINT",FACE,{"disambiguationData":[TD([[makeQuery(id+"F4.imprint","IMPRINT",EDGE,{"derivedFrom":sQuery(id+"F4.wireOp",EDGE,"E16.0.4.10")}),-1.0]])]});
            var Q99;
            Q99=makeQuery(id+"F4.imprint","IMPRINT",FACE,{"disambiguationData":[TD([[makeQuery(id+"F4.imprint","IMPRINT",EDGE,{"derivedFrom":sQuery(id+"F4.wireOp",EDGE,"E16.18.0.11")}),-1.0]])]});
            var Q100;
            Q100=makeQuery(id+"F4.imprint","IMPRINT",FACE,{"disambiguationData":[TD([[makeQuery(id+"F4.imprint","IMPRINT",EDGE,{"derivedFrom":sQuery(id+"F4.wireOp",EDGE,"E16.18.1.11")}),-1.0]])]});
            var Q101;
            Q101=makeQuery(id+"F4.imprint","IMPRINT",FACE,{"disambiguationData":[TD([[makeQuery(id+"F4.imprint","IMPRINT",EDGE,{"derivedFrom":sQuery(id+"F4.wireOp",EDGE,"E16.18.2.11")}),-1.0]])]});
            var Q102;
            Q102=makeQuery(id+"F4.imprint","IMPRINT",FACE,{"disambiguationData":[TD([[makeQuery(id+"F4.imprint","IMPRINT",EDGE,{"derivedFrom":sQuery(id+"F4.wireOp",EDGE,"E16.18.3.11")}),-1.0]])]});
            var Q103;
            {var subQ5=sQuery(id+"F4.wireOp",EDGE,"E16.18.4.11");Q103=makeQuery(id+"F4.imprint","IMPRINT",FACE,{"disambiguationData":[TD([[makeQuery(id+"F4.imprint","IMPRINT",EDGE,{"derivedFrom":subQ5}),-1.0]])]});}
            var Q104;
            {var subQ1=sQuery(id+"F4.wireOp",EDGE,"E16.12.0.11");Q104=makeQuery(id+"F4.imprint","IMPRINT",FACE,{"disambiguationData":[TD([[makeQuery(id+"F4.imprint","IMPRINT",EDGE,{"derivedFrom":subQ1}),-1.0]])]});}
            var Q105;
            Q105=makeQuery(id+"F4.imprint","IMPRINT",FACE,{"disambiguationData":[TD([[makeQuery(id+"F4.imprint","IMPRINT",EDGE,{"derivedFrom":sQuery(id+"F4.wireOp",EDGE,"E16.0.1.11")}),-1.0]])]});
            var Q106;
            Q106=makeQuery(id+"F4.imprint","IMPRINT",FACE,{"disambiguationData":[TD([[makeQuery(id+"F4.imprint","IMPRINT",EDGE,{"derivedFrom":sQuery(id+"F4.wireOp",EDGE,"E16.0.2.11")}),-1.0]])]});
            var Q107;
            Q107=makeQuery(id+"F4.imprint","IMPRINT",FACE,{"disambiguationData":[TD([[makeQuery(id+"F4.imprint","IMPRINT",EDGE,{"derivedFrom":sQuery(id+"F4.wireOp",EDGE,"E16.0.3.11")}),-1.0]])]});
            var Q108;
            Q108=makeQuery(id+"F4.imprint","IMPRINT",FACE,{"disambiguationData":[TD([[makeQuery(id+"F4.imprint","IMPRINT",EDGE,{"derivedFrom":sQuery(id+"F4.wireOp",EDGE,"E16.0.4.11")}),-1.0]])]});
            var Q109;
            Q109=makeQuery(id+"F4.imprint","IMPRINT",FACE,{"disambiguationData":[TD([[makeQuery(id+"F4.imprint","IMPRINT",EDGE,{"derivedFrom":sQuery(id+"F4.wireOp",EDGE,"E16.18.0.12")}),-1.0]])]});
            var Q110;
            Q110=makeQuery(id+"F4.imprint","IMPRINT",FACE,{"disambiguationData":[TD([[makeQuery(id+"F4.imprint","IMPRINT",EDGE,{"derivedFrom":sQuery(id+"F4.wireOp",EDGE,"E16.18.1.12")}),-1.0]])]});
            var Q111;
            Q111=makeQuery(id+"F4.imprint","IMPRINT",FACE,{"disambiguationData":[TD([[makeQuery(id+"F4.imprint","IMPRINT",EDGE,{"derivedFrom":sQuery(id+"F4.wireOp",EDGE,"E16.18.2.12")}),-1.0]])]});
            var Q112;
            Q112=makeQuery(id+"F4.imprint","IMPRINT",FACE,{"disambiguationData":[TD([[makeQuery(id+"F4.imprint","IMPRINT",EDGE,{"derivedFrom":sQuery(id+"F4.wireOp",EDGE,"E16.18.3.12")}),-1.0]])]});
            var Q113;
            {var subQ5=sQuery(id+"F4.wireOp",EDGE,"E16.18.4.12");Q113=makeQuery(id+"F4.imprint","IMPRINT",FACE,{"disambiguationData":[TD([[makeQuery(id+"F4.imprint","IMPRINT",EDGE,{"derivedFrom":subQ5}),-1.0]])]});}
            var Q114;
            {var subQ5=sQuery(id+"F4.wireOp",EDGE,"E16.15.0.12");Q114=makeQuery(id+"F4.imprint","IMPRINT",FACE,{"disambiguationData":[TD([[makeQuery(id+"F4.imprint","IMPRINT",EDGE,{"derivedFrom":subQ5}),-1.0]])]});}
            var Q115;
            Q115=makeQuery(id+"F4.imprint","IMPRINT",FACE,{"disambiguationData":[TD([[makeQuery(id+"F4.imprint","IMPRINT",EDGE,{"derivedFrom":sQuery(id+"F4.wireOp",EDGE,"E16.0.1.12")}),-1.0]])]});
            var Q116;
            Q116=makeQuery(id+"F4.imprint","IMPRINT",FACE,{"disambiguationData":[TD([[makeQuery(id+"F4.imprint","IMPRINT",EDGE,{"derivedFrom":sQuery(id+"F4.wireOp",EDGE,"E16.0.2.12")}),-1.0]])]});
            var Q117;
            Q117=makeQuery(id+"F4.imprint","IMPRINT",FACE,{"disambiguationData":[TD([[makeQuery(id+"F4.imprint","IMPRINT",EDGE,{"derivedFrom":sQuery(id+"F4.wireOp",EDGE,"E16.0.3.12")}),-1.0]])]});
            var Q118;
            Q118=makeQuery(id+"F4.imprint","IMPRINT",FACE,{"disambiguationData":[TD([[makeQuery(id+"F4.imprint","IMPRINT",EDGE,{"derivedFrom":sQuery(id+"F4.wireOp",EDGE,"E16.0.4.12")}),-1.0]])]});
            var Q119;
            Q119=makeQuery(id+"F4.imprint","IMPRINT",FACE,{"disambiguationData":[TD([[makeQuery(id+"F4.imprint","IMPRINT",EDGE,{"derivedFrom":sQuery(id+"F4.wireOp",EDGE,"E16.18.1.13")}),-1.0]])]});
            var Q120;
            Q120=makeQuery(id+"F4.imprint","IMPRINT",FACE,{"disambiguationData":[TD([[makeQuery(id+"F4.imprint","IMPRINT",EDGE,{"derivedFrom":sQuery(id+"F4.wireOp",EDGE,"E16.18.2.13")}),-1.0]])]});
            var Q121;
            Q121=makeQuery(id+"F4.imprint","IMPRINT",FACE,{"disambiguationData":[TD([[makeQuery(id+"F4.imprint","IMPRINT",EDGE,{"derivedFrom":sQuery(id+"F4.wireOp",EDGE,"E16.18.3.13")}),-1.0]])]});
            var Q122;
            {var subQ5=sQuery(id+"F4.wireOp",EDGE,"E16.18.4.13");Q122=makeQuery(id+"F4.imprint","IMPRINT",FACE,{"disambiguationData":[TD([[makeQuery(id+"F4.imprint","IMPRINT",EDGE,{"derivedFrom":subQ5}),-1.0]])]});}
            var Q123;
            {var subQ0=sQuery(id+"F4.wireOp",EDGE,"E16.24.1.14");Q123=makeQuery(id+"F4.imprint","IMPRINT",FACE,{"disambiguationData":[TD([[makeQuery(id+"F4.imprint","IMPRINT",EDGE,{"derivedFrom":subQ0}),-1.0]])]});}
            var Q124;
            Q124=makeQuery(id+"F4.imprint","IMPRINT",FACE,{"disambiguationData":[TD([[makeQuery(id+"F4.imprint","IMPRINT",EDGE,{"derivedFrom":sQuery(id+"F4.wireOp",EDGE,"E16.0.2.13")}),-1.0]])]});
            var Q125;
            {var subQ0=sQuery(id+"F4.wireOp",EDGE,"E16.24.2.14");Q125=makeQuery(id+"F4.imprint","IMPRINT",FACE,{"disambiguationData":[TD([[makeQuery(id+"F4.imprint","IMPRINT",EDGE,{"derivedFrom":subQ0}),-1.0]])]});}
            var Q126;
            Q126=makeQuery(id+"F4.imprint","IMPRINT",FACE,{"disambiguationData":[TD([[makeQuery(id+"F4.imprint","IMPRINT",EDGE,{"derivedFrom":sQuery(id+"F4.wireOp",EDGE,"E16.0.3.13")}),-1.0]])]});
            var Q127;
            {var subQ0=sQuery(id+"F4.wireOp",EDGE,"E16.24.3.14");Q127=makeQuery(id+"F4.imprint","IMPRINT",FACE,{"disambiguationData":[TD([[makeQuery(id+"F4.imprint","IMPRINT",EDGE,{"derivedFrom":subQ0}),-1.0]])]});}
            var Q128;
            Q128=makeQuery(id+"F4.imprint","IMPRINT",FACE,{"disambiguationData":[TD([[makeQuery(id+"F4.imprint","IMPRINT",EDGE,{"derivedFrom":sQuery(id+"F4.wireOp",EDGE,"E16.0.4.13")}),-1.0]])]});
            var Q129;
            {var subQ8=sQuery(id+"F4.wireOp",EDGE,"E16.0.1.13");Q129=makeQuery(id+"F4.imprint","IMPRINT",FACE,{"disambiguationData":[TD([[makeQuery(id+"F4.imprint","IMPRINT",EDGE,{"derivedFrom":subQ8}),-1.0]])]});}
            var Q130;
            Q130=makeQuery(id+"F4.imprint","IMPRINT",FACE,{"disambiguationData":[TD([[makeQuery(id+"F4.imprint","IMPRINT",EDGE,{"derivedFrom":sQuery(id+"F4.wireOp",EDGE,"E15.0.4.1")}),-1.0]])]});
            var Q131;
            {var subQ5=sQuery(id+"F4.wireOp",EDGE,"E16.18.4.2");Q131=makeQuery(id+"F4.imprint","IMPRINT",FACE,{"disambiguationData":[TD([[makeQuery(id+"F4.imprint","IMPRINT",EDGE,{"derivedFrom":subQ5}),-1.0]])]});}
            var Q132;
            {var subQ4=sQuery(id+"F4.wireOp",EDGE,"E16.24.0.13");Q132=makeQuery(id+"F4.imprint","IMPRINT",FACE,{"disambiguationData":[TD([[makeQuery(id+"F4.imprint","IMPRINT",EDGE,{"derivedFrom":subQ4}),-1.0]])]});}
            var Q133;
            {var subQ0=sQuery(id+"F4.wireOp",EDGE,"E16.24.4.14");var subQ1=sQuery(id+"F4.wireOp",EDGE,"E16.18.4.14");var subQ2=makeQuery(id+"F4.imprint","INTERSECT",VERTEX,{"derivedFrom":[subQ1,subQ0]});Q133=makeQuery(id+"F4.imprint","IMPRINT",FACE,{"disambiguationData":[TD([[makeQuery(id+"F4.imprint","IMPRINT",EDGE,{"disambiguationData":[TD([[subQ2,1.0]])],"derivedFrom":subQ1}),-1.0]])]});}
            var Q134;
            {var subQ1=sQuery(id+"F4.wireOp",EDGE,"E15.21.4.1");Q134=makeQuery(id+"F4.imprint","IMPRINT",FACE,{"disambiguationData":[TD([[makeQuery(id+"F4.imprint","IMPRINT",EDGE,{"derivedFrom":subQ1}),-1.0]])]});}
            var Q135;
            {var subQ0=sQuery(id+"F4.wireOp",EDGE,"E15.9.4.0");Q135=makeQuery(id+"F4.imprint","IMPRINT",FACE,{"disambiguationData":[TD([[makeQuery(id+"F4.imprint","IMPRINT",EDGE,{"derivedFrom":subQ0}),-1.0]])]});}
            var Q136;
            {var subQ0=sQuery(id+"F4.wireOp",EDGE,"E14.0.1.10");Q136=makeQuery(id+"F4.imprint","IMPRINT",FACE,{"disambiguationData":[TD([[makeQuery(id+"F4.imprint","IMPRINT",EDGE,{"derivedFrom":subQ0}),-1.0]])]});}
            var Q137;
            Q137=makeQuery(id+"F1.opExtrude","CAP_FACE",FACE,{"disambiguationData":[OSD([sQuery(id+"F0.wireOp",EDGE,"E0.bottom"),sQuery(id+"F0.wireOp",EDGE,"E0.top"),sQuery(id+"F0.wireOp",EDGE,"E0.left"),sQuery(id+"F0.wireOp",EDGE,"E0.right")])],"isStart":true});
            extrude(context, id + "F5", {"entities" : qUnion([Q0, Q1, Q2, Q3, Q4, Q5, Q6, Q7, Q8, Q9, Q10, Q11, Q12, Q13, Q14, Q15, Q16, Q17, Q18, Q19, Q20, Q21, Q22, Q23, Q24, Q25, Q26, Q27, Q28, Q29, Q30, Q31, Q32, Q33, Q34, Q35, Q36, Q37, Q38, Q39, Q40, Q41, Q42, Q43, Q44, Q45, Q46, Q47, Q48, Q49, Q50, Q51, Q52, Q53, Q54, Q55, Q56, Q57, Q58, Q59, Q60, Q61, Q62, Q63, Q64, Q65, Q66, Q67, Q68, Q69, Q70, Q71, Q72, Q73, Q74, Q75, Q76, Q77, Q78, Q79, Q80, Q81, Q82, Q83, Q84, Q85, Q86, Q87, Q88, Q89, Q90, Q91, Q92, Q93, Q94, Q95, Q96, Q97, Q98, Q99, Q100, Q101, Q102, Q103, Q104, Q105, Q106, Q107, Q108, Q109, Q110, Q111, Q112, Q113, Q114, Q115, Q116, Q117, Q118, Q119, Q120, Q121, Q122, Q123, Q124, Q125, Q126, Q127, Q128, Q129, Q130, Q131, Q132, Q133, Q134, Q135, Q136]), "operationType" : NewBodyOperationType.REMOVE, "endBound" : BoundingType.UP_TO_SURFACE, "oppositeDirection" : true, "depth" : 25 * mm, "endBoundEntityFace" : qUnion([Q137]), "offsetDistance" : 25 * mm});
        }
        {
            var Q0;
            Q0=makeQuery(id+"F3.opSweep","SWEPT_FACE",FACE,{"disambiguationData":[OSD([sQuery(id+"F0.wireOp",EDGE,"E0.bottom"),sQuery(id+"F2.wireOp",EDGE,"E7.left")])]});
            var sketch = newSketch(context, id + "F6", { "sketchPlane" : qUnion([Q0])});
            skLineSegment(sketch, "E25.0", {"start": v(-51, 17.8) * mm, "end": v(90, 17.8) * mm});
            skLineSegment(sketch, "E26.0", {"start": v(-48.5, 20.3) * mm, "end": v(-48.5, 0.3) * mm});
            skLineSegment(sketch, "E27.0", {"start": v(-51, 2.8) * mm, "end": v(90, 2.8) * mm});
            skLineSegment(sketch, "E28.0", {"start": v(87.5, 20.3) * mm, "end": v(87.5, 0.3) * mm});
            skCircle(sketch, "E29.cCircle", {"center": v(-43.75, 21.24) * mm, "radius": 2.5 * mm, "construction": true});
            skLineSegment(sketch, "E29.0", {"start": v(-42.3, 18.74) * mm, "end": v(-45.2, 18.74) * mm});
            skLineSegment(sketch, "E29.1", {"start": v(-45.2, 18.74) * mm, "end": v(-46.64, 21.24) * mm});
            skLineSegment(sketch, "E29.2", {"start": v(-46.64, 21.24) * mm, "end": v(-45.2, 23.74) * mm});
            skLineSegment(sketch, "E29.3", {"start": v(-45.2, 23.74) * mm, "end": v(-42.3, 23.74) * mm});
            skLineSegment(sketch, "E29.4", {"start": v(-42.3, 23.74) * mm, "end": v(-40.86, 21.24) * mm});
            skLineSegment(sketch, "E29.5", {"start": v(-40.86, 21.24) * mm, "end": v(-42.3, 18.74) * mm});
            skPoint(sketch, "E29.0.midPoint", {"position": v(-43.75, 18.74) * mm});
            skCircle(sketch, "E30.cCircle", {"center": v(-49.16, 18.11) * mm, "radius": 2.5 * mm, "construction": true});
            skLineSegment(sketch, "E30.0", {"start": v(-47.72, 15.61) * mm, "end": v(-50.6, 15.61) * mm});
            skLineSegment(sketch, "E30.1", {"start": v(-50.6, 15.61) * mm, "end": v(-52.05, 18.11) * mm});
            skLineSegment(sketch, "E30.2", {"start": v(-52.05, 18.11) * mm, "end": v(-50.6, 20.61) * mm});
            skLineSegment(sketch, "E30.3", {"start": v(-50.6, 20.61) * mm, "end": v(-47.72, 20.61) * mm});
            skLineSegment(sketch, "E30.4", {"start": v(-47.72, 20.61) * mm, "end": v(-46.28, 18.11) * mm});
            skLineSegment(sketch, "E30.5", {"start": v(-46.28, 18.11) * mm, "end": v(-47.72, 15.61) * mm});
            skPoint(sketch, "E30.0.midPoint", {"position": v(-49.16, 15.61) * mm});
            skLineSegment(sketch, "E31.0.1.0", {"start": v(-50.6, 14.36) * mm, "end": v(-47.72, 14.36) * mm});
            skLineSegment(sketch, "E31.0.1.1", {"start": v(-52.05, 11.86) * mm, "end": v(-50.6, 14.36) * mm});
            skLineSegment(sketch, "E31.0.1.2", {"start": v(-50.6, 9.36) * mm, "end": v(-52.05, 11.86) * mm});
            skLineSegment(sketch, "E31.0.1.3", {"start": v(-47.72, 9.36) * mm, "end": v(-50.6, 9.36) * mm});
            skLineSegment(sketch, "E31.0.1.4", {"start": v(-46.28, 11.86) * mm, "end": v(-47.72, 9.36) * mm});
            skLineSegment(sketch, "E31.0.1.5", {"start": v(-47.72, 14.36) * mm, "end": v(-46.28, 11.86) * mm});
            skLineSegment(sketch, "E31.0.1.6", {"start": v(-45.2, 12.49) * mm, "end": v(-46.64, 14.99) * mm});
            skLineSegment(sketch, "E31.0.1.7", {"start": v(-46.64, 14.99) * mm, "end": v(-45.2, 17.49) * mm});
            skLineSegment(sketch, "E31.0.1.8", {"start": v(-45.2, 17.49) * mm, "end": v(-42.3, 17.49) * mm});
            skLineSegment(sketch, "E31.0.1.9", {"start": v(-42.3, 17.49) * mm, "end": v(-40.86, 14.99) * mm});
            skLineSegment(sketch, "E31.0.1.10", {"start": v(-40.86, 14.99) * mm, "end": v(-42.3, 12.49) * mm});
            skLineSegment(sketch, "E31.0.1.11", {"start": v(-42.3, 12.49) * mm, "end": v(-45.2, 12.49) * mm});
            skLineSegment(sketch, "E31.1.0.0", {"start": v(-39.61, 20.61) * mm, "end": v(-36.73, 20.61) * mm});
            skLineSegment(sketch, "E31.1.0.1", {"start": v(-41.06, 18.11) * mm, "end": v(-39.61, 20.61) * mm});
            skLineSegment(sketch, "E31.1.0.2", {"start": v(-39.61, 15.61) * mm, "end": v(-41.06, 18.11) * mm});
            skLineSegment(sketch, "E31.1.0.3", {"start": v(-36.73, 15.61) * mm, "end": v(-39.61, 15.61) * mm});
            skLineSegment(sketch, "E31.1.0.4", {"start": v(-35.28, 18.11) * mm, "end": v(-36.73, 15.61) * mm});
            skLineSegment(sketch, "E31.1.0.5", {"start": v(-36.73, 20.61) * mm, "end": v(-35.28, 18.11) * mm});
            skLineSegment(sketch, "E31.1.0.6", {"start": v(-34.2, 18.74) * mm, "end": v(-35.65, 21.24) * mm});
            skLineSegment(sketch, "E31.1.0.7", {"start": v(-35.65, 21.24) * mm, "end": v(-34.2, 23.74) * mm});
            skLineSegment(sketch, "E31.1.0.8", {"start": v(-34.2, 23.74) * mm, "end": v(-31.32, 23.74) * mm});
            skLineSegment(sketch, "E31.1.0.9", {"start": v(-31.32, 23.74) * mm, "end": v(-29.87, 21.24) * mm});
            skLineSegment(sketch, "E31.1.0.10", {"start": v(-29.87, 21.24) * mm, "end": v(-31.32, 18.74) * mm});
            skLineSegment(sketch, "E31.1.0.11", {"start": v(-31.32, 18.74) * mm, "end": v(-34.2, 18.74) * mm});
            skLineSegment(sketch, "E31.1.1.0", {"start": v(-39.61, 14.36) * mm, "end": v(-36.73, 14.36) * mm});
            skLineSegment(sketch, "E31.1.1.1", {"start": v(-41.06, 11.86) * mm, "end": v(-39.61, 14.36) * mm});
            skLineSegment(sketch, "E31.1.1.2", {"start": v(-39.61, 9.36) * mm, "end": v(-41.06, 11.86) * mm});
            skLineSegment(sketch, "E31.1.1.3", {"start": v(-36.73, 9.36) * mm, "end": v(-39.61, 9.36) * mm});
            skLineSegment(sketch, "E31.1.1.4", {"start": v(-35.28, 11.86) * mm, "end": v(-36.73, 9.36) * mm});
            skLineSegment(sketch, "E31.1.1.5", {"start": v(-36.73, 14.36) * mm, "end": v(-35.28, 11.86) * mm});
            skLineSegment(sketch, "E31.1.1.6", {"start": v(-34.2, 12.49) * mm, "end": v(-35.65, 14.99) * mm});
            skLineSegment(sketch, "E31.1.1.7", {"start": v(-35.65, 14.99) * mm, "end": v(-34.2, 17.49) * mm});
            skLineSegment(sketch, "E31.1.1.8", {"start": v(-34.2, 17.49) * mm, "end": v(-31.32, 17.49) * mm});
            skLineSegment(sketch, "E31.1.1.9", {"start": v(-31.32, 17.49) * mm, "end": v(-29.87, 14.99) * mm});
            skLineSegment(sketch, "E31.1.1.10", {"start": v(-29.87, 14.99) * mm, "end": v(-31.32, 12.49) * mm});
            skLineSegment(sketch, "E31.1.1.11", {"start": v(-31.32, 12.49) * mm, "end": v(-34.2, 12.49) * mm});
            skLineSegment(sketch, "E31.2.0.0", {"start": v(-28.62, 20.61) * mm, "end": v(-25.73, 20.61) * mm});
            skLineSegment(sketch, "E31.2.0.1", {"start": v(-30.07, 18.11) * mm, "end": v(-28.62, 20.61) * mm});
            skLineSegment(sketch, "E31.2.0.2", {"start": v(-28.62, 15.61) * mm, "end": v(-30.07, 18.11) * mm});
            skLineSegment(sketch, "E31.2.0.3", {"start": v(-25.73, 15.61) * mm, "end": v(-28.62, 15.61) * mm});
            skLineSegment(sketch, "E31.2.0.4", {"start": v(-24.3, 18.11) * mm, "end": v(-25.73, 15.61) * mm});
            skLineSegment(sketch, "E31.2.0.5", {"start": v(-25.73, 20.61) * mm, "end": v(-24.3, 18.11) * mm});
            skLineSegment(sketch, "E31.2.0.6", {"start": v(-23.2, 18.74) * mm, "end": v(-24.65, 21.24) * mm});
            skLineSegment(sketch, "E31.2.0.7", {"start": v(-24.65, 21.24) * mm, "end": v(-23.2, 23.74) * mm});
            skLineSegment(sketch, "E31.2.0.8", {"start": v(-23.2, 23.74) * mm, "end": v(-20.32, 23.74) * mm});
            skLineSegment(sketch, "E31.2.0.9", {"start": v(-20.32, 23.74) * mm, "end": v(-18.88, 21.24) * mm});
            skLineSegment(sketch, "E31.2.0.10", {"start": v(-18.88, 21.24) * mm, "end": v(-20.32, 18.74) * mm});
            skLineSegment(sketch, "E31.2.0.11", {"start": v(-20.32, 18.74) * mm, "end": v(-23.2, 18.74) * mm});
            skLineSegment(sketch, "E31.2.1.0", {"start": v(-28.62, 14.36) * mm, "end": v(-25.73, 14.36) * mm});
            skLineSegment(sketch, "E31.2.1.1", {"start": v(-30.07, 11.86) * mm, "end": v(-28.62, 14.36) * mm});
            skLineSegment(sketch, "E31.2.1.2", {"start": v(-28.62, 9.36) * mm, "end": v(-30.07, 11.86) * mm});
            skLineSegment(sketch, "E31.2.1.3", {"start": v(-25.73, 9.36) * mm, "end": v(-28.62, 9.36) * mm});
            skLineSegment(sketch, "E31.2.1.4", {"start": v(-24.3, 11.86) * mm, "end": v(-25.73, 9.36) * mm});
            skLineSegment(sketch, "E31.2.1.5", {"start": v(-25.73, 14.36) * mm, "end": v(-24.3, 11.86) * mm});
            skLineSegment(sketch, "E31.2.1.6", {"start": v(-23.2, 12.49) * mm, "end": v(-24.65, 14.99) * mm});
            skLineSegment(sketch, "E31.2.1.7", {"start": v(-24.65, 14.99) * mm, "end": v(-23.2, 17.49) * mm});
            skLineSegment(sketch, "E31.2.1.8", {"start": v(-23.2, 17.49) * mm, "end": v(-20.32, 17.49) * mm});
            skLineSegment(sketch, "E31.2.1.9", {"start": v(-20.32, 17.49) * mm, "end": v(-18.88, 14.99) * mm});
            skLineSegment(sketch, "E31.2.1.10", {"start": v(-18.88, 14.99) * mm, "end": v(-20.32, 12.49) * mm});
            skLineSegment(sketch, "E31.2.1.11", {"start": v(-20.32, 12.49) * mm, "end": v(-23.2, 12.49) * mm});
            skLineSegment(sketch, "E31.direction1", {"start": v(-50.6, 20.61) * mm, "end": v(-39.61, 20.61) * mm, "construction": true});
            skLineSegment(sketch, "E31.direction2", {"start": v(-50.6, 20.61) * mm, "end": v(-50.6, 14.36) * mm, "construction": true});
            skLineSegment(sketch, "E32.0.0.2", {"start": v(-50.6, 8.11) * mm, "end": v(-47.72, 8.11) * mm});
            skLineSegment(sketch, "E32.3.0.2", {"start": v(-52.05, 5.61) * mm, "end": v(-50.6, 8.11) * mm});
            skLineSegment(sketch, "E32.6.0.2", {"start": v(-50.6, 3.11) * mm, "end": v(-52.05, 5.61) * mm});
            skLineSegment(sketch, "E32.9.0.2", {"start": v(-47.72, 3.11) * mm, "end": v(-50.6, 3.11) * mm});
            skLineSegment(sketch, "E32.12.0.2", {"start": v(-46.28, 5.61) * mm, "end": v(-47.72, 3.11) * mm});
            skLineSegment(sketch, "E32.15.0.2", {"start": v(-47.72, 8.11) * mm, "end": v(-46.28, 5.61) * mm});
            skLineSegment(sketch, "E32.18.0.2", {"start": v(-45.2, 6.24) * mm, "end": v(-46.64, 8.74) * mm});
            skLineSegment(sketch, "E32.21.0.2", {"start": v(-46.64, 8.74) * mm, "end": v(-45.2, 11.24) * mm});
            skLineSegment(sketch, "E32.24.0.2", {"start": v(-45.2, 11.24) * mm, "end": v(-42.3, 11.24) * mm});
            skLineSegment(sketch, "E32.27.0.2", {"start": v(-42.3, 11.24) * mm, "end": v(-40.86, 8.74) * mm});
            skLineSegment(sketch, "E32.30.0.2", {"start": v(-40.86, 8.74) * mm, "end": v(-42.3, 6.24) * mm});
            skLineSegment(sketch, "E32.33.0.2", {"start": v(-42.3, 6.24) * mm, "end": v(-45.2, 6.24) * mm});
            skLineSegment(sketch, "E32.0.1.2", {"start": v(-39.61, 8.11) * mm, "end": v(-36.73, 8.11) * mm});
            skLineSegment(sketch, "E32.3.1.2", {"start": v(-41.06, 5.61) * mm, "end": v(-39.61, 8.11) * mm});
            skLineSegment(sketch, "E32.6.1.2", {"start": v(-39.61, 3.11) * mm, "end": v(-41.06, 5.61) * mm});
            skLineSegment(sketch, "E32.9.1.2", {"start": v(-36.73, 3.11) * mm, "end": v(-39.61, 3.11) * mm});
            skLineSegment(sketch, "E32.12.1.2", {"start": v(-35.28, 5.61) * mm, "end": v(-36.73, 3.11) * mm});
            skLineSegment(sketch, "E32.15.1.2", {"start": v(-36.73, 8.11) * mm, "end": v(-35.28, 5.61) * mm});
            skLineSegment(sketch, "E32.18.1.2", {"start": v(-34.2, 6.24) * mm, "end": v(-35.65, 8.74) * mm});
            skLineSegment(sketch, "E32.21.1.2", {"start": v(-35.65, 8.74) * mm, "end": v(-34.2, 11.24) * mm});
            skLineSegment(sketch, "E32.24.1.2", {"start": v(-34.2, 11.24) * mm, "end": v(-31.32, 11.24) * mm});
            skLineSegment(sketch, "E32.27.1.2", {"start": v(-31.32, 11.24) * mm, "end": v(-29.87, 8.74) * mm});
            skLineSegment(sketch, "E32.30.1.2", {"start": v(-29.87, 8.74) * mm, "end": v(-31.32, 6.24) * mm});
            skLineSegment(sketch, "E32.33.1.2", {"start": v(-31.32, 6.24) * mm, "end": v(-34.2, 6.24) * mm});
            skLineSegment(sketch, "E32.0.2.2", {"start": v(-28.62, 8.11) * mm, "end": v(-25.73, 8.11) * mm});
            skLineSegment(sketch, "E32.3.2.2", {"start": v(-30.07, 5.61) * mm, "end": v(-28.62, 8.11) * mm});
            skLineSegment(sketch, "E32.6.2.2", {"start": v(-28.62, 3.11) * mm, "end": v(-30.07, 5.61) * mm});
            skLineSegment(sketch, "E32.9.2.2", {"start": v(-25.73, 3.11) * mm, "end": v(-28.62, 3.11) * mm});
            skLineSegment(sketch, "E32.12.2.2", {"start": v(-24.3, 5.61) * mm, "end": v(-25.73, 3.11) * mm});
            skLineSegment(sketch, "E32.15.2.2", {"start": v(-25.73, 8.11) * mm, "end": v(-24.3, 5.61) * mm});
            skLineSegment(sketch, "E32.18.2.2", {"start": v(-23.2, 6.24) * mm, "end": v(-24.65, 8.74) * mm});
            skLineSegment(sketch, "E32.21.2.2", {"start": v(-24.65, 8.74) * mm, "end": v(-23.2, 11.24) * mm});
            skLineSegment(sketch, "E32.24.2.2", {"start": v(-23.2, 11.24) * mm, "end": v(-20.32, 11.24) * mm});
            skLineSegment(sketch, "E32.27.2.2", {"start": v(-20.32, 11.24) * mm, "end": v(-18.88, 8.74) * mm});
            skLineSegment(sketch, "E32.30.2.2", {"start": v(-18.88, 8.74) * mm, "end": v(-20.32, 6.24) * mm});
            skLineSegment(sketch, "E32.33.2.2", {"start": v(-20.32, 6.24) * mm, "end": v(-23.2, 6.24) * mm});
            skLineSegment(sketch, "E33.0.0.3", {"start": v(-50.6, 1.86) * mm, "end": v(-47.72, 1.86) * mm});
            skLineSegment(sketch, "E33.3.0.3", {"start": v(-52.05, -0.64) * mm, "end": v(-50.6, 1.86) * mm});
            skLineSegment(sketch, "E33.6.0.3", {"start": v(-50.6, -3.14) * mm, "end": v(-52.05, -0.64) * mm});
            skLineSegment(sketch, "E33.9.0.3", {"start": v(-47.72, -3.14) * mm, "end": v(-50.6, -3.14) * mm});
            skLineSegment(sketch, "E33.12.0.3", {"start": v(-46.28, -0.64) * mm, "end": v(-47.72, -3.14) * mm});
            skLineSegment(sketch, "E33.15.0.3", {"start": v(-47.72, 1.86) * mm, "end": v(-46.28, -0.64) * mm});
            skLineSegment(sketch, "E33.18.0.3", {"start": v(-45.2, -0.01) * mm, "end": v(-46.64, 2.49) * mm});
            skLineSegment(sketch, "E33.21.0.3", {"start": v(-46.64, 2.49) * mm, "end": v(-45.2, 4.99) * mm});
            skLineSegment(sketch, "E33.24.0.3", {"start": v(-45.2, 4.99) * mm, "end": v(-42.3, 4.99) * mm});
            skLineSegment(sketch, "E33.27.0.3", {"start": v(-42.3, 4.99) * mm, "end": v(-40.86, 2.49) * mm});
            skLineSegment(sketch, "E33.30.0.3", {"start": v(-40.86, 2.49) * mm, "end": v(-42.3, -0.01) * mm});
            skLineSegment(sketch, "E33.33.0.3", {"start": v(-42.3, -0.01) * mm, "end": v(-45.2, -0.01) * mm});
            skLineSegment(sketch, "E33.0.1.3", {"start": v(-39.61, 1.86) * mm, "end": v(-36.73, 1.86) * mm});
            skLineSegment(sketch, "E33.3.1.3", {"start": v(-41.06, -0.64) * mm, "end": v(-39.61, 1.86) * mm});
            skLineSegment(sketch, "E33.6.1.3", {"start": v(-39.61, -3.14) * mm, "end": v(-41.06, -0.64) * mm});
            skLineSegment(sketch, "E33.9.1.3", {"start": v(-36.73, -3.14) * mm, "end": v(-39.61, -3.14) * mm});
            skLineSegment(sketch, "E33.12.1.3", {"start": v(-35.28, -0.64) * mm, "end": v(-36.73, -3.14) * mm});
            skLineSegment(sketch, "E33.15.1.3", {"start": v(-36.73, 1.86) * mm, "end": v(-35.28, -0.64) * mm});
            skLineSegment(sketch, "E33.18.1.3", {"start": v(-34.2, -0.01) * mm, "end": v(-35.65, 2.49) * mm});
            skLineSegment(sketch, "E33.21.1.3", {"start": v(-35.65, 2.49) * mm, "end": v(-34.2, 4.99) * mm});
            skLineSegment(sketch, "E33.24.1.3", {"start": v(-34.2, 4.99) * mm, "end": v(-31.32, 4.99) * mm});
            skLineSegment(sketch, "E33.27.1.3", {"start": v(-31.32, 4.99) * mm, "end": v(-29.87, 2.49) * mm});
            skLineSegment(sketch, "E33.30.1.3", {"start": v(-29.87, 2.49) * mm, "end": v(-31.32, -0.01) * mm});
            skLineSegment(sketch, "E33.33.1.3", {"start": v(-31.32, -0.01) * mm, "end": v(-34.2, -0.01) * mm});
            skLineSegment(sketch, "E33.0.2.3", {"start": v(-28.62, 1.86) * mm, "end": v(-25.73, 1.86) * mm});
            skLineSegment(sketch, "E33.3.2.3", {"start": v(-30.07, -0.64) * mm, "end": v(-28.62, 1.86) * mm});
            skLineSegment(sketch, "E33.6.2.3", {"start": v(-28.62, -3.14) * mm, "end": v(-30.07, -0.64) * mm});
            skLineSegment(sketch, "E33.9.2.3", {"start": v(-25.73, -3.14) * mm, "end": v(-28.62, -3.14) * mm});
            skLineSegment(sketch, "E33.12.2.3", {"start": v(-24.3, -0.64) * mm, "end": v(-25.73, -3.14) * mm});
            skLineSegment(sketch, "E33.15.2.3", {"start": v(-25.73, 1.86) * mm, "end": v(-24.3, -0.64) * mm});
            skLineSegment(sketch, "E33.18.2.3", {"start": v(-23.2, -0.01) * mm, "end": v(-24.65, 2.49) * mm});
            skLineSegment(sketch, "E33.21.2.3", {"start": v(-24.65, 2.49) * mm, "end": v(-23.2, 4.99) * mm});
            skLineSegment(sketch, "E33.24.2.3", {"start": v(-23.2, 4.99) * mm, "end": v(-20.32, 4.99) * mm});
            skLineSegment(sketch, "E33.27.2.3", {"start": v(-20.32, 4.99) * mm, "end": v(-18.88, 2.49) * mm});
            skLineSegment(sketch, "E33.30.2.3", {"start": v(-18.88, 2.49) * mm, "end": v(-20.32, -0.01) * mm});
            skLineSegment(sketch, "E33.33.2.3", {"start": v(-20.32, -0.01) * mm, "end": v(-23.2, -0.01) * mm});
            skLineSegment(sketch, "E34.0.3.0", {"start": v(-17.63, 20.61) * mm, "end": v(-14.74, 20.61) * mm});
            skLineSegment(sketch, "E34.3.3.0", {"start": v(-19.07, 18.11) * mm, "end": v(-17.63, 20.61) * mm});
            skLineSegment(sketch, "E34.6.3.0", {"start": v(-17.63, 15.61) * mm, "end": v(-19.07, 18.11) * mm});
            skLineSegment(sketch, "E34.9.3.0", {"start": v(-14.74, 15.61) * mm, "end": v(-17.63, 15.61) * mm});
            skLineSegment(sketch, "E34.12.3.0", {"start": v(-13.3, 18.11) * mm, "end": v(-14.74, 15.61) * mm});
            skLineSegment(sketch, "E34.15.3.0", {"start": v(-14.74, 20.61) * mm, "end": v(-13.3, 18.11) * mm});
            skLineSegment(sketch, "E34.18.3.0", {"start": v(-12.22, 18.74) * mm, "end": v(-13.66, 21.24) * mm});
            skLineSegment(sketch, "E34.21.3.0", {"start": v(-13.66, 21.24) * mm, "end": v(-12.22, 23.74) * mm});
            skLineSegment(sketch, "E34.24.3.0", {"start": v(-12.22, 23.74) * mm, "end": v(-9.33, 23.74) * mm});
            skLineSegment(sketch, "E34.27.3.0", {"start": v(-9.33, 23.74) * mm, "end": v(-7.89, 21.24) * mm});
            skLineSegment(sketch, "E34.30.3.0", {"start": v(-7.89, 21.24) * mm, "end": v(-9.33, 18.74) * mm});
            skLineSegment(sketch, "E34.33.3.0", {"start": v(-9.33, 18.74) * mm, "end": v(-12.22, 18.74) * mm});
            skLineSegment(sketch, "E34.0.3.1", {"start": v(-17.63, 14.36) * mm, "end": v(-14.74, 14.36) * mm});
            skLineSegment(sketch, "E34.3.3.1", {"start": v(-19.07, 11.86) * mm, "end": v(-17.63, 14.36) * mm});
            skLineSegment(sketch, "E34.6.3.1", {"start": v(-17.63, 9.36) * mm, "end": v(-19.07, 11.86) * mm});
            skLineSegment(sketch, "E34.9.3.1", {"start": v(-14.74, 9.36) * mm, "end": v(-17.63, 9.36) * mm});
            skLineSegment(sketch, "E34.12.3.1", {"start": v(-13.3, 11.86) * mm, "end": v(-14.74, 9.36) * mm});
            skLineSegment(sketch, "E34.15.3.1", {"start": v(-14.74, 14.36) * mm, "end": v(-13.3, 11.86) * mm});
            skLineSegment(sketch, "E34.18.3.1", {"start": v(-12.22, 12.49) * mm, "end": v(-13.66, 14.99) * mm});
            skLineSegment(sketch, "E34.21.3.1", {"start": v(-13.66, 14.99) * mm, "end": v(-12.22, 17.49) * mm});
            skLineSegment(sketch, "E34.24.3.1", {"start": v(-12.22, 17.49) * mm, "end": v(-9.33, 17.49) * mm});
            skLineSegment(sketch, "E34.27.3.1", {"start": v(-9.33, 17.49) * mm, "end": v(-7.89, 14.99) * mm});
            skLineSegment(sketch, "E34.30.3.1", {"start": v(-7.89, 14.99) * mm, "end": v(-9.33, 12.49) * mm});
            skLineSegment(sketch, "E34.33.3.1", {"start": v(-9.33, 12.49) * mm, "end": v(-12.22, 12.49) * mm});
            skLineSegment(sketch, "E34.0.3.2", {"start": v(-17.63, 8.11) * mm, "end": v(-14.74, 8.11) * mm});
            skLineSegment(sketch, "E34.3.3.2", {"start": v(-19.07, 5.61) * mm, "end": v(-17.63, 8.11) * mm});
            skLineSegment(sketch, "E34.6.3.2", {"start": v(-17.63, 3.11) * mm, "end": v(-19.07, 5.61) * mm});
            skLineSegment(sketch, "E34.9.3.2", {"start": v(-14.74, 3.11) * mm, "end": v(-17.63, 3.11) * mm});
            skLineSegment(sketch, "E34.12.3.2", {"start": v(-13.3, 5.61) * mm, "end": v(-14.74, 3.11) * mm});
            skLineSegment(sketch, "E34.15.3.2", {"start": v(-14.74, 8.11) * mm, "end": v(-13.3, 5.61) * mm});
            skLineSegment(sketch, "E34.18.3.2", {"start": v(-12.22, 6.24) * mm, "end": v(-13.66, 8.74) * mm});
            skLineSegment(sketch, "E34.21.3.2", {"start": v(-13.66, 8.74) * mm, "end": v(-12.22, 11.24) * mm});
            skLineSegment(sketch, "E34.24.3.2", {"start": v(-12.22, 11.24) * mm, "end": v(-9.33, 11.24) * mm});
            skLineSegment(sketch, "E34.27.3.2", {"start": v(-9.33, 11.24) * mm, "end": v(-7.89, 8.74) * mm});
            skLineSegment(sketch, "E34.30.3.2", {"start": v(-7.89, 8.74) * mm, "end": v(-9.33, 6.24) * mm});
            skLineSegment(sketch, "E34.33.3.2", {"start": v(-9.33, 6.24) * mm, "end": v(-12.22, 6.24) * mm});
            skLineSegment(sketch, "E34.0.3.3", {"start": v(-17.63, 1.86) * mm, "end": v(-14.74, 1.86) * mm});
            skLineSegment(sketch, "E34.3.3.3", {"start": v(-19.07, -0.64) * mm, "end": v(-17.63, 1.86) * mm});
            skLineSegment(sketch, "E34.6.3.3", {"start": v(-17.63, -3.14) * mm, "end": v(-19.07, -0.64) * mm});
            skLineSegment(sketch, "E34.9.3.3", {"start": v(-14.74, -3.14) * mm, "end": v(-17.63, -3.14) * mm});
            skLineSegment(sketch, "E34.12.3.3", {"start": v(-13.3, -0.64) * mm, "end": v(-14.74, -3.14) * mm});
            skLineSegment(sketch, "E34.15.3.3", {"start": v(-14.74, 1.86) * mm, "end": v(-13.3, -0.64) * mm});
            skLineSegment(sketch, "E34.18.3.3", {"start": v(-12.22, -0.01) * mm, "end": v(-13.66, 2.49) * mm});
            skLineSegment(sketch, "E34.21.3.3", {"start": v(-13.66, 2.49) * mm, "end": v(-12.22, 4.99) * mm});
            skLineSegment(sketch, "E34.24.3.3", {"start": v(-12.22, 4.99) * mm, "end": v(-9.33, 4.99) * mm});
            skLineSegment(sketch, "E34.27.3.3", {"start": v(-9.33, 4.99) * mm, "end": v(-7.89, 2.49) * mm});
            skLineSegment(sketch, "E34.30.3.3", {"start": v(-7.89, 2.49) * mm, "end": v(-9.33, -0.01) * mm});
            skLineSegment(sketch, "E34.33.3.3", {"start": v(-9.33, -0.01) * mm, "end": v(-12.22, -0.01) * mm});
            skLineSegment(sketch, "E34.0.4.0", {"start": v(-6.64, 20.61) * mm, "end": v(-3.75, 20.61) * mm});
            skLineSegment(sketch, "E34.3.4.0", {"start": v(-8.08, 18.11) * mm, "end": v(-6.64, 20.61) * mm});
            skLineSegment(sketch, "E34.6.4.0", {"start": v(-6.64, 15.61) * mm, "end": v(-8.08, 18.11) * mm});
            skLineSegment(sketch, "E34.9.4.0", {"start": v(-3.75, 15.61) * mm, "end": v(-6.64, 15.61) * mm});
            skLineSegment(sketch, "E34.12.4.0", {"start": v(-2.3, 18.11) * mm, "end": v(-3.75, 15.61) * mm});
            skLineSegment(sketch, "E34.15.4.0", {"start": v(-3.75, 20.61) * mm, "end": v(-2.3, 18.11) * mm});
            skLineSegment(sketch, "E34.18.4.0", {"start": v(-1.22, 18.74) * mm, "end": v(-2.67, 21.24) * mm});
            skLineSegment(sketch, "E34.21.4.0", {"start": v(-2.67, 21.24) * mm, "end": v(-1.22, 23.74) * mm});
            skLineSegment(sketch, "E34.24.4.0", {"start": v(-1.22, 23.74) * mm, "end": v(1.66, 23.74) * mm});
            skLineSegment(sketch, "E34.27.4.0", {"start": v(1.66, 23.74) * mm, "end": v(3.1, 21.24) * mm});
            skLineSegment(sketch, "E34.30.4.0", {"start": v(3.1, 21.24) * mm, "end": v(1.66, 18.74) * mm});
            skLineSegment(sketch, "E34.33.4.0", {"start": v(1.66, 18.74) * mm, "end": v(-1.22, 18.74) * mm});
            skLineSegment(sketch, "E34.0.4.1", {"start": v(-6.64, 14.36) * mm, "end": v(-3.75, 14.36) * mm});
            skLineSegment(sketch, "E34.3.4.1", {"start": v(-8.08, 11.86) * mm, "end": v(-6.64, 14.36) * mm});
            skLineSegment(sketch, "E34.6.4.1", {"start": v(-6.64, 9.36) * mm, "end": v(-8.08, 11.86) * mm});
            skLineSegment(sketch, "E34.9.4.1", {"start": v(-3.75, 9.36) * mm, "end": v(-6.64, 9.36) * mm});
            skLineSegment(sketch, "E34.12.4.1", {"start": v(-2.3, 11.86) * mm, "end": v(-3.75, 9.36) * mm});
            skLineSegment(sketch, "E34.15.4.1", {"start": v(-3.75, 14.36) * mm, "end": v(-2.3, 11.86) * mm});
            skLineSegment(sketch, "E34.18.4.1", {"start": v(-1.22, 12.49) * mm, "end": v(-2.67, 14.99) * mm});
            skLineSegment(sketch, "E34.21.4.1", {"start": v(-2.67, 14.99) * mm, "end": v(-1.22, 17.49) * mm});
            skLineSegment(sketch, "E34.24.4.1", {"start": v(-1.22, 17.49) * mm, "end": v(1.66, 17.49) * mm});
            skLineSegment(sketch, "E34.27.4.1", {"start": v(1.66, 17.49) * mm, "end": v(3.1, 14.99) * mm});
            skLineSegment(sketch, "E34.30.4.1", {"start": v(3.1, 14.99) * mm, "end": v(1.66, 12.49) * mm});
            skLineSegment(sketch, "E34.33.4.1", {"start": v(1.66, 12.49) * mm, "end": v(-1.22, 12.49) * mm});
            skLineSegment(sketch, "E34.0.4.2", {"start": v(-6.64, 8.11) * mm, "end": v(-3.75, 8.11) * mm});
            skLineSegment(sketch, "E34.3.4.2", {"start": v(-8.08, 5.61) * mm, "end": v(-6.64, 8.11) * mm});
            skLineSegment(sketch, "E34.6.4.2", {"start": v(-6.64, 3.11) * mm, "end": v(-8.08, 5.61) * mm});
            skLineSegment(sketch, "E34.9.4.2", {"start": v(-3.75, 3.11) * mm, "end": v(-6.64, 3.11) * mm});
            skLineSegment(sketch, "E34.12.4.2", {"start": v(-2.3, 5.61) * mm, "end": v(-3.75, 3.11) * mm});
            skLineSegment(sketch, "E34.15.4.2", {"start": v(-3.75, 8.11) * mm, "end": v(-2.3, 5.61) * mm});
            skLineSegment(sketch, "E34.18.4.2", {"start": v(-1.22, 6.24) * mm, "end": v(-2.67, 8.74) * mm});
            skLineSegment(sketch, "E34.21.4.2", {"start": v(-2.67, 8.74) * mm, "end": v(-1.22, 11.24) * mm});
            skLineSegment(sketch, "E34.24.4.2", {"start": v(-1.22, 11.24) * mm, "end": v(1.66, 11.24) * mm});
            skLineSegment(sketch, "E34.27.4.2", {"start": v(1.66, 11.24) * mm, "end": v(3.1, 8.74) * mm});
            skLineSegment(sketch, "E34.30.4.2", {"start": v(3.1, 8.74) * mm, "end": v(1.66, 6.24) * mm});
            skLineSegment(sketch, "E34.33.4.2", {"start": v(1.66, 6.24) * mm, "end": v(-1.22, 6.24) * mm});
            skLineSegment(sketch, "E34.0.4.3", {"start": v(-6.64, 1.86) * mm, "end": v(-3.75, 1.86) * mm});
            skLineSegment(sketch, "E34.3.4.3", {"start": v(-8.08, -0.64) * mm, "end": v(-6.64, 1.86) * mm});
            skLineSegment(sketch, "E34.6.4.3", {"start": v(-6.64, -3.14) * mm, "end": v(-8.08, -0.64) * mm});
            skLineSegment(sketch, "E34.9.4.3", {"start": v(-3.75, -3.14) * mm, "end": v(-6.64, -3.14) * mm});
            skLineSegment(sketch, "E34.12.4.3", {"start": v(-2.3, -0.64) * mm, "end": v(-3.75, -3.14) * mm});
            skLineSegment(sketch, "E34.15.4.3", {"start": v(-3.75, 1.86) * mm, "end": v(-2.3, -0.64) * mm});
            skLineSegment(sketch, "E34.18.4.3", {"start": v(-1.22, -0.01) * mm, "end": v(-2.67, 2.49) * mm});
            skLineSegment(sketch, "E34.21.4.3", {"start": v(-2.67, 2.49) * mm, "end": v(-1.22, 4.99) * mm});
            skLineSegment(sketch, "E34.24.4.3", {"start": v(-1.22, 4.99) * mm, "end": v(1.66, 4.99) * mm});
            skLineSegment(sketch, "E34.27.4.3", {"start": v(1.66, 4.99) * mm, "end": v(3.1, 2.49) * mm});
            skLineSegment(sketch, "E34.30.4.3", {"start": v(3.1, 2.49) * mm, "end": v(1.66, -0.01) * mm});
            skLineSegment(sketch, "E34.33.4.3", {"start": v(1.66, -0.01) * mm, "end": v(-1.22, -0.01) * mm});
            skLineSegment(sketch, "E34.0.5.0", {"start": v(4.36, 20.61) * mm, "end": v(7.24, 20.61) * mm});
            skLineSegment(sketch, "E34.3.5.0", {"start": v(2.91, 18.11) * mm, "end": v(4.36, 20.61) * mm});
            skLineSegment(sketch, "E34.6.5.0", {"start": v(4.36, 15.61) * mm, "end": v(2.91, 18.11) * mm});
            skLineSegment(sketch, "E34.9.5.0", {"start": v(7.24, 15.61) * mm, "end": v(4.36, 15.61) * mm});
            skLineSegment(sketch, "E34.12.5.0", {"start": v(8.69, 18.11) * mm, "end": v(7.24, 15.61) * mm});
            skLineSegment(sketch, "E34.15.5.0", {"start": v(7.24, 20.61) * mm, "end": v(8.69, 18.11) * mm});
            skLineSegment(sketch, "E34.18.5.0", {"start": v(9.77, 18.74) * mm, "end": v(8.33, 21.24) * mm});
            skLineSegment(sketch, "E34.21.5.0", {"start": v(8.33, 21.24) * mm, "end": v(9.77, 23.74) * mm});
            skLineSegment(sketch, "E34.24.5.0", {"start": v(9.77, 23.74) * mm, "end": v(12.66, 23.74) * mm});
            skLineSegment(sketch, "E34.27.5.0", {"start": v(12.66, 23.74) * mm, "end": v(14.1, 21.24) * mm});
            skLineSegment(sketch, "E34.30.5.0", {"start": v(14.1, 21.24) * mm, "end": v(12.66, 18.74) * mm});
            skLineSegment(sketch, "E34.33.5.0", {"start": v(12.66, 18.74) * mm, "end": v(9.77, 18.74) * mm});
            skLineSegment(sketch, "E34.0.5.1", {"start": v(4.36, 14.36) * mm, "end": v(7.24, 14.36) * mm});
            skLineSegment(sketch, "E34.3.5.1", {"start": v(2.91, 11.86) * mm, "end": v(4.36, 14.36) * mm});
            skLineSegment(sketch, "E34.6.5.1", {"start": v(4.36, 9.36) * mm, "end": v(2.91, 11.86) * mm});
            skLineSegment(sketch, "E34.9.5.1", {"start": v(7.24, 9.36) * mm, "end": v(4.36, 9.36) * mm});
            skLineSegment(sketch, "E34.12.5.1", {"start": v(8.69, 11.86) * mm, "end": v(7.24, 9.36) * mm});
            skLineSegment(sketch, "E34.15.5.1", {"start": v(7.24, 14.36) * mm, "end": v(8.69, 11.86) * mm});
            skLineSegment(sketch, "E34.18.5.1", {"start": v(9.77, 12.49) * mm, "end": v(8.33, 14.99) * mm});
            skLineSegment(sketch, "E34.21.5.1", {"start": v(8.33, 14.99) * mm, "end": v(9.77, 17.49) * mm});
            skLineSegment(sketch, "E34.24.5.1", {"start": v(9.77, 17.49) * mm, "end": v(12.66, 17.49) * mm});
            skLineSegment(sketch, "E34.27.5.1", {"start": v(12.66, 17.49) * mm, "end": v(14.1, 14.99) * mm});
            skLineSegment(sketch, "E34.30.5.1", {"start": v(14.1, 14.99) * mm, "end": v(12.66, 12.49) * mm});
            skLineSegment(sketch, "E34.33.5.1", {"start": v(12.66, 12.49) * mm, "end": v(9.77, 12.49) * mm});
            skLineSegment(sketch, "E34.0.5.2", {"start": v(4.36, 8.11) * mm, "end": v(7.24, 8.11) * mm});
            skLineSegment(sketch, "E34.3.5.2", {"start": v(2.91, 5.61) * mm, "end": v(4.36, 8.11) * mm});
            skLineSegment(sketch, "E34.6.5.2", {"start": v(4.36, 3.11) * mm, "end": v(2.91, 5.61) * mm});
            skLineSegment(sketch, "E34.9.5.2", {"start": v(7.24, 3.11) * mm, "end": v(4.36, 3.11) * mm});
            skLineSegment(sketch, "E34.12.5.2", {"start": v(8.69, 5.61) * mm, "end": v(7.24, 3.11) * mm});
            skLineSegment(sketch, "E34.15.5.2", {"start": v(7.24, 8.11) * mm, "end": v(8.69, 5.61) * mm});
            skLineSegment(sketch, "E34.18.5.2", {"start": v(9.77, 6.24) * mm, "end": v(8.33, 8.74) * mm});
            skLineSegment(sketch, "E34.21.5.2", {"start": v(8.33, 8.74) * mm, "end": v(9.77, 11.24) * mm});
            skLineSegment(sketch, "E34.24.5.2", {"start": v(9.77, 11.24) * mm, "end": v(12.66, 11.24) * mm});
            skLineSegment(sketch, "E34.27.5.2", {"start": v(12.66, 11.24) * mm, "end": v(14.1, 8.74) * mm});
            skLineSegment(sketch, "E34.30.5.2", {"start": v(14.1, 8.74) * mm, "end": v(12.66, 6.24) * mm});
            skLineSegment(sketch, "E34.33.5.2", {"start": v(12.66, 6.24) * mm, "end": v(9.77, 6.24) * mm});
            skLineSegment(sketch, "E34.0.5.3", {"start": v(4.36, 1.86) * mm, "end": v(7.24, 1.86) * mm});
            skLineSegment(sketch, "E34.3.5.3", {"start": v(2.91, -0.64) * mm, "end": v(4.36, 1.86) * mm});
            skLineSegment(sketch, "E34.6.5.3", {"start": v(4.36, -3.14) * mm, "end": v(2.91, -0.64) * mm});
            skLineSegment(sketch, "E34.9.5.3", {"start": v(7.24, -3.14) * mm, "end": v(4.36, -3.14) * mm});
            skLineSegment(sketch, "E34.12.5.3", {"start": v(8.69, -0.64) * mm, "end": v(7.24, -3.14) * mm});
            skLineSegment(sketch, "E34.15.5.3", {"start": v(7.24, 1.86) * mm, "end": v(8.69, -0.64) * mm});
            skLineSegment(sketch, "E34.18.5.3", {"start": v(9.77, -0.01) * mm, "end": v(8.33, 2.49) * mm});
            skLineSegment(sketch, "E34.21.5.3", {"start": v(8.33, 2.49) * mm, "end": v(9.77, 4.99) * mm});
            skLineSegment(sketch, "E34.24.5.3", {"start": v(9.77, 4.99) * mm, "end": v(12.66, 4.99) * mm});
            skLineSegment(sketch, "E34.27.5.3", {"start": v(12.66, 4.99) * mm, "end": v(14.1, 2.49) * mm});
            skLineSegment(sketch, "E34.30.5.3", {"start": v(14.1, 2.49) * mm, "end": v(12.66, -0.01) * mm});
            skLineSegment(sketch, "E34.33.5.3", {"start": v(12.66, -0.01) * mm, "end": v(9.77, -0.01) * mm});
            skLineSegment(sketch, "E34.0.6.0", {"start": v(15.35, 20.61) * mm, "end": v(18.24, 20.61) * mm});
            skLineSegment(sketch, "E34.3.6.0", {"start": v(13.9, 18.11) * mm, "end": v(15.35, 20.61) * mm});
            skLineSegment(sketch, "E34.6.6.0", {"start": v(15.35, 15.61) * mm, "end": v(13.9, 18.11) * mm});
            skLineSegment(sketch, "E34.9.6.0", {"start": v(18.24, 15.61) * mm, "end": v(15.35, 15.61) * mm});
            skLineSegment(sketch, "E34.12.6.0", {"start": v(19.68, 18.11) * mm, "end": v(18.24, 15.61) * mm});
            skLineSegment(sketch, "E34.15.6.0", {"start": v(18.24, 20.61) * mm, "end": v(19.68, 18.11) * mm});
            skLineSegment(sketch, "E34.18.6.0", {"start": v(20.76, 18.74) * mm, "end": v(19.32, 21.24) * mm});
            skLineSegment(sketch, "E34.21.6.0", {"start": v(19.32, 21.24) * mm, "end": v(20.76, 23.74) * mm});
            skLineSegment(sketch, "E34.24.6.0", {"start": v(20.76, 23.74) * mm, "end": v(23.65, 23.74) * mm});
            skLineSegment(sketch, "E34.27.6.0", {"start": v(23.65, 23.74) * mm, "end": v(25.1, 21.24) * mm});
            skLineSegment(sketch, "E34.30.6.0", {"start": v(25.1, 21.24) * mm, "end": v(23.65, 18.74) * mm});
            skLineSegment(sketch, "E34.33.6.0", {"start": v(23.65, 18.74) * mm, "end": v(20.76, 18.74) * mm});
            skLineSegment(sketch, "E34.0.6.1", {"start": v(15.35, 14.36) * mm, "end": v(18.24, 14.36) * mm});
            skLineSegment(sketch, "E34.3.6.1", {"start": v(13.9, 11.86) * mm, "end": v(15.35, 14.36) * mm});
            skLineSegment(sketch, "E34.6.6.1", {"start": v(15.35, 9.36) * mm, "end": v(13.9, 11.86) * mm});
            skLineSegment(sketch, "E34.9.6.1", {"start": v(18.24, 9.36) * mm, "end": v(15.35, 9.36) * mm});
            skLineSegment(sketch, "E34.12.6.1", {"start": v(19.68, 11.86) * mm, "end": v(18.24, 9.36) * mm});
            skLineSegment(sketch, "E34.15.6.1", {"start": v(18.24, 14.36) * mm, "end": v(19.68, 11.86) * mm});
            skLineSegment(sketch, "E34.18.6.1", {"start": v(20.76, 12.49) * mm, "end": v(19.32, 14.99) * mm});
            skLineSegment(sketch, "E34.21.6.1", {"start": v(19.32, 14.99) * mm, "end": v(20.76, 17.49) * mm});
            skLineSegment(sketch, "E34.24.6.1", {"start": v(20.76, 17.49) * mm, "end": v(23.65, 17.49) * mm});
            skLineSegment(sketch, "E34.27.6.1", {"start": v(23.65, 17.49) * mm, "end": v(25.1, 14.99) * mm});
            skLineSegment(sketch, "E34.30.6.1", {"start": v(25.1, 14.99) * mm, "end": v(23.65, 12.49) * mm});
            skLineSegment(sketch, "E34.33.6.1", {"start": v(23.65, 12.49) * mm, "end": v(20.76, 12.49) * mm});
            skLineSegment(sketch, "E34.0.6.2", {"start": v(15.35, 8.11) * mm, "end": v(18.24, 8.11) * mm});
            skLineSegment(sketch, "E34.3.6.2", {"start": v(13.9, 5.61) * mm, "end": v(15.35, 8.11) * mm});
            skLineSegment(sketch, "E34.6.6.2", {"start": v(15.35, 3.11) * mm, "end": v(13.9, 5.61) * mm});
            skLineSegment(sketch, "E34.9.6.2", {"start": v(18.24, 3.11) * mm, "end": v(15.35, 3.11) * mm});
            skLineSegment(sketch, "E34.12.6.2", {"start": v(19.68, 5.61) * mm, "end": v(18.24, 3.11) * mm});
            skLineSegment(sketch, "E34.15.6.2", {"start": v(18.24, 8.11) * mm, "end": v(19.68, 5.61) * mm});
            skLineSegment(sketch, "E34.18.6.2", {"start": v(20.76, 6.24) * mm, "end": v(19.32, 8.74) * mm});
            skLineSegment(sketch, "E34.21.6.2", {"start": v(19.32, 8.74) * mm, "end": v(20.76, 11.24) * mm});
            skLineSegment(sketch, "E34.24.6.2", {"start": v(20.76, 11.24) * mm, "end": v(23.65, 11.24) * mm});
            skLineSegment(sketch, "E34.27.6.2", {"start": v(23.65, 11.24) * mm, "end": v(25.1, 8.74) * mm});
            skLineSegment(sketch, "E34.30.6.2", {"start": v(25.1, 8.74) * mm, "end": v(23.65, 6.24) * mm});
            skLineSegment(sketch, "E34.33.6.2", {"start": v(23.65, 6.24) * mm, "end": v(20.76, 6.24) * mm});
            skLineSegment(sketch, "E34.0.6.3", {"start": v(15.35, 1.86) * mm, "end": v(18.24, 1.86) * mm});
            skLineSegment(sketch, "E34.3.6.3", {"start": v(13.9, -0.64) * mm, "end": v(15.35, 1.86) * mm});
            skLineSegment(sketch, "E34.6.6.3", {"start": v(15.35, -3.14) * mm, "end": v(13.9, -0.64) * mm});
            skLineSegment(sketch, "E34.9.6.3", {"start": v(18.24, -3.14) * mm, "end": v(15.35, -3.14) * mm});
            skLineSegment(sketch, "E34.12.6.3", {"start": v(19.68, -0.64) * mm, "end": v(18.24, -3.14) * mm});
            skLineSegment(sketch, "E34.15.6.3", {"start": v(18.24, 1.86) * mm, "end": v(19.68, -0.64) * mm});
            skLineSegment(sketch, "E34.18.6.3", {"start": v(20.76, -0.01) * mm, "end": v(19.32, 2.49) * mm});
            skLineSegment(sketch, "E34.21.6.3", {"start": v(19.32, 2.49) * mm, "end": v(20.76, 4.99) * mm});
            skLineSegment(sketch, "E34.24.6.3", {"start": v(20.76, 4.99) * mm, "end": v(23.65, 4.99) * mm});
            skLineSegment(sketch, "E34.27.6.3", {"start": v(23.65, 4.99) * mm, "end": v(25.1, 2.49) * mm});
            skLineSegment(sketch, "E34.30.6.3", {"start": v(25.1, 2.49) * mm, "end": v(23.65, -0.01) * mm});
            skLineSegment(sketch, "E34.33.6.3", {"start": v(23.65, -0.01) * mm, "end": v(20.76, -0.01) * mm});
            skLineSegment(sketch, "E34.0.7.0", {"start": v(26.34, 20.61) * mm, "end": v(29.23, 20.61) * mm});
            skLineSegment(sketch, "E34.3.7.0", {"start": v(24.9, 18.11) * mm, "end": v(26.34, 20.61) * mm});
            skLineSegment(sketch, "E34.6.7.0", {"start": v(26.34, 15.61) * mm, "end": v(24.9, 18.11) * mm});
            skLineSegment(sketch, "E34.9.7.0", {"start": v(29.23, 15.61) * mm, "end": v(26.34, 15.61) * mm});
            skLineSegment(sketch, "E34.12.7.0", {"start": v(30.67, 18.11) * mm, "end": v(29.23, 15.61) * mm});
            skLineSegment(sketch, "E34.15.7.0", {"start": v(29.23, 20.61) * mm, "end": v(30.67, 18.11) * mm});
            skLineSegment(sketch, "E34.18.7.0", {"start": v(31.76, 18.74) * mm, "end": v(30.31, 21.24) * mm});
            skLineSegment(sketch, "E34.21.7.0", {"start": v(30.31, 21.24) * mm, "end": v(31.76, 23.74) * mm});
            skLineSegment(sketch, "E34.24.7.0", {"start": v(31.76, 23.74) * mm, "end": v(34.64, 23.74) * mm});
            skLineSegment(sketch, "E34.27.7.0", {"start": v(34.64, 23.74) * mm, "end": v(36.09, 21.24) * mm});
            skLineSegment(sketch, "E34.30.7.0", {"start": v(36.09, 21.24) * mm, "end": v(34.64, 18.74) * mm});
            skLineSegment(sketch, "E34.33.7.0", {"start": v(34.64, 18.74) * mm, "end": v(31.76, 18.74) * mm});
            skLineSegment(sketch, "E34.0.7.1", {"start": v(26.34, 14.36) * mm, "end": v(29.23, 14.36) * mm});
            skLineSegment(sketch, "E34.3.7.1", {"start": v(24.9, 11.86) * mm, "end": v(26.34, 14.36) * mm});
            skLineSegment(sketch, "E34.6.7.1", {"start": v(26.34, 9.36) * mm, "end": v(24.9, 11.86) * mm});
            skLineSegment(sketch, "E34.9.7.1", {"start": v(29.23, 9.36) * mm, "end": v(26.34, 9.36) * mm});
            skLineSegment(sketch, "E34.12.7.1", {"start": v(30.67, 11.86) * mm, "end": v(29.23, 9.36) * mm});
            skLineSegment(sketch, "E34.15.7.1", {"start": v(29.23, 14.36) * mm, "end": v(30.67, 11.86) * mm});
            skLineSegment(sketch, "E34.18.7.1", {"start": v(31.76, 12.49) * mm, "end": v(30.31, 14.99) * mm});
            skLineSegment(sketch, "E34.21.7.1", {"start": v(30.31, 14.99) * mm, "end": v(31.76, 17.49) * mm});
            skLineSegment(sketch, "E34.24.7.1", {"start": v(31.76, 17.49) * mm, "end": v(34.64, 17.49) * mm});
            skLineSegment(sketch, "E34.27.7.1", {"start": v(34.64, 17.49) * mm, "end": v(36.09, 14.99) * mm});
            skLineSegment(sketch, "E34.30.7.1", {"start": v(36.09, 14.99) * mm, "end": v(34.64, 12.49) * mm});
            skLineSegment(sketch, "E34.33.7.1", {"start": v(34.64, 12.49) * mm, "end": v(31.76, 12.49) * mm});
            skLineSegment(sketch, "E34.0.7.2", {"start": v(26.34, 8.11) * mm, "end": v(29.23, 8.11) * mm});
            skLineSegment(sketch, "E34.3.7.2", {"start": v(24.9, 5.61) * mm, "end": v(26.34, 8.11) * mm});
            skLineSegment(sketch, "E34.6.7.2", {"start": v(26.34, 3.11) * mm, "end": v(24.9, 5.61) * mm});
            skLineSegment(sketch, "E34.9.7.2", {"start": v(29.23, 3.11) * mm, "end": v(26.34, 3.11) * mm});
            skLineSegment(sketch, "E34.12.7.2", {"start": v(30.67, 5.61) * mm, "end": v(29.23, 3.11) * mm});
            skLineSegment(sketch, "E34.15.7.2", {"start": v(29.23, 8.11) * mm, "end": v(30.67, 5.61) * mm});
            skLineSegment(sketch, "E34.18.7.2", {"start": v(31.76, 6.24) * mm, "end": v(30.31, 8.74) * mm});
            skLineSegment(sketch, "E34.21.7.2", {"start": v(30.31, 8.74) * mm, "end": v(31.76, 11.24) * mm});
            skLineSegment(sketch, "E34.24.7.2", {"start": v(31.76, 11.24) * mm, "end": v(34.64, 11.24) * mm});
            skLineSegment(sketch, "E34.27.7.2", {"start": v(34.64, 11.24) * mm, "end": v(36.09, 8.74) * mm});
            skLineSegment(sketch, "E34.30.7.2", {"start": v(36.09, 8.74) * mm, "end": v(34.64, 6.24) * mm});
            skLineSegment(sketch, "E34.33.7.2", {"start": v(34.64, 6.24) * mm, "end": v(31.76, 6.24) * mm});
            skLineSegment(sketch, "E34.0.7.3", {"start": v(26.34, 1.86) * mm, "end": v(29.23, 1.86) * mm});
            skLineSegment(sketch, "E34.3.7.3", {"start": v(24.9, -0.64) * mm, "end": v(26.34, 1.86) * mm});
            skLineSegment(sketch, "E34.6.7.3", {"start": v(26.34, -3.14) * mm, "end": v(24.9, -0.64) * mm});
            skLineSegment(sketch, "E34.9.7.3", {"start": v(29.23, -3.14) * mm, "end": v(26.34, -3.14) * mm});
            skLineSegment(sketch, "E34.12.7.3", {"start": v(30.67, -0.64) * mm, "end": v(29.23, -3.14) * mm});
            skLineSegment(sketch, "E34.15.7.3", {"start": v(29.23, 1.86) * mm, "end": v(30.67, -0.64) * mm});
            skLineSegment(sketch, "E34.18.7.3", {"start": v(31.76, -0.01) * mm, "end": v(30.31, 2.49) * mm});
            skLineSegment(sketch, "E34.21.7.3", {"start": v(30.31, 2.49) * mm, "end": v(31.76, 4.99) * mm});
            skLineSegment(sketch, "E34.24.7.3", {"start": v(31.76, 4.99) * mm, "end": v(34.64, 4.99) * mm});
            skLineSegment(sketch, "E34.27.7.3", {"start": v(34.64, 4.99) * mm, "end": v(36.09, 2.49) * mm});
            skLineSegment(sketch, "E34.30.7.3", {"start": v(36.09, 2.49) * mm, "end": v(34.64, -0.01) * mm});
            skLineSegment(sketch, "E34.33.7.3", {"start": v(34.64, -0.01) * mm, "end": v(31.76, -0.01) * mm});
            skLineSegment(sketch, "E34.0.8.0", {"start": v(37.34, 20.61) * mm, "end": v(40.22, 20.61) * mm});
            skLineSegment(sketch, "E34.3.8.0", {"start": v(35.9, 18.11) * mm, "end": v(37.34, 20.61) * mm});
            skLineSegment(sketch, "E34.6.8.0", {"start": v(37.34, 15.61) * mm, "end": v(35.9, 18.11) * mm});
            skLineSegment(sketch, "E34.9.8.0", {"start": v(40.22, 15.61) * mm, "end": v(37.34, 15.61) * mm});
            skLineSegment(sketch, "E34.12.8.0", {"start": v(41.67, 18.11) * mm, "end": v(40.22, 15.61) * mm});
            skLineSegment(sketch, "E34.15.8.0", {"start": v(40.22, 20.61) * mm, "end": v(41.67, 18.11) * mm});
            skLineSegment(sketch, "E34.18.8.0", {"start": v(42.75, 18.74) * mm, "end": v(41.3, 21.24) * mm});
            skLineSegment(sketch, "E34.21.8.0", {"start": v(41.3, 21.24) * mm, "end": v(42.75, 23.74) * mm});
            skLineSegment(sketch, "E34.24.8.0", {"start": v(42.75, 23.74) * mm, "end": v(45.64, 23.74) * mm});
            skLineSegment(sketch, "E34.27.8.0", {"start": v(45.64, 23.74) * mm, "end": v(47.08, 21.24) * mm});
            skLineSegment(sketch, "E34.30.8.0", {"start": v(47.08, 21.24) * mm, "end": v(45.64, 18.74) * mm});
            skLineSegment(sketch, "E34.33.8.0", {"start": v(45.64, 18.74) * mm, "end": v(42.75, 18.74) * mm});
            skLineSegment(sketch, "E34.0.8.1", {"start": v(37.34, 14.36) * mm, "end": v(40.22, 14.36) * mm});
            skLineSegment(sketch, "E34.3.8.1", {"start": v(35.9, 11.86) * mm, "end": v(37.34, 14.36) * mm});
            skLineSegment(sketch, "E34.6.8.1", {"start": v(37.34, 9.36) * mm, "end": v(35.9, 11.86) * mm});
            skLineSegment(sketch, "E34.9.8.1", {"start": v(40.22, 9.36) * mm, "end": v(37.34, 9.36) * mm});
            skLineSegment(sketch, "E34.12.8.1", {"start": v(41.67, 11.86) * mm, "end": v(40.22, 9.36) * mm});
            skLineSegment(sketch, "E34.15.8.1", {"start": v(40.22, 14.36) * mm, "end": v(41.67, 11.86) * mm});
            skLineSegment(sketch, "E34.18.8.1", {"start": v(42.75, 12.49) * mm, "end": v(41.3, 14.99) * mm});
            skLineSegment(sketch, "E34.21.8.1", {"start": v(41.3, 14.99) * mm, "end": v(42.75, 17.49) * mm});
            skLineSegment(sketch, "E34.24.8.1", {"start": v(42.75, 17.49) * mm, "end": v(45.64, 17.49) * mm});
            skLineSegment(sketch, "E34.27.8.1", {"start": v(45.64, 17.49) * mm, "end": v(47.08, 14.99) * mm});
            skLineSegment(sketch, "E34.30.8.1", {"start": v(47.08, 14.99) * mm, "end": v(45.64, 12.49) * mm});
            skLineSegment(sketch, "E34.33.8.1", {"start": v(45.64, 12.49) * mm, "end": v(42.75, 12.49) * mm});
            skLineSegment(sketch, "E34.0.8.2", {"start": v(37.34, 8.11) * mm, "end": v(40.22, 8.11) * mm});
            skLineSegment(sketch, "E34.3.8.2", {"start": v(35.9, 5.61) * mm, "end": v(37.34, 8.11) * mm});
            skLineSegment(sketch, "E34.6.8.2", {"start": v(37.34, 3.11) * mm, "end": v(35.9, 5.61) * mm});
            skLineSegment(sketch, "E34.9.8.2", {"start": v(40.22, 3.11) * mm, "end": v(37.34, 3.11) * mm});
            skLineSegment(sketch, "E34.12.8.2", {"start": v(41.67, 5.61) * mm, "end": v(40.22, 3.11) * mm});
            skLineSegment(sketch, "E34.15.8.2", {"start": v(40.22, 8.11) * mm, "end": v(41.67, 5.61) * mm});
            skLineSegment(sketch, "E34.18.8.2", {"start": v(42.75, 6.24) * mm, "end": v(41.3, 8.74) * mm});
            skLineSegment(sketch, "E34.21.8.2", {"start": v(41.3, 8.74) * mm, "end": v(42.75, 11.24) * mm});
            skLineSegment(sketch, "E34.24.8.2", {"start": v(42.75, 11.24) * mm, "end": v(45.64, 11.24) * mm});
            skLineSegment(sketch, "E34.27.8.2", {"start": v(45.64, 11.24) * mm, "end": v(47.08, 8.74) * mm});
            skLineSegment(sketch, "E34.30.8.2", {"start": v(47.08, 8.74) * mm, "end": v(45.64, 6.24) * mm});
            skLineSegment(sketch, "E34.33.8.2", {"start": v(45.64, 6.24) * mm, "end": v(42.75, 6.24) * mm});
            skLineSegment(sketch, "E34.0.8.3", {"start": v(37.34, 1.86) * mm, "end": v(40.22, 1.86) * mm});
            skLineSegment(sketch, "E34.3.8.3", {"start": v(35.9, -0.64) * mm, "end": v(37.34, 1.86) * mm});
            skLineSegment(sketch, "E34.6.8.3", {"start": v(37.34, -3.14) * mm, "end": v(35.9, -0.64) * mm});
            skLineSegment(sketch, "E34.9.8.3", {"start": v(40.22, -3.14) * mm, "end": v(37.34, -3.14) * mm});
            skLineSegment(sketch, "E34.12.8.3", {"start": v(41.67, -0.64) * mm, "end": v(40.22, -3.14) * mm});
            skLineSegment(sketch, "E34.15.8.3", {"start": v(40.22, 1.86) * mm, "end": v(41.67, -0.64) * mm});
            skLineSegment(sketch, "E34.18.8.3", {"start": v(42.75, -0.01) * mm, "end": v(41.3, 2.49) * mm});
            skLineSegment(sketch, "E34.21.8.3", {"start": v(41.3, 2.49) * mm, "end": v(42.75, 4.99) * mm});
            skLineSegment(sketch, "E34.24.8.3", {"start": v(42.75, 4.99) * mm, "end": v(45.64, 4.99) * mm});
            skLineSegment(sketch, "E34.27.8.3", {"start": v(45.64, 4.99) * mm, "end": v(47.08, 2.49) * mm});
            skLineSegment(sketch, "E34.30.8.3", {"start": v(47.08, 2.49) * mm, "end": v(45.64, -0.01) * mm});
            skLineSegment(sketch, "E34.33.8.3", {"start": v(45.64, -0.01) * mm, "end": v(42.75, -0.01) * mm});
            skLineSegment(sketch, "E34.0.9.0", {"start": v(48.33, 20.61) * mm, "end": v(51.22, 20.61) * mm});
            skLineSegment(sketch, "E34.3.9.0", {"start": v(46.89, 18.11) * mm, "end": v(48.33, 20.61) * mm});
            skLineSegment(sketch, "E34.6.9.0", {"start": v(48.33, 15.61) * mm, "end": v(46.89, 18.11) * mm});
            skLineSegment(sketch, "E34.9.9.0", {"start": v(51.22, 15.61) * mm, "end": v(48.33, 15.61) * mm});
            skLineSegment(sketch, "E34.12.9.0", {"start": v(52.66, 18.11) * mm, "end": v(51.22, 15.61) * mm});
            skLineSegment(sketch, "E34.15.9.0", {"start": v(51.22, 20.61) * mm, "end": v(52.66, 18.11) * mm});
            skLineSegment(sketch, "E34.18.9.0", {"start": v(53.74, 18.74) * mm, "end": v(52.3, 21.24) * mm});
            skLineSegment(sketch, "E34.21.9.0", {"start": v(52.3, 21.24) * mm, "end": v(53.74, 23.74) * mm});
            skLineSegment(sketch, "E34.24.9.0", {"start": v(53.74, 23.74) * mm, "end": v(56.63, 23.74) * mm});
            skLineSegment(sketch, "E34.27.9.0", {"start": v(56.63, 23.74) * mm, "end": v(58.07, 21.24) * mm});
            skLineSegment(sketch, "E34.30.9.0", {"start": v(58.07, 21.24) * mm, "end": v(56.63, 18.74) * mm});
            skLineSegment(sketch, "E34.33.9.0", {"start": v(56.63, 18.74) * mm, "end": v(53.74, 18.74) * mm});
            skLineSegment(sketch, "E34.0.9.1", {"start": v(48.33, 14.36) * mm, "end": v(51.22, 14.36) * mm});
            skLineSegment(sketch, "E34.3.9.1", {"start": v(46.89, 11.86) * mm, "end": v(48.33, 14.36) * mm});
            skLineSegment(sketch, "E34.6.9.1", {"start": v(48.33, 9.36) * mm, "end": v(46.89, 11.86) * mm});
            skLineSegment(sketch, "E34.9.9.1", {"start": v(51.22, 9.36) * mm, "end": v(48.33, 9.36) * mm});
            skLineSegment(sketch, "E34.12.9.1", {"start": v(52.66, 11.86) * mm, "end": v(51.22, 9.36) * mm});
            skLineSegment(sketch, "E34.15.9.1", {"start": v(51.22, 14.36) * mm, "end": v(52.66, 11.86) * mm});
            skLineSegment(sketch, "E34.18.9.1", {"start": v(53.74, 12.49) * mm, "end": v(52.3, 14.99) * mm});
            skLineSegment(sketch, "E34.21.9.1", {"start": v(52.3, 14.99) * mm, "end": v(53.74, 17.49) * mm});
            skLineSegment(sketch, "E34.24.9.1", {"start": v(53.74, 17.49) * mm, "end": v(56.63, 17.49) * mm});
            skLineSegment(sketch, "E34.27.9.1", {"start": v(56.63, 17.49) * mm, "end": v(58.07, 14.99) * mm});
            skLineSegment(sketch, "E34.30.9.1", {"start": v(58.07, 14.99) * mm, "end": v(56.63, 12.49) * mm});
            skLineSegment(sketch, "E34.33.9.1", {"start": v(56.63, 12.49) * mm, "end": v(53.74, 12.49) * mm});
            skLineSegment(sketch, "E34.0.9.2", {"start": v(48.33, 8.11) * mm, "end": v(51.22, 8.11) * mm});
            skLineSegment(sketch, "E34.3.9.2", {"start": v(46.89, 5.61) * mm, "end": v(48.33, 8.11) * mm});
            skLineSegment(sketch, "E34.6.9.2", {"start": v(48.33, 3.11) * mm, "end": v(46.89, 5.61) * mm});
            skLineSegment(sketch, "E34.9.9.2", {"start": v(51.22, 3.11) * mm, "end": v(48.33, 3.11) * mm});
            skLineSegment(sketch, "E34.12.9.2", {"start": v(52.66, 5.61) * mm, "end": v(51.22, 3.11) * mm});
            skLineSegment(sketch, "E34.15.9.2", {"start": v(51.22, 8.11) * mm, "end": v(52.66, 5.61) * mm});
            skLineSegment(sketch, "E34.18.9.2", {"start": v(53.74, 6.24) * mm, "end": v(52.3, 8.74) * mm});
            skLineSegment(sketch, "E34.21.9.2", {"start": v(52.3, 8.74) * mm, "end": v(53.74, 11.24) * mm});
            skLineSegment(sketch, "E34.24.9.2", {"start": v(53.74, 11.24) * mm, "end": v(56.63, 11.24) * mm});
            skLineSegment(sketch, "E34.27.9.2", {"start": v(56.63, 11.24) * mm, "end": v(58.07, 8.74) * mm});
            skLineSegment(sketch, "E34.30.9.2", {"start": v(58.07, 8.74) * mm, "end": v(56.63, 6.24) * mm});
            skLineSegment(sketch, "E34.33.9.2", {"start": v(56.63, 6.24) * mm, "end": v(53.74, 6.24) * mm});
            skLineSegment(sketch, "E34.0.9.3", {"start": v(48.33, 1.86) * mm, "end": v(51.22, 1.86) * mm});
            skLineSegment(sketch, "E34.3.9.3", {"start": v(46.89, -0.64) * mm, "end": v(48.33, 1.86) * mm});
            skLineSegment(sketch, "E34.6.9.3", {"start": v(48.33, -3.14) * mm, "end": v(46.89, -0.64) * mm});
            skLineSegment(sketch, "E34.9.9.3", {"start": v(51.22, -3.14) * mm, "end": v(48.33, -3.14) * mm});
            skLineSegment(sketch, "E34.12.9.3", {"start": v(52.66, -0.64) * mm, "end": v(51.22, -3.14) * mm});
            skLineSegment(sketch, "E34.15.9.3", {"start": v(51.22, 1.86) * mm, "end": v(52.66, -0.64) * mm});
            skLineSegment(sketch, "E34.18.9.3", {"start": v(53.74, -0.01) * mm, "end": v(52.3, 2.49) * mm});
            skLineSegment(sketch, "E34.21.9.3", {"start": v(52.3, 2.49) * mm, "end": v(53.74, 4.99) * mm});
            skLineSegment(sketch, "E34.24.9.3", {"start": v(53.74, 4.99) * mm, "end": v(56.63, 4.99) * mm});
            skLineSegment(sketch, "E34.27.9.3", {"start": v(56.63, 4.99) * mm, "end": v(58.07, 2.49) * mm});
            skLineSegment(sketch, "E34.30.9.3", {"start": v(58.07, 2.49) * mm, "end": v(56.63, -0.01) * mm});
            skLineSegment(sketch, "E34.33.9.3", {"start": v(56.63, -0.01) * mm, "end": v(53.74, -0.01) * mm});
            skLineSegment(sketch, "E35.0.10.0", {"start": v(59.32, 20.61) * mm, "end": v(62.2, 20.61) * mm});
            skLineSegment(sketch, "E35.3.10.0", {"start": v(57.88, 18.11) * mm, "end": v(59.32, 20.61) * mm});
            skLineSegment(sketch, "E35.6.10.0", {"start": v(59.32, 15.61) * mm, "end": v(57.88, 18.11) * mm});
            skLineSegment(sketch, "E35.9.10.0", {"start": v(62.2, 15.61) * mm, "end": v(59.32, 15.61) * mm});
            skLineSegment(sketch, "E35.12.10.0", {"start": v(63.65, 18.11) * mm, "end": v(62.2, 15.61) * mm});
            skLineSegment(sketch, "E35.15.10.0", {"start": v(62.2, 20.61) * mm, "end": v(63.65, 18.11) * mm});
            skLineSegment(sketch, "E35.18.10.0", {"start": v(64.73, 18.74) * mm, "end": v(63.3, 21.24) * mm});
            skLineSegment(sketch, "E35.21.10.0", {"start": v(63.3, 21.24) * mm, "end": v(64.73, 23.74) * mm});
            skLineSegment(sketch, "E35.24.10.0", {"start": v(64.73, 23.74) * mm, "end": v(67.62, 23.74) * mm});
            skLineSegment(sketch, "E35.27.10.0", {"start": v(67.62, 23.74) * mm, "end": v(69.07, 21.24) * mm});
            skLineSegment(sketch, "E35.30.10.0", {"start": v(69.07, 21.24) * mm, "end": v(67.62, 18.74) * mm});
            skLineSegment(sketch, "E35.33.10.0", {"start": v(67.62, 18.74) * mm, "end": v(64.73, 18.74) * mm});
            skLineSegment(sketch, "E35.0.10.1", {"start": v(59.32, 14.36) * mm, "end": v(62.2, 14.36) * mm});
            skLineSegment(sketch, "E35.3.10.1", {"start": v(57.88, 11.86) * mm, "end": v(59.32, 14.36) * mm});
            skLineSegment(sketch, "E35.6.10.1", {"start": v(59.32, 9.36) * mm, "end": v(57.88, 11.86) * mm});
            skLineSegment(sketch, "E35.9.10.1", {"start": v(62.2, 9.36) * mm, "end": v(59.32, 9.36) * mm});
            skLineSegment(sketch, "E35.12.10.1", {"start": v(63.65, 11.86) * mm, "end": v(62.2, 9.36) * mm});
            skLineSegment(sketch, "E35.15.10.1", {"start": v(62.2, 14.36) * mm, "end": v(63.65, 11.86) * mm});
            skLineSegment(sketch, "E35.18.10.1", {"start": v(64.73, 12.49) * mm, "end": v(63.3, 14.99) * mm});
            skLineSegment(sketch, "E35.21.10.1", {"start": v(63.3, 14.99) * mm, "end": v(64.73, 17.49) * mm});
            skLineSegment(sketch, "E35.24.10.1", {"start": v(64.73, 17.49) * mm, "end": v(67.62, 17.49) * mm});
            skLineSegment(sketch, "E35.27.10.1", {"start": v(67.62, 17.49) * mm, "end": v(69.07, 14.99) * mm});
            skLineSegment(sketch, "E35.30.10.1", {"start": v(69.07, 14.99) * mm, "end": v(67.62, 12.49) * mm});
            skLineSegment(sketch, "E35.33.10.1", {"start": v(67.62, 12.49) * mm, "end": v(64.73, 12.49) * mm});
            skLineSegment(sketch, "E35.0.10.2", {"start": v(59.32, 8.11) * mm, "end": v(62.2, 8.11) * mm});
            skLineSegment(sketch, "E35.3.10.2", {"start": v(57.88, 5.61) * mm, "end": v(59.32, 8.11) * mm});
            skLineSegment(sketch, "E35.6.10.2", {"start": v(59.32, 3.11) * mm, "end": v(57.88, 5.61) * mm});
            skLineSegment(sketch, "E35.9.10.2", {"start": v(62.2, 3.11) * mm, "end": v(59.32, 3.11) * mm});
            skLineSegment(sketch, "E35.12.10.2", {"start": v(63.65, 5.61) * mm, "end": v(62.2, 3.11) * mm});
            skLineSegment(sketch, "E35.15.10.2", {"start": v(62.2, 8.11) * mm, "end": v(63.65, 5.61) * mm});
            skLineSegment(sketch, "E35.18.10.2", {"start": v(64.73, 6.24) * mm, "end": v(63.3, 8.74) * mm});
            skLineSegment(sketch, "E35.21.10.2", {"start": v(63.3, 8.74) * mm, "end": v(64.73, 11.24) * mm});
            skLineSegment(sketch, "E35.24.10.2", {"start": v(64.73, 11.24) * mm, "end": v(67.62, 11.24) * mm});
            skLineSegment(sketch, "E35.27.10.2", {"start": v(67.62, 11.24) * mm, "end": v(69.07, 8.74) * mm});
            skLineSegment(sketch, "E35.30.10.2", {"start": v(69.07, 8.74) * mm, "end": v(67.62, 6.24) * mm});
            skLineSegment(sketch, "E35.33.10.2", {"start": v(67.62, 6.24) * mm, "end": v(64.73, 6.24) * mm});
            skLineSegment(sketch, "E35.0.10.3", {"start": v(59.32, 1.86) * mm, "end": v(62.2, 1.86) * mm});
            skLineSegment(sketch, "E35.3.10.3", {"start": v(57.88, -0.64) * mm, "end": v(59.32, 1.86) * mm});
            skLineSegment(sketch, "E35.6.10.3", {"start": v(59.32, -3.14) * mm, "end": v(57.88, -0.64) * mm});
            skLineSegment(sketch, "E35.9.10.3", {"start": v(62.2, -3.14) * mm, "end": v(59.32, -3.14) * mm});
            skLineSegment(sketch, "E35.12.10.3", {"start": v(63.65, -0.64) * mm, "end": v(62.2, -3.14) * mm});
            skLineSegment(sketch, "E35.15.10.3", {"start": v(62.2, 1.86) * mm, "end": v(63.65, -0.64) * mm});
            skLineSegment(sketch, "E35.18.10.3", {"start": v(64.73, -0.01) * mm, "end": v(63.3, 2.49) * mm});
            skLineSegment(sketch, "E35.21.10.3", {"start": v(63.3, 2.49) * mm, "end": v(64.73, 4.99) * mm});
            skLineSegment(sketch, "E35.24.10.3", {"start": v(64.73, 4.99) * mm, "end": v(67.62, 4.99) * mm});
            skLineSegment(sketch, "E35.27.10.3", {"start": v(67.62, 4.99) * mm, "end": v(69.07, 2.49) * mm});
            skLineSegment(sketch, "E35.30.10.3", {"start": v(69.07, 2.49) * mm, "end": v(67.62, -0.01) * mm});
            skLineSegment(sketch, "E35.33.10.3", {"start": v(67.62, -0.01) * mm, "end": v(64.73, -0.01) * mm});
            skLineSegment(sketch, "E35.0.11.0", {"start": v(70.32, 20.61) * mm, "end": v(73.2, 20.61) * mm});
            skLineSegment(sketch, "E35.3.11.0", {"start": v(68.87, 18.11) * mm, "end": v(70.32, 20.61) * mm});
            skLineSegment(sketch, "E35.6.11.0", {"start": v(70.32, 15.61) * mm, "end": v(68.87, 18.11) * mm});
            skLineSegment(sketch, "E35.9.11.0", {"start": v(73.2, 15.61) * mm, "end": v(70.32, 15.61) * mm});
            skLineSegment(sketch, "E35.12.11.0", {"start": v(74.65, 18.11) * mm, "end": v(73.2, 15.61) * mm});
            skLineSegment(sketch, "E35.15.11.0", {"start": v(73.2, 20.61) * mm, "end": v(74.65, 18.11) * mm});
            skLineSegment(sketch, "E35.18.11.0", {"start": v(75.73, 18.74) * mm, "end": v(74.28, 21.24) * mm});
            skLineSegment(sketch, "E35.21.11.0", {"start": v(74.28, 21.24) * mm, "end": v(75.73, 23.74) * mm});
            skLineSegment(sketch, "E35.24.11.0", {"start": v(75.73, 23.74) * mm, "end": v(78.61, 23.74) * mm});
            skLineSegment(sketch, "E35.27.11.0", {"start": v(78.61, 23.74) * mm, "end": v(80.06, 21.24) * mm});
            skLineSegment(sketch, "E35.30.11.0", {"start": v(80.06, 21.24) * mm, "end": v(78.61, 18.74) * mm});
            skLineSegment(sketch, "E35.33.11.0", {"start": v(78.61, 18.74) * mm, "end": v(75.73, 18.74) * mm});
            skLineSegment(sketch, "E35.0.11.1", {"start": v(70.32, 14.36) * mm, "end": v(73.2, 14.36) * mm});
            skLineSegment(sketch, "E35.3.11.1", {"start": v(68.87, 11.86) * mm, "end": v(70.32, 14.36) * mm});
            skLineSegment(sketch, "E35.6.11.1", {"start": v(70.32, 9.36) * mm, "end": v(68.87, 11.86) * mm});
            skLineSegment(sketch, "E35.9.11.1", {"start": v(73.2, 9.36) * mm, "end": v(70.32, 9.36) * mm});
            skLineSegment(sketch, "E35.12.11.1", {"start": v(74.65, 11.86) * mm, "end": v(73.2, 9.36) * mm});
            skLineSegment(sketch, "E35.15.11.1", {"start": v(73.2, 14.36) * mm, "end": v(74.65, 11.86) * mm});
            skLineSegment(sketch, "E35.18.11.1", {"start": v(75.73, 12.49) * mm, "end": v(74.28, 14.99) * mm});
            skLineSegment(sketch, "E35.21.11.1", {"start": v(74.28, 14.99) * mm, "end": v(75.73, 17.49) * mm});
            skLineSegment(sketch, "E35.24.11.1", {"start": v(75.73, 17.49) * mm, "end": v(78.61, 17.49) * mm});
            skLineSegment(sketch, "E35.27.11.1", {"start": v(78.61, 17.49) * mm, "end": v(80.06, 14.99) * mm});
            skLineSegment(sketch, "E35.30.11.1", {"start": v(80.06, 14.99) * mm, "end": v(78.61, 12.49) * mm});
            skLineSegment(sketch, "E35.33.11.1", {"start": v(78.61, 12.49) * mm, "end": v(75.73, 12.49) * mm});
            skLineSegment(sketch, "E35.0.11.2", {"start": v(70.32, 8.11) * mm, "end": v(73.2, 8.11) * mm});
            skLineSegment(sketch, "E35.3.11.2", {"start": v(68.87, 5.61) * mm, "end": v(70.32, 8.11) * mm});
            skLineSegment(sketch, "E35.6.11.2", {"start": v(70.32, 3.11) * mm, "end": v(68.87, 5.61) * mm});
            skLineSegment(sketch, "E35.9.11.2", {"start": v(73.2, 3.11) * mm, "end": v(70.32, 3.11) * mm});
            skLineSegment(sketch, "E35.12.11.2", {"start": v(74.65, 5.61) * mm, "end": v(73.2, 3.11) * mm});
            skLineSegment(sketch, "E35.15.11.2", {"start": v(73.2, 8.11) * mm, "end": v(74.65, 5.61) * mm});
            skLineSegment(sketch, "E35.18.11.2", {"start": v(75.73, 6.24) * mm, "end": v(74.28, 8.74) * mm});
            skLineSegment(sketch, "E35.21.11.2", {"start": v(74.28, 8.74) * mm, "end": v(75.73, 11.24) * mm});
            skLineSegment(sketch, "E35.24.11.2", {"start": v(75.73, 11.24) * mm, "end": v(78.61, 11.24) * mm});
            skLineSegment(sketch, "E35.27.11.2", {"start": v(78.61, 11.24) * mm, "end": v(80.06, 8.74) * mm});
            skLineSegment(sketch, "E35.30.11.2", {"start": v(80.06, 8.74) * mm, "end": v(78.61, 6.24) * mm});
            skLineSegment(sketch, "E35.33.11.2", {"start": v(78.61, 6.24) * mm, "end": v(75.73, 6.24) * mm});
            skLineSegment(sketch, "E35.0.11.3", {"start": v(70.32, 1.86) * mm, "end": v(73.2, 1.86) * mm});
            skLineSegment(sketch, "E35.3.11.3", {"start": v(68.87, -0.64) * mm, "end": v(70.32, 1.86) * mm});
            skLineSegment(sketch, "E35.6.11.3", {"start": v(70.32, -3.14) * mm, "end": v(68.87, -0.64) * mm});
            skLineSegment(sketch, "E35.9.11.3", {"start": v(73.2, -3.14) * mm, "end": v(70.32, -3.14) * mm});
            skLineSegment(sketch, "E35.12.11.3", {"start": v(74.65, -0.64) * mm, "end": v(73.2, -3.14) * mm});
            skLineSegment(sketch, "E35.15.11.3", {"start": v(73.2, 1.86) * mm, "end": v(74.65, -0.64) * mm});
            skLineSegment(sketch, "E35.18.11.3", {"start": v(75.73, -0.01) * mm, "end": v(74.28, 2.49) * mm});
            skLineSegment(sketch, "E35.21.11.3", {"start": v(74.28, 2.49) * mm, "end": v(75.73, 4.99) * mm});
            skLineSegment(sketch, "E35.24.11.3", {"start": v(75.73, 4.99) * mm, "end": v(78.61, 4.99) * mm});
            skLineSegment(sketch, "E35.27.11.3", {"start": v(78.61, 4.99) * mm, "end": v(80.06, 2.49) * mm});
            skLineSegment(sketch, "E35.30.11.3", {"start": v(80.06, 2.49) * mm, "end": v(78.61, -0.01) * mm});
            skLineSegment(sketch, "E35.33.11.3", {"start": v(78.61, -0.01) * mm, "end": v(75.73, -0.01) * mm});
            skLineSegment(sketch, "E35.0.12.0", {"start": v(81.3, 20.61) * mm, "end": v(84.2, 20.61) * mm});
            skLineSegment(sketch, "E35.3.12.0", {"start": v(79.86, 18.11) * mm, "end": v(81.3, 20.61) * mm});
            skLineSegment(sketch, "E35.6.12.0", {"start": v(81.3, 15.61) * mm, "end": v(79.86, 18.11) * mm});
            skLineSegment(sketch, "E35.9.12.0", {"start": v(84.2, 15.61) * mm, "end": v(81.3, 15.61) * mm});
            skLineSegment(sketch, "E35.12.12.0", {"start": v(85.64, 18.11) * mm, "end": v(84.2, 15.61) * mm});
            skLineSegment(sketch, "E35.15.12.0", {"start": v(84.2, 20.61) * mm, "end": v(85.64, 18.11) * mm});
            skLineSegment(sketch, "E35.18.12.0", {"start": v(86.72, 18.74) * mm, "end": v(85.28, 21.24) * mm});
            skLineSegment(sketch, "E35.21.12.0", {"start": v(85.28, 21.24) * mm, "end": v(86.72, 23.74) * mm});
            skLineSegment(sketch, "E35.24.12.0", {"start": v(86.72, 23.74) * mm, "end": v(89.6, 23.74) * mm});
            skLineSegment(sketch, "E35.27.12.0", {"start": v(89.6, 23.74) * mm, "end": v(91.05, 21.24) * mm});
            skLineSegment(sketch, "E35.30.12.0", {"start": v(91.05, 21.24) * mm, "end": v(89.6, 18.74) * mm});
            skLineSegment(sketch, "E35.33.12.0", {"start": v(89.6, 18.74) * mm, "end": v(86.72, 18.74) * mm});
            skLineSegment(sketch, "E35.0.12.1", {"start": v(81.3, 14.36) * mm, "end": v(84.2, 14.36) * mm});
            skLineSegment(sketch, "E35.3.12.1", {"start": v(79.86, 11.86) * mm, "end": v(81.3, 14.36) * mm});
            skLineSegment(sketch, "E35.6.12.1", {"start": v(81.3, 9.36) * mm, "end": v(79.86, 11.86) * mm});
            skLineSegment(sketch, "E35.9.12.1", {"start": v(84.2, 9.36) * mm, "end": v(81.3, 9.36) * mm});
            skLineSegment(sketch, "E35.12.12.1", {"start": v(85.64, 11.86) * mm, "end": v(84.2, 9.36) * mm});
            skLineSegment(sketch, "E35.15.12.1", {"start": v(84.2, 14.36) * mm, "end": v(85.64, 11.86) * mm});
            skLineSegment(sketch, "E35.18.12.1", {"start": v(86.72, 12.49) * mm, "end": v(85.28, 14.99) * mm});
            skLineSegment(sketch, "E35.21.12.1", {"start": v(85.28, 14.99) * mm, "end": v(86.72, 17.49) * mm});
            skLineSegment(sketch, "E35.24.12.1", {"start": v(86.72, 17.49) * mm, "end": v(89.6, 17.49) * mm});
            skLineSegment(sketch, "E35.27.12.1", {"start": v(89.6, 17.49) * mm, "end": v(91.05, 14.99) * mm});
            skLineSegment(sketch, "E35.30.12.1", {"start": v(91.05, 14.99) * mm, "end": v(89.6, 12.49) * mm});
            skLineSegment(sketch, "E35.33.12.1", {"start": v(89.6, 12.49) * mm, "end": v(86.72, 12.49) * mm});
            skLineSegment(sketch, "E35.0.12.2", {"start": v(81.3, 8.11) * mm, "end": v(84.2, 8.11) * mm});
            skLineSegment(sketch, "E35.3.12.2", {"start": v(79.86, 5.61) * mm, "end": v(81.3, 8.11) * mm});
            skLineSegment(sketch, "E35.6.12.2", {"start": v(81.3, 3.11) * mm, "end": v(79.86, 5.61) * mm});
            skLineSegment(sketch, "E35.9.12.2", {"start": v(84.2, 3.11) * mm, "end": v(81.3, 3.11) * mm});
            skLineSegment(sketch, "E35.12.12.2", {"start": v(85.64, 5.61) * mm, "end": v(84.2, 3.11) * mm});
            skLineSegment(sketch, "E35.15.12.2", {"start": v(84.2, 8.11) * mm, "end": v(85.64, 5.61) * mm});
            skLineSegment(sketch, "E35.18.12.2", {"start": v(86.72, 6.24) * mm, "end": v(85.28, 8.74) * mm});
            skLineSegment(sketch, "E35.21.12.2", {"start": v(85.28, 8.74) * mm, "end": v(86.72, 11.24) * mm});
            skLineSegment(sketch, "E35.24.12.2", {"start": v(86.72, 11.24) * mm, "end": v(89.6, 11.24) * mm});
            skLineSegment(sketch, "E35.27.12.2", {"start": v(89.6, 11.24) * mm, "end": v(91.05, 8.74) * mm});
            skLineSegment(sketch, "E35.30.12.2", {"start": v(91.05, 8.74) * mm, "end": v(89.6, 6.24) * mm});
            skLineSegment(sketch, "E35.33.12.2", {"start": v(89.6, 6.24) * mm, "end": v(86.72, 6.24) * mm});
            skLineSegment(sketch, "E35.0.12.3", {"start": v(81.3, 1.86) * mm, "end": v(84.2, 1.86) * mm});
            skLineSegment(sketch, "E35.3.12.3", {"start": v(79.86, -0.64) * mm, "end": v(81.3, 1.86) * mm});
            skLineSegment(sketch, "E35.6.12.3", {"start": v(81.3, -3.14) * mm, "end": v(79.86, -0.64) * mm});
            skLineSegment(sketch, "E35.9.12.3", {"start": v(84.2, -3.14) * mm, "end": v(81.3, -3.14) * mm});
            skLineSegment(sketch, "E35.12.12.3", {"start": v(85.64, -0.64) * mm, "end": v(84.2, -3.14) * mm});
            skLineSegment(sketch, "E35.15.12.3", {"start": v(84.2, 1.86) * mm, "end": v(85.64, -0.64) * mm});
            skLineSegment(sketch, "E35.18.12.3", {"start": v(86.72, -0.01) * mm, "end": v(85.28, 2.49) * mm});
            skLineSegment(sketch, "E35.21.12.3", {"start": v(85.28, 2.49) * mm, "end": v(86.72, 4.99) * mm});
            skLineSegment(sketch, "E35.24.12.3", {"start": v(86.72, 4.99) * mm, "end": v(89.6, 4.99) * mm});
            skLineSegment(sketch, "E35.27.12.3", {"start": v(89.6, 4.99) * mm, "end": v(91.05, 2.49) * mm});
            skLineSegment(sketch, "E35.30.12.3", {"start": v(91.05, 2.49) * mm, "end": v(89.6, -0.01) * mm});
            skLineSegment(sketch, "E35.33.12.3", {"start": v(89.6, -0.01) * mm, "end": v(86.72, -0.01) * mm});
            skSolve(sketch);
        }
        {
            var Q0;
            {var subQ0=sQuery(id+"F6.wireOp",EDGE,"E30.0");Q0=makeQuery(id+"F6.imprint","IMPRINT",FACE,{"disambiguationData":[TD([[makeQuery(id+"F6.imprint","IMPRINT",EDGE,{"derivedFrom":subQ0}),-1.0]])]});}
            var Q1;
            {var subQ5=sQuery(id+"F6.wireOp",EDGE,"E31.0.1.0");Q1=makeQuery(id+"F6.imprint","IMPRINT",FACE,{"disambiguationData":[TD([[makeQuery(id+"F6.imprint","IMPRINT",EDGE,{"derivedFrom":subQ5}),-1.0]])]});}
            var Q2;
            {var subQ0=sQuery(id+"F6.wireOp",EDGE,"E32.0.0.2");Q2=makeQuery(id+"F6.imprint","IMPRINT",FACE,{"disambiguationData":[TD([[makeQuery(id+"F6.imprint","IMPRINT",EDGE,{"derivedFrom":subQ0}),-1.0]])]});}
            var Q3;
            Q3=makeQuery(id+"F6.imprint","IMPRINT",FACE,{"disambiguationData":[TD([[makeQuery(id+"F6.imprint","IMPRINT",EDGE,{"derivedFrom":sQuery(id+"F6.wireOp",EDGE,"E31.0.1.6")}),-1.0]])]});
            var Q4;
            Q4=makeQuery(id+"F6.imprint","IMPRINT",FACE,{"disambiguationData":[TD([[makeQuery(id+"F6.imprint","IMPRINT",EDGE,{"derivedFrom":sQuery(id+"F6.wireOp",EDGE,"E32.18.0.2")}),-1.0]])]});
            var Q5;
            {var subQ5=sQuery(id+"F6.wireOp",EDGE,"E33.24.0.3");Q5=makeQuery(id+"F6.imprint","IMPRINT",FACE,{"disambiguationData":[TD([[makeQuery(id+"F6.imprint","IMPRINT",EDGE,{"derivedFrom":subQ5}),-1.0]])]});}
            var Q6;
            {var subQ0=sQuery(id+"F6.wireOp",EDGE,"E31.1.0.2");Q6=makeQuery(id+"F6.imprint","IMPRINT",FACE,{"disambiguationData":[TD([[makeQuery(id+"F6.imprint","IMPRINT",EDGE,{"derivedFrom":subQ0}),-1.0]])]});}
            var Q7;
            Q7=makeQuery(id+"F6.imprint","IMPRINT",FACE,{"disambiguationData":[TD([[makeQuery(id+"F6.imprint","IMPRINT",EDGE,{"derivedFrom":sQuery(id+"F6.wireOp",EDGE,"E31.1.1.0")}),-1.0]])]});
            var Q8;
            Q8=makeQuery(id+"F6.imprint","IMPRINT",FACE,{"disambiguationData":[TD([[makeQuery(id+"F6.imprint","IMPRINT",EDGE,{"derivedFrom":sQuery(id+"F6.wireOp",EDGE,"E32.0.1.2")}),-1.0]])]});
            var Q9;
            Q9=makeQuery(id+"F6.imprint","IMPRINT",FACE,{"disambiguationData":[TD([[makeQuery(id+"F6.imprint","IMPRINT",EDGE,{"derivedFrom":sQuery(id+"F6.wireOp",EDGE,"E31.1.1.6")}),-1.0]])]});
            var Q10;
            Q10=makeQuery(id+"F6.imprint","IMPRINT",FACE,{"disambiguationData":[TD([[makeQuery(id+"F6.imprint","IMPRINT",EDGE,{"derivedFrom":sQuery(id+"F6.wireOp",EDGE,"E32.18.1.2")}),-1.0]])]});
            var Q11;
            {var subQ5=sQuery(id+"F6.wireOp",EDGE,"E33.24.1.3");Q11=makeQuery(id+"F6.imprint","IMPRINT",FACE,{"disambiguationData":[TD([[makeQuery(id+"F6.imprint","IMPRINT",EDGE,{"derivedFrom":subQ5}),-1.0]])]});}
            var Q12;
            {var subQ5=sQuery(id+"F6.wireOp",EDGE,"E31.2.0.2");Q12=makeQuery(id+"F6.imprint","IMPRINT",FACE,{"disambiguationData":[TD([[makeQuery(id+"F6.imprint","IMPRINT",EDGE,{"derivedFrom":subQ5}),-1.0]])]});}
            var Q13;
            Q13=makeQuery(id+"F6.imprint","IMPRINT",FACE,{"disambiguationData":[TD([[makeQuery(id+"F6.imprint","IMPRINT",EDGE,{"derivedFrom":sQuery(id+"F6.wireOp",EDGE,"E31.2.1.0")}),-1.0]])]});
            var Q14;
            Q14=makeQuery(id+"F6.imprint","IMPRINT",FACE,{"disambiguationData":[TD([[makeQuery(id+"F6.imprint","IMPRINT",EDGE,{"derivedFrom":sQuery(id+"F6.wireOp",EDGE,"E32.0.2.2")}),-1.0]])]});
            var Q15;
            Q15=makeQuery(id+"F6.imprint","IMPRINT",FACE,{"disambiguationData":[TD([[makeQuery(id+"F6.imprint","IMPRINT",EDGE,{"derivedFrom":sQuery(id+"F6.wireOp",EDGE,"E31.2.1.6")}),-1.0]])]});
            var Q16;
            Q16=makeQuery(id+"F6.imprint","IMPRINT",FACE,{"disambiguationData":[TD([[makeQuery(id+"F6.imprint","IMPRINT",EDGE,{"derivedFrom":sQuery(id+"F6.wireOp",EDGE,"E32.18.2.2")}),-1.0]])]});
            var Q17;
            {var subQ5=sQuery(id+"F6.wireOp",EDGE,"E33.24.2.3");Q17=makeQuery(id+"F6.imprint","IMPRINT",FACE,{"disambiguationData":[TD([[makeQuery(id+"F6.imprint","IMPRINT",EDGE,{"derivedFrom":subQ5}),-1.0]])]});}
            var Q18;
            {var subQ0=sQuery(id+"F6.wireOp",EDGE,"E34.6.3.0");Q18=makeQuery(id+"F6.imprint","IMPRINT",FACE,{"disambiguationData":[TD([[makeQuery(id+"F6.imprint","IMPRINT",EDGE,{"derivedFrom":subQ0}),-1.0]])]});}
            var Q19;
            Q19=makeQuery(id+"F6.imprint","IMPRINT",FACE,{"disambiguationData":[TD([[makeQuery(id+"F6.imprint","IMPRINT",EDGE,{"derivedFrom":sQuery(id+"F6.wireOp",EDGE,"E34.0.3.1")}),-1.0]])]});
            var Q20;
            Q20=makeQuery(id+"F6.imprint","IMPRINT",FACE,{"disambiguationData":[TD([[makeQuery(id+"F6.imprint","IMPRINT",EDGE,{"derivedFrom":sQuery(id+"F6.wireOp",EDGE,"E34.0.3.2")}),-1.0]])]});
            var Q21;
            Q21=makeQuery(id+"F6.imprint","IMPRINT",FACE,{"disambiguationData":[TD([[makeQuery(id+"F6.imprint","IMPRINT",EDGE,{"derivedFrom":sQuery(id+"F6.wireOp",EDGE,"E34.18.3.1")}),-1.0]])]});
            var Q22;
            Q22=makeQuery(id+"F6.imprint","IMPRINT",FACE,{"disambiguationData":[TD([[makeQuery(id+"F6.imprint","IMPRINT",EDGE,{"derivedFrom":sQuery(id+"F6.wireOp",EDGE,"E34.18.3.2")}),-1.0]])]});
            var Q23;
            {var subQ5=sQuery(id+"F6.wireOp",EDGE,"E34.24.3.3");Q23=makeQuery(id+"F6.imprint","IMPRINT",FACE,{"disambiguationData":[TD([[makeQuery(id+"F6.imprint","IMPRINT",EDGE,{"derivedFrom":subQ5}),-1.0]])]});}
            var Q24;
            {var subQ0=sQuery(id+"F6.wireOp",EDGE,"E34.6.4.0");Q24=makeQuery(id+"F6.imprint","IMPRINT",FACE,{"disambiguationData":[TD([[makeQuery(id+"F6.imprint","IMPRINT",EDGE,{"derivedFrom":subQ0}),-1.0]])]});}
            var Q25;
            Q25=makeQuery(id+"F6.imprint","IMPRINT",FACE,{"disambiguationData":[TD([[makeQuery(id+"F6.imprint","IMPRINT",EDGE,{"derivedFrom":sQuery(id+"F6.wireOp",EDGE,"E34.0.4.1")}),-1.0]])]});
            var Q26;
            Q26=makeQuery(id+"F6.imprint","IMPRINT",FACE,{"disambiguationData":[TD([[makeQuery(id+"F6.imprint","IMPRINT",EDGE,{"derivedFrom":sQuery(id+"F6.wireOp",EDGE,"E34.0.4.2")}),-1.0]])]});
            var Q27;
            Q27=makeQuery(id+"F6.imprint","IMPRINT",FACE,{"disambiguationData":[TD([[makeQuery(id+"F6.imprint","IMPRINT",EDGE,{"derivedFrom":sQuery(id+"F6.wireOp",EDGE,"E34.18.4.1")}),-1.0]])]});
            var Q28;
            Q28=makeQuery(id+"F6.imprint","IMPRINT",FACE,{"disambiguationData":[TD([[makeQuery(id+"F6.imprint","IMPRINT",EDGE,{"derivedFrom":sQuery(id+"F6.wireOp",EDGE,"E34.18.4.2")}),-1.0]])]});
            var Q29;
            {var subQ5=sQuery(id+"F6.wireOp",EDGE,"E34.24.4.3");Q29=makeQuery(id+"F6.imprint","IMPRINT",FACE,{"disambiguationData":[TD([[makeQuery(id+"F6.imprint","IMPRINT",EDGE,{"derivedFrom":subQ5}),-1.0]])]});}
            var Q30;
            {var subQ0=sQuery(id+"F6.wireOp",EDGE,"E34.6.5.0");Q30=makeQuery(id+"F6.imprint","IMPRINT",FACE,{"disambiguationData":[TD([[makeQuery(id+"F6.imprint","IMPRINT",EDGE,{"derivedFrom":subQ0}),-1.0]])]});}
            var Q31;
            Q31=makeQuery(id+"F6.imprint","IMPRINT",FACE,{"disambiguationData":[TD([[makeQuery(id+"F6.imprint","IMPRINT",EDGE,{"derivedFrom":sQuery(id+"F6.wireOp",EDGE,"E34.0.5.1")}),-1.0]])]});
            var Q32;
            Q32=makeQuery(id+"F6.imprint","IMPRINT",FACE,{"disambiguationData":[TD([[makeQuery(id+"F6.imprint","IMPRINT",EDGE,{"derivedFrom":sQuery(id+"F6.wireOp",EDGE,"E34.0.5.2")}),-1.0]])]});
            var Q33;
            Q33=makeQuery(id+"F6.imprint","IMPRINT",FACE,{"disambiguationData":[TD([[makeQuery(id+"F6.imprint","IMPRINT",EDGE,{"derivedFrom":sQuery(id+"F6.wireOp",EDGE,"E34.18.5.1")}),-1.0]])]});
            var Q34;
            Q34=makeQuery(id+"F6.imprint","IMPRINT",FACE,{"disambiguationData":[TD([[makeQuery(id+"F6.imprint","IMPRINT",EDGE,{"derivedFrom":sQuery(id+"F6.wireOp",EDGE,"E34.18.5.2")}),-1.0]])]});
            var Q35;
            {var subQ5=sQuery(id+"F6.wireOp",EDGE,"E34.24.5.3");Q35=makeQuery(id+"F6.imprint","IMPRINT",FACE,{"disambiguationData":[TD([[makeQuery(id+"F6.imprint","IMPRINT",EDGE,{"derivedFrom":subQ5}),-1.0]])]});}
            var Q36;
            {var subQ0=sQuery(id+"F6.wireOp",EDGE,"E34.6.6.0");Q36=makeQuery(id+"F6.imprint","IMPRINT",FACE,{"disambiguationData":[TD([[makeQuery(id+"F6.imprint","IMPRINT",EDGE,{"derivedFrom":subQ0}),-1.0]])]});}
            var Q37;
            Q37=makeQuery(id+"F6.imprint","IMPRINT",FACE,{"disambiguationData":[TD([[makeQuery(id+"F6.imprint","IMPRINT",EDGE,{"derivedFrom":sQuery(id+"F6.wireOp",EDGE,"E34.0.6.1")}),-1.0]])]});
            var Q38;
            Q38=makeQuery(id+"F6.imprint","IMPRINT",FACE,{"disambiguationData":[TD([[makeQuery(id+"F6.imprint","IMPRINT",EDGE,{"derivedFrom":sQuery(id+"F6.wireOp",EDGE,"E34.0.6.2")}),-1.0]])]});
            var Q39;
            Q39=makeQuery(id+"F6.imprint","IMPRINT",FACE,{"disambiguationData":[TD([[makeQuery(id+"F6.imprint","IMPRINT",EDGE,{"derivedFrom":sQuery(id+"F6.wireOp",EDGE,"E34.18.6.1")}),-1.0]])]});
            var Q40;
            Q40=makeQuery(id+"F6.imprint","IMPRINT",FACE,{"disambiguationData":[TD([[makeQuery(id+"F6.imprint","IMPRINT",EDGE,{"derivedFrom":sQuery(id+"F6.wireOp",EDGE,"E34.18.6.2")}),-1.0]])]});
            var Q41;
            {var subQ5=sQuery(id+"F6.wireOp",EDGE,"E34.24.6.3");Q41=makeQuery(id+"F6.imprint","IMPRINT",FACE,{"disambiguationData":[TD([[makeQuery(id+"F6.imprint","IMPRINT",EDGE,{"derivedFrom":subQ5}),-1.0]])]});}
            var Q42;
            {var subQ0=sQuery(id+"F6.wireOp",EDGE,"E34.6.7.0");Q42=makeQuery(id+"F6.imprint","IMPRINT",FACE,{"disambiguationData":[TD([[makeQuery(id+"F6.imprint","IMPRINT",EDGE,{"derivedFrom":subQ0}),-1.0]])]});}
            var Q43;
            Q43=makeQuery(id+"F6.imprint","IMPRINT",FACE,{"disambiguationData":[TD([[makeQuery(id+"F6.imprint","IMPRINT",EDGE,{"derivedFrom":sQuery(id+"F6.wireOp",EDGE,"E34.0.7.1")}),-1.0]])]});
            var Q44;
            Q44=makeQuery(id+"F6.imprint","IMPRINT",FACE,{"disambiguationData":[TD([[makeQuery(id+"F6.imprint","IMPRINT",EDGE,{"derivedFrom":sQuery(id+"F6.wireOp",EDGE,"E34.0.7.2")}),-1.0]])]});
            var Q45;
            Q45=makeQuery(id+"F6.imprint","IMPRINT",FACE,{"disambiguationData":[TD([[makeQuery(id+"F6.imprint","IMPRINT",EDGE,{"derivedFrom":sQuery(id+"F6.wireOp",EDGE,"E34.18.7.1")}),-1.0]])]});
            var Q46;
            Q46=makeQuery(id+"F6.imprint","IMPRINT",FACE,{"disambiguationData":[TD([[makeQuery(id+"F6.imprint","IMPRINT",EDGE,{"derivedFrom":sQuery(id+"F6.wireOp",EDGE,"E34.18.7.2")}),-1.0]])]});
            var Q47;
            {var subQ5=sQuery(id+"F6.wireOp",EDGE,"E34.24.7.3");Q47=makeQuery(id+"F6.imprint","IMPRINT",FACE,{"disambiguationData":[TD([[makeQuery(id+"F6.imprint","IMPRINT",EDGE,{"derivedFrom":subQ5}),-1.0]])]});}
            var Q48;
            {var subQ0=sQuery(id+"F6.wireOp",EDGE,"E34.6.8.0");Q48=makeQuery(id+"F6.imprint","IMPRINT",FACE,{"disambiguationData":[TD([[makeQuery(id+"F6.imprint","IMPRINT",EDGE,{"derivedFrom":subQ0}),-1.0]])]});}
            var Q49;
            Q49=makeQuery(id+"F6.imprint","IMPRINT",FACE,{"disambiguationData":[TD([[makeQuery(id+"F6.imprint","IMPRINT",EDGE,{"derivedFrom":sQuery(id+"F6.wireOp",EDGE,"E34.0.8.1")}),-1.0]])]});
            var Q50;
            Q50=makeQuery(id+"F6.imprint","IMPRINT",FACE,{"disambiguationData":[TD([[makeQuery(id+"F6.imprint","IMPRINT",EDGE,{"derivedFrom":sQuery(id+"F6.wireOp",EDGE,"E34.0.8.2")}),-1.0]])]});
            var Q51;
            Q51=makeQuery(id+"F6.imprint","IMPRINT",FACE,{"disambiguationData":[TD([[makeQuery(id+"F6.imprint","IMPRINT",EDGE,{"derivedFrom":sQuery(id+"F6.wireOp",EDGE,"E34.18.8.1")}),-1.0]])]});
            var Q52;
            Q52=makeQuery(id+"F6.imprint","IMPRINT",FACE,{"disambiguationData":[TD([[makeQuery(id+"F6.imprint","IMPRINT",EDGE,{"derivedFrom":sQuery(id+"F6.wireOp",EDGE,"E34.18.8.2")}),-1.0]])]});
            var Q53;
            {var subQ5=sQuery(id+"F6.wireOp",EDGE,"E34.24.8.3");Q53=makeQuery(id+"F6.imprint","IMPRINT",FACE,{"disambiguationData":[TD([[makeQuery(id+"F6.imprint","IMPRINT",EDGE,{"derivedFrom":subQ5}),-1.0]])]});}
            var Q54;
            {var subQ0=sQuery(id+"F6.wireOp",EDGE,"E34.6.9.0");Q54=makeQuery(id+"F6.imprint","IMPRINT",FACE,{"disambiguationData":[TD([[makeQuery(id+"F6.imprint","IMPRINT",EDGE,{"derivedFrom":subQ0}),-1.0]])]});}
            var Q55;
            Q55=makeQuery(id+"F6.imprint","IMPRINT",FACE,{"disambiguationData":[TD([[makeQuery(id+"F6.imprint","IMPRINT",EDGE,{"derivedFrom":sQuery(id+"F6.wireOp",EDGE,"E34.0.9.1")}),-1.0]])]});
            var Q56;
            Q56=makeQuery(id+"F6.imprint","IMPRINT",FACE,{"disambiguationData":[TD([[makeQuery(id+"F6.imprint","IMPRINT",EDGE,{"derivedFrom":sQuery(id+"F6.wireOp",EDGE,"E34.0.9.2")}),-1.0]])]});
            var Q57;
            Q57=makeQuery(id+"F6.imprint","IMPRINT",FACE,{"disambiguationData":[TD([[makeQuery(id+"F6.imprint","IMPRINT",EDGE,{"derivedFrom":sQuery(id+"F6.wireOp",EDGE,"E34.18.9.1")}),-1.0]])]});
            var Q58;
            Q58=makeQuery(id+"F6.imprint","IMPRINT",FACE,{"disambiguationData":[TD([[makeQuery(id+"F6.imprint","IMPRINT",EDGE,{"derivedFrom":sQuery(id+"F6.wireOp",EDGE,"E34.18.9.2")}),-1.0]])]});
            var Q59;
            {var subQ5=sQuery(id+"F6.wireOp",EDGE,"E34.24.9.3");Q59=makeQuery(id+"F6.imprint","IMPRINT",FACE,{"disambiguationData":[TD([[makeQuery(id+"F6.imprint","IMPRINT",EDGE,{"derivedFrom":subQ5}),-1.0]])]});}
            var Q60;
            {var subQ0=sQuery(id+"F6.wireOp",EDGE,"E35.6.10.0");Q60=makeQuery(id+"F6.imprint","IMPRINT",FACE,{"disambiguationData":[TD([[makeQuery(id+"F6.imprint","IMPRINT",EDGE,{"derivedFrom":subQ0}),-1.0]])]});}
            var Q61;
            Q61=makeQuery(id+"F6.imprint","IMPRINT",FACE,{"disambiguationData":[TD([[makeQuery(id+"F6.imprint","IMPRINT",EDGE,{"derivedFrom":sQuery(id+"F6.wireOp",EDGE,"E35.0.10.1")}),-1.0]])]});
            var Q62;
            Q62=makeQuery(id+"F6.imprint","IMPRINT",FACE,{"disambiguationData":[TD([[makeQuery(id+"F6.imprint","IMPRINT",EDGE,{"derivedFrom":sQuery(id+"F6.wireOp",EDGE,"E35.0.10.2")}),-1.0]])]});
            var Q63;
            Q63=makeQuery(id+"F6.imprint","IMPRINT",FACE,{"disambiguationData":[TD([[makeQuery(id+"F6.imprint","IMPRINT",EDGE,{"derivedFrom":sQuery(id+"F6.wireOp",EDGE,"E35.18.10.1")}),-1.0]])]});
            var Q64;
            Q64=makeQuery(id+"F6.imprint","IMPRINT",FACE,{"disambiguationData":[TD([[makeQuery(id+"F6.imprint","IMPRINT",EDGE,{"derivedFrom":sQuery(id+"F6.wireOp",EDGE,"E35.18.10.2")}),-1.0]])]});
            var Q65;
            {var subQ5=sQuery(id+"F6.wireOp",EDGE,"E35.24.10.3");Q65=makeQuery(id+"F6.imprint","IMPRINT",FACE,{"disambiguationData":[TD([[makeQuery(id+"F6.imprint","IMPRINT",EDGE,{"derivedFrom":subQ5}),-1.0]])]});}
            var Q66;
            {var subQ0=sQuery(id+"F6.wireOp",EDGE,"E35.6.11.0");Q66=makeQuery(id+"F6.imprint","IMPRINT",FACE,{"disambiguationData":[TD([[makeQuery(id+"F6.imprint","IMPRINT",EDGE,{"derivedFrom":subQ0}),-1.0]])]});}
            var Q67;
            Q67=makeQuery(id+"F6.imprint","IMPRINT",FACE,{"disambiguationData":[TD([[makeQuery(id+"F6.imprint","IMPRINT",EDGE,{"derivedFrom":sQuery(id+"F6.wireOp",EDGE,"E35.0.11.1")}),-1.0]])]});
            var Q68;
            Q68=makeQuery(id+"F6.imprint","IMPRINT",FACE,{"disambiguationData":[TD([[makeQuery(id+"F6.imprint","IMPRINT",EDGE,{"derivedFrom":sQuery(id+"F6.wireOp",EDGE,"E35.0.11.2")}),-1.0]])]});
            var Q69;
            Q69=makeQuery(id+"F6.imprint","IMPRINT",FACE,{"disambiguationData":[TD([[makeQuery(id+"F6.imprint","IMPRINT",EDGE,{"derivedFrom":sQuery(id+"F6.wireOp",EDGE,"E35.18.11.1")}),-1.0]])]});
            var Q70;
            Q70=makeQuery(id+"F6.imprint","IMPRINT",FACE,{"disambiguationData":[TD([[makeQuery(id+"F6.imprint","IMPRINT",EDGE,{"derivedFrom":sQuery(id+"F6.wireOp",EDGE,"E35.18.11.2")}),-1.0]])]});
            var Q71;
            {var subQ5=sQuery(id+"F6.wireOp",EDGE,"E35.24.11.3");Q71=makeQuery(id+"F6.imprint","IMPRINT",FACE,{"disambiguationData":[TD([[makeQuery(id+"F6.imprint","IMPRINT",EDGE,{"derivedFrom":subQ5}),-1.0]])]});}
            var Q72;
            {var subQ0=sQuery(id+"F6.wireOp",EDGE,"E35.6.12.0");Q72=makeQuery(id+"F6.imprint","IMPRINT",FACE,{"disambiguationData":[TD([[makeQuery(id+"F6.imprint","IMPRINT",EDGE,{"derivedFrom":subQ0}),-1.0]])]});}
            var Q73;
            Q73=makeQuery(id+"F6.imprint","IMPRINT",FACE,{"disambiguationData":[TD([[makeQuery(id+"F6.imprint","IMPRINT",EDGE,{"derivedFrom":sQuery(id+"F6.wireOp",EDGE,"E35.0.12.1")}),-1.0]])]});
            var Q74;
            Q74=makeQuery(id+"F6.imprint","IMPRINT",FACE,{"disambiguationData":[TD([[makeQuery(id+"F6.imprint","IMPRINT",EDGE,{"derivedFrom":sQuery(id+"F6.wireOp",EDGE,"E35.0.12.2")}),-1.0]])]});
            var Q75;
            Q75=makeQuery(id+"F6.imprint","IMPRINT",FACE,{"disambiguationData":[TD([[makeQuery(id+"F6.imprint","IMPRINT",EDGE,{"derivedFrom":sQuery(id+"F6.wireOp",EDGE,"E35.18.12.1")}),-1.0]])]});
            var Q76;
            Q76=makeQuery(id+"F6.imprint","IMPRINT",FACE,{"disambiguationData":[TD([[makeQuery(id+"F6.imprint","IMPRINT",EDGE,{"derivedFrom":sQuery(id+"F6.wireOp",EDGE,"E35.18.12.2")}),-1.0]])]});
            var Q77;
            {var subQ5=sQuery(id+"F6.wireOp",EDGE,"E35.24.12.3");Q77=makeQuery(id+"F6.imprint","IMPRINT",FACE,{"disambiguationData":[TD([[makeQuery(id+"F6.imprint","IMPRINT",EDGE,{"derivedFrom":subQ5}),-1.0]])]});}
            var Q78;
            {var subQ0=sQuery(id+"F6.wireOp",EDGE,"E35.6.13.0");Q78=makeQuery(id+"F6.imprint","IMPRINT",FACE,{"disambiguationData":[TD([[makeQuery(id+"F6.imprint","IMPRINT",EDGE,{"derivedFrom":subQ0}),-1.0]])]});}
            var Q79;
            Q79=makeQuery(id+"F6.imprint","IMPRINT",FACE,{"disambiguationData":[TD([[makeQuery(id+"F6.imprint","IMPRINT",EDGE,{"derivedFrom":sQuery(id+"F6.wireOp",EDGE,"E35.0.13.1")}),-1.0]])]});
            var Q80;
            Q80=makeQuery(id+"F6.imprint","IMPRINT",FACE,{"disambiguationData":[TD([[makeQuery(id+"F6.imprint","IMPRINT",EDGE,{"derivedFrom":sQuery(id+"F6.wireOp",EDGE,"E35.0.13.2")}),-1.0]])]});
            var Q81;
            {var subQ5=sQuery(id+"F6.wireOp",EDGE,"E35.33.13.0");Q81=makeQuery(id+"F6.imprint","IMPRINT",FACE,{"disambiguationData":[TD([[makeQuery(id+"F6.imprint","IMPRINT",EDGE,{"derivedFrom":subQ5}),-1.0]])]});}
            var Q82;
            Q82=makeQuery(id+"F6.imprint","IMPRINT",FACE,{"disambiguationData":[TD([[makeQuery(id+"F6.imprint","IMPRINT",EDGE,{"derivedFrom":sQuery(id+"F6.wireOp",EDGE,"E35.18.13.1")}),-1.0]])]});
            var Q83;
            Q83=makeQuery(id+"F6.imprint","IMPRINT",FACE,{"disambiguationData":[TD([[makeQuery(id+"F6.imprint","IMPRINT",EDGE,{"derivedFrom":sQuery(id+"F6.wireOp",EDGE,"E35.18.13.2")}),-1.0]])]});
            var Q84;
            {var subQ5=sQuery(id+"F6.wireOp",EDGE,"E35.24.13.3");Q84=makeQuery(id+"F6.imprint","IMPRINT",FACE,{"disambiguationData":[TD([[makeQuery(id+"F6.imprint","IMPRINT",EDGE,{"derivedFrom":subQ5}),-1.0]])]});}
            var Q85;
            {var subQ0=sQuery(id+"F6.wireOp",EDGE,"E35.6.14.0");Q85=makeQuery(id+"F6.imprint","IMPRINT",FACE,{"disambiguationData":[TD([[makeQuery(id+"F6.imprint","IMPRINT",EDGE,{"derivedFrom":subQ0}),-1.0]])]});}
            var Q86;
            Q86=makeQuery(id+"F6.imprint","IMPRINT",FACE,{"disambiguationData":[TD([[makeQuery(id+"F6.imprint","IMPRINT",EDGE,{"derivedFrom":sQuery(id+"F6.wireOp",EDGE,"E35.0.14.1")}),-1.0]])]});
            var Q87;
            Q87=makeQuery(id+"F6.imprint","IMPRINT",FACE,{"disambiguationData":[TD([[makeQuery(id+"F6.imprint","IMPRINT",EDGE,{"derivedFrom":sQuery(id+"F6.wireOp",EDGE,"E35.0.14.2")}),-1.0]])]});
            var Q88;
            {var subQ5=sQuery(id+"F6.wireOp",EDGE,"E35.33.14.0");Q88=makeQuery(id+"F6.imprint","IMPRINT",FACE,{"disambiguationData":[TD([[makeQuery(id+"F6.imprint","IMPRINT",EDGE,{"derivedFrom":subQ5}),-1.0]])]});}
            var Q89;
            Q89=makeQuery(id+"F6.imprint","IMPRINT",FACE,{"disambiguationData":[TD([[makeQuery(id+"F6.imprint","IMPRINT",EDGE,{"derivedFrom":sQuery(id+"F6.wireOp",EDGE,"E35.18.14.1")}),-1.0]])]});
            var Q90;
            Q90=makeQuery(id+"F6.imprint","IMPRINT",FACE,{"disambiguationData":[TD([[makeQuery(id+"F6.imprint","IMPRINT",EDGE,{"derivedFrom":sQuery(id+"F6.wireOp",EDGE,"E35.18.14.2")}),-1.0]])]});
            var Q91;
            {var subQ5=sQuery(id+"F6.wireOp",EDGE,"E35.24.14.3");Q91=makeQuery(id+"F6.imprint","IMPRINT",FACE,{"disambiguationData":[TD([[makeQuery(id+"F6.imprint","IMPRINT",EDGE,{"derivedFrom":subQ5}),-1.0]])]});}
            var Q92;
            {var subQ0=sQuery(id+"F6.wireOp",EDGE,"E35.6.15.0");Q92=makeQuery(id+"F6.imprint","IMPRINT",FACE,{"disambiguationData":[TD([[makeQuery(id+"F6.imprint","IMPRINT",EDGE,{"derivedFrom":subQ0}),-1.0]])]});}
            var Q93;
            Q93=makeQuery(id+"F6.imprint","IMPRINT",FACE,{"disambiguationData":[TD([[makeQuery(id+"F6.imprint","IMPRINT",EDGE,{"derivedFrom":sQuery(id+"F6.wireOp",EDGE,"E35.0.15.1")}),-1.0]])]});
            var Q94;
            Q94=makeQuery(id+"F6.imprint","IMPRINT",FACE,{"disambiguationData":[TD([[makeQuery(id+"F6.imprint","IMPRINT",EDGE,{"derivedFrom":sQuery(id+"F6.wireOp",EDGE,"E35.0.15.2")}),-1.0]])]});
            var Q95;
            {var subQ5=sQuery(id+"F6.wireOp",EDGE,"E35.33.15.0");Q95=makeQuery(id+"F6.imprint","IMPRINT",FACE,{"disambiguationData":[TD([[makeQuery(id+"F6.imprint","IMPRINT",EDGE,{"derivedFrom":subQ5}),-1.0]])]});}
            var Q96;
            Q96=makeQuery(id+"F6.imprint","IMPRINT",FACE,{"disambiguationData":[TD([[makeQuery(id+"F6.imprint","IMPRINT",EDGE,{"derivedFrom":sQuery(id+"F6.wireOp",EDGE,"E35.18.15.1")}),-1.0]])]});
            var Q97;
            Q97=makeQuery(id+"F6.imprint","IMPRINT",FACE,{"disambiguationData":[TD([[makeQuery(id+"F6.imprint","IMPRINT",EDGE,{"derivedFrom":sQuery(id+"F6.wireOp",EDGE,"E35.18.15.2")}),-1.0]])]});
            var Q98;
            {var subQ5=sQuery(id+"F6.wireOp",EDGE,"E35.24.15.3");Q98=makeQuery(id+"F6.imprint","IMPRINT",FACE,{"disambiguationData":[TD([[makeQuery(id+"F6.imprint","IMPRINT",EDGE,{"derivedFrom":subQ5}),-1.0]])]});}
            var Q99;
            {var subQ6=sQuery(id+"F6.wireOp",EDGE,"E29.2");Q99=makeQuery(id+"F6.imprint","IMPRINT",FACE,{"disambiguationData":[TD([[makeQuery(id+"F6.imprint","IMPRINT",EDGE,{"derivedFrom":subQ6}),-1.0]])]});}
            var Q100;
            {var subQ1=sQuery(id+"F6.wireOp",EDGE,"E31.2.0.7");Q100=makeQuery(id+"F6.imprint","IMPRINT",FACE,{"disambiguationData":[TD([[makeQuery(id+"F6.imprint","IMPRINT",EDGE,{"derivedFrom":subQ1}),-1.0]])]});}
            var Q101;
            {var subQ1=sQuery(id+"F6.wireOp",EDGE,"E34.21.3.0");Q101=makeQuery(id+"F6.imprint","IMPRINT",FACE,{"disambiguationData":[TD([[makeQuery(id+"F6.imprint","IMPRINT",EDGE,{"derivedFrom":subQ1}),-1.0]])]});}
            var Q102;
            Q102=makeQuery(id+"F3.opSweep","SWEPT_FACE",FACE,{"disambiguationData":[OSD([sQuery(id+"F0.wireOp",EDGE,"E0.bottom"),sQuery(id+"F2.wireOp",EDGE,"E7.right")])]});
            extrude(context, id + "F7", {"entities" : qUnion([Q0, Q1, Q2, Q3, Q4, Q5, Q6, Q7, Q8, Q9, Q10, Q11, Q12, Q13, Q14, Q15, Q16, Q17, Q18, Q19, Q20, Q21, Q22, Q23, Q24, Q25, Q26, Q27, Q28, Q29, Q30, Q31, Q32, Q33, Q34, Q35, Q36, Q37, Q38, Q39, Q40, Q41, Q42, Q43, Q44, Q45, Q46, Q47, Q48, Q49, Q50, Q51, Q52, Q53, Q54, Q55, Q56, Q57, Q58, Q59, Q60, Q61, Q62, Q63, Q64, Q65, Q66, Q67, Q68, Q69, Q70, Q71, Q72, Q73, Q74, Q75, Q76, Q77, Q78, Q79, Q80, Q81, Q82, Q83, Q84, Q85, Q86, Q87, Q88, Q89, Q90, Q91, Q92, Q93, Q94, Q95, Q96, Q97, Q98, Q99, Q100, Q101]), "operationType" : NewBodyOperationType.REMOVE, "endBound" : BoundingType.UP_TO_SURFACE, "oppositeDirection" : true, "depth" : 25 * mm, "endBoundEntityFace" : qUnion([Q102]), "offsetDistance" : 25 * mm});
        }
    });
